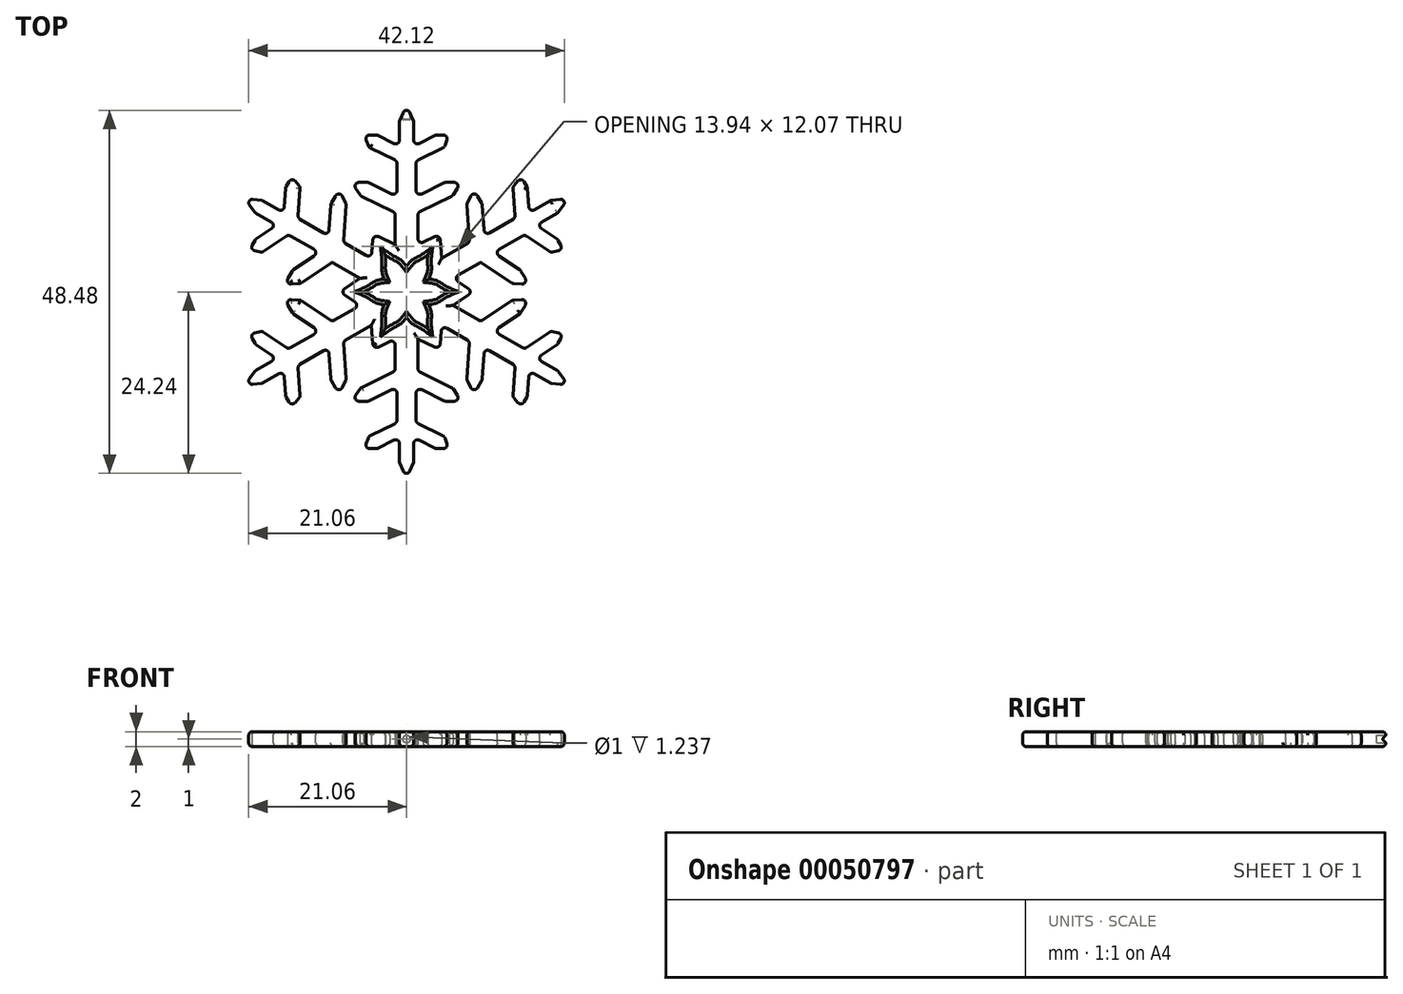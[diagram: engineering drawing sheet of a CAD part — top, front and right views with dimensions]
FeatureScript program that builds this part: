
annotation { "Feature Type Name" : "Feature", "Feature Type Description" : "" }
export const myFeature = defineFeature(function(context is Context, id is Id, definition is map)
    precondition{}
    {
        {
            var Q0;
            Q0=qCreatedBy(makeId("Top.planeOp"),FACE);
            var sketch = newSketch(context, id + "F0", { "sketchPlane" : qUnion([Q0])});
            skLineSegment(sketch, "E0", {"start": v(0, 0) * mm, "end": v(0, 29.9) * mm, "construction": true});
            skCircle(sketch, "E1", {"center": v(0, 0) * mm, "radius": 25 * mm, "construction": true});
            skLineSegment(sketch, "E2", {"start": v(0, 25) * mm, "end": v(0.95, 22.8) * mm});
            skLineSegment(sketch, "E3", {"start": v(0.95, 22.8) * mm, "end": v(0.95, 19.45) * mm});
            skLineSegment(sketch, "E4", {"start": v(0.95, 19.45) * mm, "end": v(4, 20.95) * mm});
            skLineSegment(sketch, "E5", {"start": v(4, 20.95) * mm, "end": v(5.6, 20.95) * mm});
            skLineSegment(sketch, "E6", {"start": v(5.6, 20.95) * mm, "end": v(5.04, 19.3) * mm});
            skLineSegment(sketch, "E7", {"start": v(5.04, 19.3) * mm, "end": v(1.28, 17.45) * mm});
            skLineSegment(sketch, "E8", {"start": v(1.28, 17.45) * mm, "end": v(1.28, 12.72) * mm});
            skLineSegment(sketch, "E9", {"start": v(1.28, 12.72) * mm, "end": v(5.11, 14.6) * mm});
            skLineSegment(sketch, "E10", {"start": v(5.11, 14.6) * mm, "end": v(7.32, 14.6) * mm});
            skLineSegment(sketch, "E11", {"start": v(7.32, 14.6) * mm, "end": v(6.11, 12.82) * mm});
            skLineSegment(sketch, "E12", {"start": v(6.11, 12.82) * mm, "end": v(1.52, 10.57) * mm});
            skLineSegment(sketch, "E13", {"start": v(1.52, 10.57) * mm, "end": v(1.52, 6.3) * mm});
            skLineSegment(sketch, "E14", {"start": v(1.52, 6.3) * mm, "end": v(4.43, 7.68) * mm});
            skLineSegment(sketch, "E15.MirrorCS", {"start": v(-0.95, 22.8) * mm, "end": v(-0.95, 19.45) * mm});
            skLineSegment(sketch, "E16.MirrorCS", {"start": v(-4, 20.95) * mm, "end": v(-5.6, 20.95) * mm});
            skLineSegment(sketch, "E17.MirrorCS", {"start": v(-0.95, 19.45) * mm, "end": v(-4, 20.95) * mm});
            skLineSegment(sketch, "E18.MirrorCS", {"start": v(-1.28, 12.72) * mm, "end": v(-5.11, 14.6) * mm});
            skLineSegment(sketch, "E19.MirrorCS", {"start": v(-5.11, 14.6) * mm, "end": v(-7.32, 14.6) * mm});
            skLineSegment(sketch, "E20.MirrorCS", {"start": v(-7.32, 14.6) * mm, "end": v(-6.11, 12.82) * mm});
            skLineSegment(sketch, "E21.MirrorCS", {"start": v(-1.28, 17.45) * mm, "end": v(-1.28, 12.72) * mm});
            skLineSegment(sketch, "E22.MirrorCS", {"start": v(0, 25) * mm, "end": v(-0.95, 22.8) * mm});
            skLineSegment(sketch, "E23.MirrorCS", {"start": v(-5.6, 20.95) * mm, "end": v(-5.04, 19.3) * mm});
            skLineSegment(sketch, "E24.MirrorCS", {"start": v(-5.04, 19.3) * mm, "end": v(-1.28, 17.45) * mm});
            skLineSegment(sketch, "E25.MirrorCS", {"start": v(-6.11, 12.82) * mm, "end": v(-1.52, 10.57) * mm});
            skLineSegment(sketch, "E26", {"start": v(0, 0) * mm, "end": v(0, 30.32) * mm, "construction": true});
            skLineSegment(sketch, "E27", {"start": v(0, 0) * mm, "end": v(17.52, 30.35) * mm, "construction": true});
            skLineSegment(sketch, "E28", {"start": v(0, 0) * mm, "end": v(-18.63, 32.26) * mm, "construction": true});
            skLineSegment(sketch, "E29", {"start": v(4.43, 7.68) * mm, "end": v(2.85, 4.93) * mm});
            skLineSegment(sketch, "E30.MirrorCS", {"start": v(-1.52, 10.57) * mm, "end": v(-1.52, 6.3) * mm});
            skLineSegment(sketch, "E31.MirrorCS", {"start": v(-1.52, 6.3) * mm, "end": v(-4.43, 7.68) * mm});
            skFitSpline(sketch, "E32", {"points": [v(2.85, 4.93) * mm, v(0, 2.57) * mm], "startDerivative": vector(-4.57, -3.43) * mm, "endDerivative": vector(-3.94, -5.85) * mm});
            skFitSpline(sketch, "E33.MirrorCS", {"points": [v(-2.85, 4.93) * mm, v(0, 2.57) * mm], "startDerivative": vector(4.57, -3.43) * mm, "endDerivative": vector(3.94, -5.85) * mm});
            skLineSegment(sketch, "E34.MirrorCS", {"start": v(-4.43, 7.68) * mm, "end": v(-2.85, 4.93) * mm});
            skSolve(sketch);
        }
        {
            var Q0;
            Q0=makeQuery(id+"F0.imprint","IMPRINT",FACE,{"disambiguationData":[TD([[makeQuery(id+"F0.imprint","IMPRINT",EDGE,{"derivedFrom":sQuery(id+"F0.wireOp",EDGE,"E2")}),-1.0]])]});
            extrude(context, id + "F1", {"entities" : qUnion([Q0]), "endBound" : BoundingType.SYMMETRIC, "depth" : 2 * mm});
        }
        {
            var Q0;
            Q0=qCreatedBy(makeId("Front.planeOp"),FACE);
            var sketch = newSketch(context, id + "F2", { "sketchPlane" : qUnion([Q0])});
            skLineSegment(sketch, "E35", {"start": v(0, -15.67) * mm, "end": v(0, 28.6) * mm, "construction": true});
            skSolve(sketch);
        }
        {
            var Q0;
            Q0=makeQuery(id+"F1.opExtrude","SWEPT_BODY",BODY,{"disambiguationData":[OSD([sQuery(id+"F0.wireOp",EDGE,"E2"),sQuery(id+"F0.wireOp",EDGE,"E3"),sQuery(id+"F0.wireOp",EDGE,"E4"),sQuery(id+"F0.wireOp",EDGE,"E5"),sQuery(id+"F0.wireOp",EDGE,"E6"),sQuery(id+"F0.wireOp",EDGE,"E7"),sQuery(id+"F0.wireOp",EDGE,"E8"),sQuery(id+"F0.wireOp",EDGE,"E9"),sQuery(id+"F0.wireOp",EDGE,"E10"),sQuery(id+"F0.wireOp",EDGE,"E11"),sQuery(id+"F0.wireOp",EDGE,"E12"),sQuery(id+"F0.wireOp",EDGE,"E13"),sQuery(id+"F0.wireOp",EDGE,"E14"),sQuery(id+"F0.wireOp",EDGE,"b2b48e4d-2c92-4a1f-81ad-3469f6dd68cb"),sQuery(id+"F0.wireOp",EDGE,"E15.MirrorCS"),sQuery(id+"F0.wireOp",EDGE,"E16.MirrorCS"),sQuery(id+"F0.wireOp",EDGE,"E17.MirrorCS"),sQuery(id+"F0.wireOp",EDGE,"E18.MirrorCS"),sQuery(id+"F0.wireOp",EDGE,"E19.MirrorCS"),sQuery(id+"F0.wireOp",EDGE,"E20.MirrorCS"),sQuery(id+"F0.wireOp",EDGE,"E21.MirrorCS"),sQuery(id+"F0.wireOp",EDGE,"E22.MirrorCS"),sQuery(id+"F0.wireOp",EDGE,"E23.MirrorCS"),sQuery(id+"F0.wireOp",EDGE,"E24.MirrorCS"),sQuery(id+"F0.wireOp",EDGE,"E160.MirrorCS"),sQuery(id+"F0.wireOp",EDGE,"E25.MirrorCS"),sQuery(id+"F0.wireOp",EDGE,"4b62aa35-2862-45d5-86f5-f30a92808e40"),sQuery(id+"F0.wireOp",EDGE,"c1be86ca-d8b8-4c1e-b1f3-8d63ae980cd1")])]});
            var Q1;
            Q1=sQuery(id+"F2.wireOp",EDGE,"E35");
            circularPattern(context, id + "F3", {"operationType" : NewBodyOperationType.ADD, "entities" : qUnion([Q0]), "axis" : qUnion([Q1]), "angle" : 360 * degree, "instanceCount" : round(6), "equalSpace" : true});
        }
        {
            var Q0;
            Q0=makeQuery(id+"F1.opExtrude","CAP_EDGE",EDGE,{"disambiguationData":[OSD([sQuery(id+"F0.wireOp",EDGE,"E2")])],"isStart":false});
            var Q1;
            Q1=makeQuery(id+"F1.opExtrude","CAP_EDGE",EDGE,{"disambiguationData":[OSD([sQuery(id+"F0.wireOp",EDGE,"E10")])],"isStart":false});
            var Q2;
            Q2=makeQuery(id+"F1.opExtrude","CAP_EDGE",EDGE,{"disambiguationData":[OSD([sQuery(id+"F0.wireOp",EDGE,"E17.MirrorCS")])],"isStart":false});
            var Q3;
            Q3=makeQuery(id+"F1.opExtrude","CAP_EDGE",EDGE,{"disambiguationData":[OSD([sQuery(id+"F0.wireOp",EDGE,"E18.MirrorCS")])],"isStart":true});
            var Q4;
            Q4=makeQuery(id+"F1.opExtrude","CAP_EDGE",EDGE,{"disambiguationData":[OSD([sQuery(id+"F0.wireOp",EDGE,"E3")])],"isStart":false});
            var Q5;
            Q5=makeQuery(id+"F1.opExtrude","CAP_EDGE",EDGE,{"disambiguationData":[OSD([sQuery(id+"F0.wireOp",EDGE,"E18.MirrorCS")])],"isStart":false});
            var Q6;
            Q6=makeQuery(id+"F1.opExtrude","CAP_EDGE",EDGE,{"disambiguationData":[OSD([sQuery(id+"F0.wireOp",EDGE,"E25.MirrorCS")])],"isStart":false});
            var Q7;
            Q7=makeQuery(id+"F1.opExtrude","CAP_EDGE",EDGE,{"disambiguationData":[OSD([sQuery(id+"F0.wireOp",EDGE,"E4")])],"isStart":false});
            var Q8;
            Q8=makeQuery(id+"F1.opExtrude","CAP_EDGE",EDGE,{"disambiguationData":[OSD([sQuery(id+"F0.wireOp",EDGE,"E12")])],"isStart":false});
            var Q9;
            Q9=makeQuery(id+"F1.opExtrude","CAP_EDGE",EDGE,{"disambiguationData":[OSD([sQuery(id+"F0.wireOp",EDGE,"E19.MirrorCS")])],"isStart":false});
            var Q10;
            Q10=makeQuery(id+"F1.opExtrude","CAP_EDGE",EDGE,{"disambiguationData":[OSD([sQuery(id+"F0.wireOp",EDGE,"E13")])],"isStart":false});
            var Q11;
            Q11=makeQuery(id+"F1.opExtrude","CAP_EDGE",EDGE,{"disambiguationData":[OSD([sQuery(id+"F0.wireOp",EDGE,"E21.MirrorCS")])],"isStart":false});
            var Q12;
            Q12=makeQuery(id+"F1.opExtrude","SWEPT_FACE",FACE,{"disambiguationData":[OSD([sQuery(id+"F0.wireOp",EDGE,"E21.MirrorCS")])]});
            var Q13;
            Q13=makeQuery(id+"F1.opExtrude","CAP_EDGE",EDGE,{"disambiguationData":[OSD([sQuery(id+"F0.wireOp",EDGE,"E7")])],"isStart":false});
            var Q14;
            Q14=makeQuery(id+"F1.opExtrude","CAP_EDGE",EDGE,{"disambiguationData":[OSD([sQuery(id+"F0.wireOp",EDGE,"E15.MirrorCS")])],"isStart":false});
            var Q15;
            Q15=makeQuery(id+"F1.opExtrude","CAP_EDGE",EDGE,{"disambiguationData":[OSD([sQuery(id+"F0.wireOp",EDGE,"E8")])],"isStart":false});
            var Q16;
            Q16=makeQuery(id+"F3.opPattern","COPY",EDGE,{"derivedFrom":makeQuery(id+"F1.opExtrude","CAP_EDGE",EDGE,{"disambiguationData":[OSD([sQuery(id+"F0.wireOp",EDGE,"E12")])],"isStart":false}),"instanceName":"4"});
            var Q17;
            Q17=makeQuery(id+"F3.opPattern","COPY",EDGE,{"derivedFrom":makeQuery(id+"F1.opExtrude","CAP_EDGE",EDGE,{"disambiguationData":[OSD([sQuery(id+"F0.wireOp",EDGE,"E4")])],"isStart":false}),"instanceName":"4"});
            var Q18;
            Q18=makeQuery(id+"F3.opPattern","COPY",EDGE,{"derivedFrom":makeQuery(id+"F1.opExtrude","CAP_EDGE",EDGE,{"disambiguationData":[OSD([sQuery(id+"F0.wireOp",EDGE,"E17.MirrorCS")])],"isStart":false}),"instanceName":"5"});
            var Q19;
            Q19=makeQuery(id+"F3.opPattern","COPY",EDGE,{"derivedFrom":makeQuery(id+"F1.opExtrude","CAP_EDGE",EDGE,{"disambiguationData":[OSD([sQuery(id+"F0.wireOp",EDGE,"E10")])],"isStart":false}),"instanceName":"5"});
            var Q20;
            Q20=makeQuery(id+"F3.opPattern","COPY",EDGE,{"derivedFrom":makeQuery(id+"F1.opExtrude","CAP_EDGE",EDGE,{"disambiguationData":[OSD([sQuery(id+"F0.wireOp",EDGE,"E17.MirrorCS")])],"isStart":false}),"instanceName":"1"});
            var Q21;
            Q21=makeQuery(id+"F3.opPattern","COPY",EDGE,{"derivedFrom":makeQuery(id+"F1.opExtrude","CAP_EDGE",EDGE,{"disambiguationData":[OSD([sQuery(id+"F0.wireOp",EDGE,"E2")])],"isStart":false}),"instanceName":"1"});
            var Q22;
            Q22=makeQuery(id+"F3.opPattern","COPY",EDGE,{"derivedFrom":makeQuery(id+"F1.opExtrude","CAP_EDGE",EDGE,{"disambiguationData":[OSD([sQuery(id+"F0.wireOp",EDGE,"E15.MirrorCS")])],"isStart":false}),"instanceName":"2"});
            var Q23;
            Q23=makeQuery(id+"F3.opPattern","COPY",EDGE,{"derivedFrom":makeQuery(id+"F1.opExtrude","CAP_EDGE",EDGE,{"disambiguationData":[OSD([sQuery(id+"F0.wireOp",EDGE,"E21.MirrorCS")])],"isStart":false}),"instanceName":"3"});
            var Q24;
            Q24=makeQuery(id+"F1.opExtrude","CAP_EDGE",EDGE,{"disambiguationData":[OSD([sQuery(id+"F0.wireOp",EDGE,"E24.MirrorCS")])],"isStart":false});
            var Q25;
            Q25=makeQuery(id+"F1.opExtrude","CAP_EDGE",EDGE,{"disambiguationData":[OSD([sQuery(id+"F0.wireOp",EDGE,"E9")])],"isStart":false});
            var Q26;
            Q26=makeQuery(id+"F3.opPattern","COPY",FACE,{"derivedFrom":makeQuery(id+"F1.opExtrude","SWEPT_FACE",FACE,{"disambiguationData":[OSD([sQuery(id+"F0.wireOp",EDGE,"E21.MirrorCS")])]}),"instanceName":"5"});
            var Q27;
            Q27=makeQuery(id+"F3.opPattern","COPY",EDGE,{"derivedFrom":makeQuery(id+"F1.opExtrude","CAP_EDGE",EDGE,{"disambiguationData":[OSD([sQuery(id+"F0.wireOp",EDGE,"E25.MirrorCS")])],"isStart":false}),"instanceName":"5"});
            var Q28;
            Q28=makeQuery(id+"F3.opPattern","COPY",EDGE,{"derivedFrom":makeQuery(id+"F1.opExtrude","CAP_EDGE",EDGE,{"disambiguationData":[OSD([sQuery(id+"F0.wireOp",EDGE,"E25.MirrorCS")])],"isStart":false}),"instanceName":"1"});
            var Q29;
            Q29=makeQuery(id+"F3.opPattern","COPY",EDGE,{"derivedFrom":makeQuery(id+"F1.opExtrude","CAP_EDGE",EDGE,{"disambiguationData":[OSD([sQuery(id+"F0.wireOp",EDGE,"E18.MirrorCS")])],"isStart":false}),"instanceName":"1"});
            var Q30;
            Q30=makeQuery(id+"F3.opPattern","COPY",EDGE,{"derivedFrom":makeQuery(id+"F1.opExtrude","CAP_EDGE",EDGE,{"disambiguationData":[OSD([sQuery(id+"F0.wireOp",EDGE,"E3")])],"isStart":false}),"instanceName":"1"});
            var Q31;
            Q31=makeQuery(id+"F3.opPattern","COPY",EDGE,{"derivedFrom":makeQuery(id+"F1.opExtrude","CAP_EDGE",EDGE,{"disambiguationData":[OSD([sQuery(id+"F0.wireOp",EDGE,"E9")])],"isStart":false}),"instanceName":"2"});
            var Q32;
            Q32=makeQuery(id+"F3.opPattern","COPY",EDGE,{"derivedFrom":makeQuery(id+"F1.opExtrude","CAP_EDGE",EDGE,{"disambiguationData":[OSD([sQuery(id+"F0.wireOp",EDGE,"E7")])],"isStart":false}),"instanceName":"3"});
            var Q33;
            Q33=makeQuery(id+"F3.opPattern","COPY",EDGE,{"derivedFrom":makeQuery(id+"F1.opExtrude","CAP_EDGE",EDGE,{"disambiguationData":[OSD([sQuery(id+"F0.wireOp",EDGE,"E24.MirrorCS")])],"isStart":false}),"instanceName":"2"});
            var Q34;
            Q34=makeQuery(id+"F3.opPattern","COPY",EDGE,{"derivedFrom":makeQuery(id+"F1.opExtrude","CAP_EDGE",EDGE,{"disambiguationData":[OSD([sQuery(id+"F0.wireOp",EDGE,"E20.MirrorCS")])],"isStart":false}),"instanceName":"4"});
            var Q35;
            Q35=makeQuery(id+"F3.opPattern","COPY",EDGE,{"derivedFrom":makeQuery(id+"F1.opExtrude","CAP_EDGE",EDGE,{"disambiguationData":[OSD([sQuery(id+"F0.wireOp",EDGE,"E18.MirrorCS")])],"isStart":false}),"instanceName":"5"});
            var Q36;
            Q36=makeQuery(id+"F3.opPattern","COPY",EDGE,{"derivedFrom":makeQuery(id+"F1.opExtrude","CAP_EDGE",EDGE,{"disambiguationData":[OSD([sQuery(id+"F0.wireOp",EDGE,"E13")])],"isStart":false}),"instanceName":"4"});
            var Q37;
            Q37=makeQuery(id+"F3.opPattern","COPY",EDGE,{"derivedFrom":makeQuery(id+"F1.opExtrude","CAP_EDGE",EDGE,{"disambiguationData":[OSD([sQuery(id+"F0.wireOp",EDGE,"E3")])],"isStart":false}),"instanceName":"5"});
            var Q38;
            Q38=makeQuery(id+"F3.opPattern","COPY",EDGE,{"derivedFrom":makeQuery(id+"F1.opExtrude","CAP_EDGE",EDGE,{"disambiguationData":[OSD([sQuery(id+"F0.wireOp",EDGE,"E4")])],"isStart":true}),"instanceName":"5"});
            var Q39;
            Q39=makeQuery(id+"F3.opPattern","COPY",FACE,{"derivedFrom":makeQuery(id+"F1.opExtrude","SWEPT_FACE",FACE,{"disambiguationData":[OSD([sQuery(id+"F0.wireOp",EDGE,"E21.MirrorCS")])]}),"instanceName":"4"});
            var Q40;
            Q40=makeQuery(id+"F3.opPattern","COPY",EDGE,{"derivedFrom":makeQuery(id+"F1.opExtrude","CAP_EDGE",EDGE,{"disambiguationData":[OSD([sQuery(id+"F0.wireOp",EDGE,"E2")])],"isStart":false}),"instanceName":"2"});
            var Q41;
            Q41=makeQuery(id+"F3.opPattern","COPY",EDGE,{"derivedFrom":makeQuery(id+"F1.opExtrude","CAP_EDGE",EDGE,{"disambiguationData":[OSD([sQuery(id+"F0.wireOp",EDGE,"E17.MirrorCS")])],"isStart":false}),"instanceName":"2"});
            var Q42;
            Q42=makeQuery(id+"F3.opPattern","COPY",EDGE,{"derivedFrom":makeQuery(id+"F1.opExtrude","CAP_EDGE",EDGE,{"disambiguationData":[OSD([sQuery(id+"F0.wireOp",EDGE,"E10")])],"isStart":false}),"instanceName":"2"});
            var Q43;
            Q43=makeQuery(id+"F3.opPattern","COPY",EDGE,{"derivedFrom":makeQuery(id+"F1.opExtrude","CAP_EDGE",EDGE,{"disambiguationData":[OSD([sQuery(id+"F0.wireOp",EDGE,"E8")])],"isStart":false}),"instanceName":"3"});
            var Q44;
            Q44=makeQuery(id+"F3.opPattern","COPY",EDGE,{"derivedFrom":makeQuery(id+"F1.opExtrude","CAP_EDGE",EDGE,{"disambiguationData":[OSD([sQuery(id+"F0.wireOp",EDGE,"E15.MirrorCS")])],"isStart":false}),"instanceName":"3"});
            var Q45;
            Q45=makeQuery(id+"F3.opPattern","COPY",EDGE,{"derivedFrom":makeQuery(id+"F1.opExtrude","CAP_EDGE",EDGE,{"disambiguationData":[OSD([sQuery(id+"F0.wireOp",EDGE,"E21.MirrorCS")])],"isStart":false}),"instanceName":"4"});
            var Q46;
            Q46=makeQuery(id+"F3.opPattern","COPY",EDGE,{"derivedFrom":makeQuery(id+"F1.opExtrude","CAP_EDGE",EDGE,{"disambiguationData":[OSD([sQuery(id+"F0.wireOp",EDGE,"E19.MirrorCS")])],"isStart":false}),"instanceName":"5"});
            var Q47;
            Q47=makeQuery(id+"F3.opPattern","COPY",EDGE,{"derivedFrom":makeQuery(id+"F1.opExtrude","CAP_EDGE",EDGE,{"disambiguationData":[OSD([sQuery(id+"F0.wireOp",EDGE,"E4")])],"isStart":false}),"instanceName":"5"});
            var Q48;
            Q48=makeQuery(id+"F3.opPattern","COPY",EDGE,{"derivedFrom":makeQuery(id+"F1.opExtrude","CAP_EDGE",EDGE,{"disambiguationData":[OSD([sQuery(id+"F0.wireOp",EDGE,"E12")])],"isStart":false}),"instanceName":"5"});
            var Q49;
            Q49=makeQuery(id+"F3.opPattern","COPY",EDGE,{"derivedFrom":makeQuery(id+"F1.opExtrude","CAP_EDGE",EDGE,{"disambiguationData":[OSD([sQuery(id+"F0.wireOp",EDGE,"E12")])],"isStart":false}),"instanceName":"1"});
            var Q50;
            Q50=makeQuery(id+"F3.opPattern","COPY",EDGE,{"derivedFrom":makeQuery(id+"F1.opExtrude","CAP_EDGE",EDGE,{"disambiguationData":[OSD([sQuery(id+"F0.wireOp",EDGE,"E19.MirrorCS")])],"isStart":false}),"instanceName":"1"});
            var Q51;
            Q51=makeQuery(id+"F3.opPattern","COPY",EDGE,{"derivedFrom":makeQuery(id+"F1.opExtrude","CAP_EDGE",EDGE,{"disambiguationData":[OSD([sQuery(id+"F0.wireOp",EDGE,"E4")])],"isStart":false}),"instanceName":"1"});
            var Q52;
            Q52=makeQuery(id+"F3.opPattern","COPY",EDGE,{"derivedFrom":makeQuery(id+"F1.opExtrude","CAP_EDGE",EDGE,{"disambiguationData":[OSD([sQuery(id+"F0.wireOp",EDGE,"E24.MirrorCS")])],"isStart":false}),"instanceName":"3"});
            var Q53;
            Q53=makeQuery(id+"F3.opPattern","COPY",EDGE,{"derivedFrom":makeQuery(id+"F1.opExtrude","CAP_EDGE",EDGE,{"disambiguationData":[OSD([sQuery(id+"F0.wireOp",EDGE,"E13")])],"isStart":false}),"instanceName":"5"});
            var Q54;
            Q54=makeQuery(id+"F3.opPattern","COPY",EDGE,{"derivedFrom":makeQuery(id+"F1.opExtrude","CAP_EDGE",EDGE,{"disambiguationData":[OSD([sQuery(id+"F0.wireOp",EDGE,"E7")])],"isStart":false}),"instanceName":"4"});
            var Q55;
            Q55=makeQuery(id+"F3.opPattern","COPY",FACE,{"derivedFrom":makeQuery(id+"F1.opExtrude","SWEPT_FACE",FACE,{"disambiguationData":[OSD([sQuery(id+"F0.wireOp",EDGE,"E18.MirrorCS")])]}),"instanceName":"1"});
            var Q56;
            Q56=makeQuery(id+"F3.opPattern","COPY",FACE,{"derivedFrom":makeQuery(id+"F1.opExtrude","SWEPT_FACE",FACE,{"disambiguationData":[OSD([sQuery(id+"F0.wireOp",EDGE,"E24.MirrorCS")])]}),"instanceName":"4"});
            var Q57;
            Q57=makeQuery(id+"F3.opPattern","COPY",EDGE,{"derivedFrom":makeQuery(id+"F1.opExtrude","CAP_EDGE",EDGE,{"disambiguationData":[OSD([sQuery(id+"F0.wireOp",EDGE,"E13")])],"isStart":false}),"instanceName":"1"});
            var Q58;
            Q58=makeQuery(id+"F3.opPattern","COPY",EDGE,{"derivedFrom":makeQuery(id+"F1.opExtrude","CAP_EDGE",EDGE,{"disambiguationData":[OSD([sQuery(id+"F0.wireOp",EDGE,"E18.MirrorCS")])],"isStart":false}),"instanceName":"2"});
            var Q59;
            Q59=makeQuery(id+"F3.opPattern","COPY",EDGE,{"derivedFrom":makeQuery(id+"F1.opExtrude","CAP_EDGE",EDGE,{"disambiguationData":[OSD([sQuery(id+"F0.wireOp",EDGE,"E3")])],"isStart":false}),"instanceName":"2"});
            var Q60;
            Q60=makeQuery(id+"F3.opPattern","COPY",EDGE,{"derivedFrom":makeQuery(id+"F1.opExtrude","CAP_EDGE",EDGE,{"disambiguationData":[OSD([sQuery(id+"F0.wireOp",EDGE,"E9")])],"isStart":false}),"instanceName":"3"});
            var Q61;
            Q61=makeQuery(id+"F3.opPattern","COPY",EDGE,{"derivedFrom":makeQuery(id+"F1.opExtrude","CAP_EDGE",EDGE,{"disambiguationData":[OSD([sQuery(id+"F0.wireOp",EDGE,"E25.MirrorCS")])],"isStart":false}),"instanceName":"2"});
            var Q62;
            Q62=makeQuery(id+"F3.opPattern","COPY",EDGE,{"derivedFrom":makeQuery(id+"F1.opExtrude","CAP_EDGE",EDGE,{"disambiguationData":[OSD([sQuery(id+"F0.wireOp",EDGE,"E21.MirrorCS")])],"isStart":false}),"instanceName":"5"});
            var Q63;
            Q63=makeQuery(id+"F3.opPattern","COPY",FACE,{"derivedFrom":makeQuery(id+"F1.opExtrude","SWEPT_FACE",FACE,{"disambiguationData":[OSD([sQuery(id+"F0.wireOp",EDGE,"E24.MirrorCS")])]}),"instanceName":"3"});
            var Q64;
            Q64=makeQuery(id+"F3.opPattern","COPY",EDGE,{"derivedFrom":makeQuery(id+"F1.opExtrude","CAP_EDGE",EDGE,{"disambiguationData":[OSD([sQuery(id+"F0.wireOp",EDGE,"E21.MirrorCS")])],"isStart":false}),"instanceName":"1"});
            var Q65;
            Q65=makeQuery(id+"F3.opPattern","COPY",EDGE,{"derivedFrom":makeQuery(id+"F1.opExtrude","CAP_EDGE",EDGE,{"disambiguationData":[OSD([sQuery(id+"F0.wireOp",EDGE,"E14")])],"isStart":false}),"instanceName":"1"});
            var Q66;
            Q66=makeQuery(id+"F3.opPattern","COPY",EDGE,{"derivedFrom":makeQuery(id+"F1.opExtrude","CAP_EDGE",EDGE,{"disambiguationData":[OSD([sQuery(id+"F0.wireOp",EDGE,"E19.MirrorCS")])],"isStart":false}),"instanceName":"2"});
            var Q67;
            Q67=makeQuery(id+"F3.opPattern","COPY",EDGE,{"derivedFrom":makeQuery(id+"F1.opExtrude","CAP_EDGE",EDGE,{"disambiguationData":[OSD([sQuery(id+"F0.wireOp",EDGE,"E12")])],"isStart":false}),"instanceName":"2"});
            var Q68;
            Q68=makeQuery(id+"F3.opPattern","COPY",EDGE,{"derivedFrom":makeQuery(id+"F1.opExtrude","CAP_EDGE",EDGE,{"disambiguationData":[OSD([sQuery(id+"F0.wireOp",EDGE,"E4")])],"isStart":false}),"instanceName":"2"});
            var Q69;
            Q69=makeQuery(id+"F3.opPattern","COPY",EDGE,{"derivedFrom":makeQuery(id+"F1.opExtrude","CAP_EDGE",EDGE,{"disambiguationData":[OSD([sQuery(id+"F0.wireOp",EDGE,"E2")])],"isStart":false}),"instanceName":"3"});
            var Q70;
            Q70=makeQuery(id+"F3.opPattern","COPY",EDGE,{"derivedFrom":makeQuery(id+"F1.opExtrude","CAP_EDGE",EDGE,{"disambiguationData":[OSD([sQuery(id+"F0.wireOp",EDGE,"E17.MirrorCS")])],"isStart":false}),"instanceName":"3"});
            var Q71;
            Q71=makeQuery(id+"F3.opPattern","COPY",EDGE,{"derivedFrom":makeQuery(id+"F1.opExtrude","CAP_EDGE",EDGE,{"disambiguationData":[OSD([sQuery(id+"F0.wireOp",EDGE,"E8")])],"isStart":false}),"instanceName":"4"});
            var Q72;
            Q72=makeQuery(id+"F3.opPattern","COPY",EDGE,{"derivedFrom":makeQuery(id+"F1.opExtrude","CAP_EDGE",EDGE,{"disambiguationData":[OSD([sQuery(id+"F0.wireOp",EDGE,"E7")])],"isStart":false}),"instanceName":"1"});
            var Q73;
            Q73=makeQuery(id+"F3.opPattern","COPY",FACE,{"derivedFrom":makeQuery(id+"F1.opExtrude","SWEPT_FACE",FACE,{"disambiguationData":[OSD([sQuery(id+"F0.wireOp",EDGE,"E25.MirrorCS")])]}),"instanceName":"3"});
            var Q74;
            Q74=makeQuery(id+"F3.opPattern","COPY",EDGE,{"derivedFrom":makeQuery(id+"F1.opExtrude","CAP_EDGE",EDGE,{"disambiguationData":[OSD([sQuery(id+"F0.wireOp",EDGE,"E5")])],"isStart":false}),"instanceName":"2"});
            var Q75;
            Q75=makeQuery(id+"F3.opPattern","COPY",EDGE,{"derivedFrom":makeQuery(id+"F1.opExtrude","CAP_EDGE",EDGE,{"disambiguationData":[OSD([sQuery(id+"F0.wireOp",EDGE,"E13")])],"isStart":false}),"instanceName":"2"});
            var Q76;
            Q76=makeQuery(id+"F3.opPattern","COPY",EDGE,{"derivedFrom":makeQuery(id+"F1.opExtrude","CAP_EDGE",EDGE,{"disambiguationData":[OSD([sQuery(id+"F0.wireOp",EDGE,"E18.MirrorCS")])],"isStart":false}),"instanceName":"3"});
            var Q77;
            Q77=makeQuery(id+"F3.opPattern","COPY",EDGE,{"derivedFrom":makeQuery(id+"F1.opExtrude","CAP_EDGE",EDGE,{"disambiguationData":[OSD([sQuery(id+"F0.wireOp",EDGE,"E25.MirrorCS")])],"isStart":false}),"instanceName":"3"});
            var Q78;
            Q78=makeQuery(id+"F3.opPattern","COPY",EDGE,{"derivedFrom":makeQuery(id+"F1.opExtrude","CAP_EDGE",EDGE,{"disambiguationData":[OSD([sQuery(id+"F0.wireOp",EDGE,"E3")])],"isStart":false}),"instanceName":"3"});
            var Q79;
            Q79=makeQuery(id+"F3.opPattern","COPY",EDGE,{"derivedFrom":makeQuery(id+"F1.opExtrude","CAP_EDGE",EDGE,{"disambiguationData":[OSD([sQuery(id+"F0.wireOp",EDGE,"E9")])],"isStart":false}),"instanceName":"4"});
            var Q80;
            Q80=makeQuery(id+"F3.opPattern","COPY",EDGE,{"derivedFrom":makeQuery(id+"F1.opExtrude","CAP_EDGE",EDGE,{"disambiguationData":[OSD([sQuery(id+"F0.wireOp",EDGE,"E7")])],"isStart":false}),"instanceName":"5"});
            var Q81;
            Q81=makeQuery(id+"F3.opPattern","COPY",EDGE,{"derivedFrom":makeQuery(id+"F1.opExtrude","CAP_EDGE",EDGE,{"disambiguationData":[OSD([sQuery(id+"F0.wireOp",EDGE,"E24.MirrorCS")])],"isStart":false}),"instanceName":"4"});
            var Q82;
            Q82=makeQuery(id+"F3.opPattern","COPY",EDGE,{"derivedFrom":makeQuery(id+"F1.opExtrude","SWEPT_EDGE",EDGE,{"disambiguationData":[OSD([sQuery(id+"F0.wireOp",EDGE,"E23.MirrorCS"),sQuery(id+"F0.wireOp",EDGE,"E24.MirrorCS")])]}),"instanceName":"1"});
            var Q83;
            Q83=makeQuery(id+"F3.opPattern","COPY",FACE,{"derivedFrom":makeQuery(id+"F1.opExtrude","SWEPT_FACE",FACE,{"disambiguationData":[OSD([sQuery(id+"F0.wireOp",EDGE,"E12")])]}),"instanceName":"3"});
            var Q84;
            Q84=makeQuery(id+"F3.opPattern","COPY",EDGE,{"derivedFrom":makeQuery(id+"F1.opExtrude","CAP_EDGE",EDGE,{"disambiguationData":[OSD([sQuery(id+"F0.wireOp",EDGE,"E15.MirrorCS")])],"isStart":false}),"instanceName":"1"});
            var Q85;
            Q85=makeQuery(id+"F3.opPattern","COPY",EDGE,{"derivedFrom":makeQuery(id+"F1.opExtrude","CAP_EDGE",EDGE,{"disambiguationData":[OSD([sQuery(id+"F0.wireOp",EDGE,"E8")])],"isStart":false}),"instanceName":"1"});
            var Q86;
            Q86=makeQuery(id+"F3.opPattern","COPY",EDGE,{"derivedFrom":makeQuery(id+"F1.opExtrude","CAP_EDGE",EDGE,{"disambiguationData":[OSD([sQuery(id+"F0.wireOp",EDGE,"E21.MirrorCS")])],"isStart":false}),"instanceName":"2"});
            var Q87;
            Q87=makeQuery(id+"F3.opPattern","COPY",EDGE,{"derivedFrom":makeQuery(id+"F1.opExtrude","CAP_EDGE",EDGE,{"disambiguationData":[OSD([sQuery(id+"F0.wireOp",EDGE,"E12")])],"isStart":false}),"instanceName":"3"});
            var Q88;
            Q88=makeQuery(id+"F3.opPattern","COPY",EDGE,{"derivedFrom":makeQuery(id+"F1.opExtrude","CAP_EDGE",EDGE,{"disambiguationData":[OSD([sQuery(id+"F0.wireOp",EDGE,"E17.MirrorCS")])],"isStart":false}),"instanceName":"4"});
            var Q89;
            Q89=makeQuery(id+"F3.opPattern","COPY",EDGE,{"derivedFrom":makeQuery(id+"F1.opExtrude","CAP_EDGE",EDGE,{"disambiguationData":[OSD([sQuery(id+"F0.wireOp",EDGE,"E4")])],"isStart":false}),"instanceName":"3"});
            var Q90;
            Q90=makeQuery(id+"F3.opPattern","COPY",EDGE,{"derivedFrom":makeQuery(id+"F1.opExtrude","CAP_EDGE",EDGE,{"disambiguationData":[OSD([sQuery(id+"F0.wireOp",EDGE,"E2")])],"isStart":false}),"instanceName":"4"});
            var Q91;
            Q91=makeQuery(id+"F3.opPattern","COPY",EDGE,{"derivedFrom":makeQuery(id+"F1.opExtrude","CAP_EDGE",EDGE,{"disambiguationData":[OSD([sQuery(id+"F0.wireOp",EDGE,"E10")])],"isStart":false}),"instanceName":"4"});
            var Q92;
            Q92=makeQuery(id+"F3.opPattern","COPY",FACE,{"derivedFrom":makeQuery(id+"F1.opExtrude","SWEPT_FACE",FACE,{"disambiguationData":[OSD([sQuery(id+"F0.wireOp",EDGE,"E13")])]}),"instanceName":"3"});
            var Q93;
            Q93=makeQuery(id+"F3.opPattern","COPY",EDGE,{"derivedFrom":makeQuery(id+"F1.opExtrude","CAP_EDGE",EDGE,{"disambiguationData":[OSD([sQuery(id+"F0.wireOp",EDGE,"E160.MirrorCS")])],"isStart":false}),"instanceName":"4"});
            var Q94;
            Q94=makeQuery(id+"F3.opPattern","COPY",FACE,{"derivedFrom":makeQuery(id+"F1.opExtrude","SWEPT_FACE",FACE,{"disambiguationData":[OSD([sQuery(id+"F0.wireOp",EDGE,"E12")])]}),"instanceName":"2"});
            var Q95;
            Q95=makeQuery(id+"F3.opPattern","COPY",FACE,{"derivedFrom":makeQuery(id+"F1.opExtrude","SWEPT_FACE",FACE,{"disambiguationData":[OSD([sQuery(id+"F0.wireOp",EDGE,"E15.MirrorCS")])]}),"instanceName":"4"});
            var Q96;
            Q96=makeQuery(id+"F3.opPattern","COPY",EDGE,{"derivedFrom":makeQuery(id+"F1.opExtrude","CAP_EDGE",EDGE,{"disambiguationData":[OSD([sQuery(id+"F0.wireOp",EDGE,"E7")])],"isStart":false}),"instanceName":"2"});
            var Q97;
            Q97=makeQuery(id+"F3.opPattern","COPY",EDGE,{"derivedFrom":makeQuery(id+"F1.opExtrude","CAP_EDGE",EDGE,{"disambiguationData":[OSD([sQuery(id+"F0.wireOp",EDGE,"E9")])],"isStart":false}),"instanceName":"1"});
            var Q98;
            Q98=makeQuery(id+"F3.opPattern","COPY",EDGE,{"derivedFrom":makeQuery(id+"F1.opExtrude","CAP_EDGE",EDGE,{"disambiguationData":[OSD([sQuery(id+"F0.wireOp",EDGE,"E24.MirrorCS")])],"isStart":false}),"instanceName":"1"});
            var Q99;
            Q99=makeQuery(id+"F3.opPattern","COPY",EDGE,{"derivedFrom":makeQuery(id+"F1.opExtrude","CAP_EDGE",EDGE,{"disambiguationData":[OSD([sQuery(id+"F0.wireOp",EDGE,"E18.MirrorCS")])],"isStart":false}),"instanceName":"4"});
            var Q100;
            Q100=makeQuery(id+"F3.opPattern","COPY",EDGE,{"derivedFrom":makeQuery(id+"F1.opExtrude","CAP_EDGE",EDGE,{"disambiguationData":[OSD([sQuery(id+"F0.wireOp",EDGE,"E3")])],"isStart":false}),"instanceName":"4"});
            var Q101;
            Q101=makeQuery(id+"F3.opPattern","COPY",EDGE,{"derivedFrom":makeQuery(id+"F1.opExtrude","CAP_EDGE",EDGE,{"disambiguationData":[OSD([sQuery(id+"F0.wireOp",EDGE,"E24.MirrorCS")])],"isStart":false}),"instanceName":"5"});
            var Q102;
            Q102=makeQuery(id+"F3.opPattern","COPY",EDGE,{"derivedFrom":makeQuery(id+"F1.opExtrude","CAP_EDGE",EDGE,{"disambiguationData":[OSD([sQuery(id+"F0.wireOp",EDGE,"E9")])],"isStart":false}),"instanceName":"5"});
            var Q103;
            Q103=makeQuery(id+"F3.opPattern","COPY",EDGE,{"derivedFrom":makeQuery(id+"F1.opExtrude","CAP_EDGE",EDGE,{"disambiguationData":[OSD([sQuery(id+"F0.wireOp",EDGE,"E25.MirrorCS")])],"isStart":false}),"instanceName":"4"});
            var Q104;
            Q104=makeQuery(id+"F3.opPattern","COPY",FACE,{"derivedFrom":makeQuery(id+"F1.opExtrude","SWEPT_FACE",FACE,{"disambiguationData":[OSD([sQuery(id+"F0.wireOp",EDGE,"E13")])]}),"instanceName":"2"});
            var Q105;
            Q105=makeQuery(id+"F3.opPattern","COPY",EDGE,{"derivedFrom":makeQuery(id+"F1.opExtrude","CAP_EDGE",EDGE,{"disambiguationData":[OSD([sQuery(id+"F0.wireOp",EDGE,"E12")])],"isStart":true}),"instanceName":"4"});
            var Q106;
            Q106=makeQuery(id+"F3.opPattern","COPY",EDGE,{"derivedFrom":makeQuery(id+"F1.opExtrude","CAP_EDGE",EDGE,{"disambiguationData":[OSD([sQuery(id+"F0.wireOp",EDGE,"E160.MirrorCS")])],"isStart":false}),"instanceName":"5"});
            var Q107;
            Q107=makeQuery(id+"F1.opExtrude","SWEPT_FACE",FACE,{"disambiguationData":[OSD([sQuery(id+"F0.wireOp",EDGE,"E4")])]});
            var Q108;
            Q108=makeQuery(id+"F3.opPattern","COPY",EDGE,{"derivedFrom":makeQuery(id+"F1.opExtrude","CAP_EDGE",EDGE,{"disambiguationData":[OSD([sQuery(id+"F0.wireOp",EDGE,"E160.MirrorCS")])],"isStart":false}),"instanceName":"3"});
            var Q109;
            {var subQ0=makeQuery(id+"F1.opExtrude","CAP_FACE",FACE,{"disambiguationData":[OSD([sQuery(id+"F0.wireOp",EDGE,"E2"),sQuery(id+"F0.wireOp",EDGE,"E3"),sQuery(id+"F0.wireOp",EDGE,"E4"),sQuery(id+"F0.wireOp",EDGE,"E5"),sQuery(id+"F0.wireOp",EDGE,"E6"),sQuery(id+"F0.wireOp",EDGE,"E7"),sQuery(id+"F0.wireOp",EDGE,"E8"),sQuery(id+"F0.wireOp",EDGE,"E9"),sQuery(id+"F0.wireOp",EDGE,"E10"),sQuery(id+"F0.wireOp",EDGE,"E11"),sQuery(id+"F0.wireOp",EDGE,"E12"),sQuery(id+"F0.wireOp",EDGE,"E13"),sQuery(id+"F0.wireOp",EDGE,"E14"),sQuery(id+"F0.wireOp",EDGE,"b2b48e4d-2c92-4a1f-81ad-3469f6dd68cb"),sQuery(id+"F0.wireOp",EDGE,"E15.MirrorCS"),sQuery(id+"F0.wireOp",EDGE,"E16.MirrorCS"),sQuery(id+"F0.wireOp",EDGE,"E17.MirrorCS"),sQuery(id+"F0.wireOp",EDGE,"E18.MirrorCS"),sQuery(id+"F0.wireOp",EDGE,"E19.MirrorCS"),sQuery(id+"F0.wireOp",EDGE,"E20.MirrorCS"),sQuery(id+"F0.wireOp",EDGE,"E21.MirrorCS"),sQuery(id+"F0.wireOp",EDGE,"E22.MirrorCS"),sQuery(id+"F0.wireOp",EDGE,"E23.MirrorCS"),sQuery(id+"F0.wireOp",EDGE,"E24.MirrorCS"),sQuery(id+"F0.wireOp",EDGE,"E160.MirrorCS"),sQuery(id+"F0.wireOp",EDGE,"E25.MirrorCS"),sQuery(id+"F0.wireOp",EDGE,"4b62aa35-2862-45d5-86f5-f30a92808e40"),sQuery(id+"F0.wireOp",EDGE,"c1be86ca-d8b8-4c1e-b1f3-8d63ae980cd1")])],"isStart":true});Q109=makeQuery(id+"F3.boolean.opBoolean","MERGE",FACE,{"derivedFrom":[subQ0,makeQuery(id+"F3.opPattern","COPY",FACE,{"derivedFrom":subQ0,"instanceName":"1"}),makeQuery(id+"F3.opPattern","COPY",FACE,{"derivedFrom":subQ0,"instanceName":"2"}),makeQuery(id+"F3.opPattern","COPY",FACE,{"derivedFrom":subQ0,"instanceName":"3"}),makeQuery(id+"F3.opPattern","COPY",FACE,{"derivedFrom":subQ0,"instanceName":"4"}),makeQuery(id+"F3.opPattern","COPY",FACE,{"derivedFrom":subQ0,"instanceName":"5"})]});}
            var Q110;
            {var subQ0=makeQuery(id+"F1.opExtrude","CAP_FACE",FACE,{"disambiguationData":[OSD([sQuery(id+"F0.wireOp",EDGE,"E2"),sQuery(id+"F0.wireOp",EDGE,"E3"),sQuery(id+"F0.wireOp",EDGE,"E4"),sQuery(id+"F0.wireOp",EDGE,"E5"),sQuery(id+"F0.wireOp",EDGE,"E6"),sQuery(id+"F0.wireOp",EDGE,"E7"),sQuery(id+"F0.wireOp",EDGE,"E8"),sQuery(id+"F0.wireOp",EDGE,"E9"),sQuery(id+"F0.wireOp",EDGE,"E10"),sQuery(id+"F0.wireOp",EDGE,"E11"),sQuery(id+"F0.wireOp",EDGE,"E12"),sQuery(id+"F0.wireOp",EDGE,"E13"),sQuery(id+"F0.wireOp",EDGE,"E14"),sQuery(id+"F0.wireOp",EDGE,"b2b48e4d-2c92-4a1f-81ad-3469f6dd68cb"),sQuery(id+"F0.wireOp",EDGE,"E15.MirrorCS"),sQuery(id+"F0.wireOp",EDGE,"E16.MirrorCS"),sQuery(id+"F0.wireOp",EDGE,"E17.MirrorCS"),sQuery(id+"F0.wireOp",EDGE,"E18.MirrorCS"),sQuery(id+"F0.wireOp",EDGE,"E19.MirrorCS"),sQuery(id+"F0.wireOp",EDGE,"E20.MirrorCS"),sQuery(id+"F0.wireOp",EDGE,"E21.MirrorCS"),sQuery(id+"F0.wireOp",EDGE,"E22.MirrorCS"),sQuery(id+"F0.wireOp",EDGE,"E23.MirrorCS"),sQuery(id+"F0.wireOp",EDGE,"E24.MirrorCS"),sQuery(id+"F0.wireOp",EDGE,"E160.MirrorCS"),sQuery(id+"F0.wireOp",EDGE,"E25.MirrorCS"),sQuery(id+"F0.wireOp",EDGE,"4b62aa35-2862-45d5-86f5-f30a92808e40"),sQuery(id+"F0.wireOp",EDGE,"c1be86ca-d8b8-4c1e-b1f3-8d63ae980cd1")])],"isStart":false});Q110=makeQuery(id+"F3.boolean.opBoolean","MERGE",FACE,{"derivedFrom":[subQ0,makeQuery(id+"F3.opPattern","COPY",FACE,{"derivedFrom":subQ0,"instanceName":"1"}),makeQuery(id+"F3.opPattern","COPY",FACE,{"derivedFrom":subQ0,"instanceName":"2"}),makeQuery(id+"F3.opPattern","COPY",FACE,{"derivedFrom":subQ0,"instanceName":"3"}),makeQuery(id+"F3.opPattern","COPY",FACE,{"derivedFrom":subQ0,"instanceName":"4"}),makeQuery(id+"F3.opPattern","COPY",FACE,{"derivedFrom":subQ0,"instanceName":"5"})]});}
            var Q111;
            Q111=makeQuery(id+"F3.opPattern","COPY",FACE,{"derivedFrom":makeQuery(id+"F1.opExtrude","SWEPT_FACE",FACE,{"disambiguationData":[OSD([sQuery(id+"F0.wireOp",EDGE,"E8")])]}),"instanceName":"1"});
            var Q112;
            Q112=makeQuery(id+"F1.opExtrude","CAP_EDGE",EDGE,{"disambiguationData":[OSD([sQuery(id+"F0.wireOp",EDGE,"E160.MirrorCS")])],"isStart":false});
            var Q113;
            Q113=makeQuery(id+"F3.opPattern","COPY",EDGE,{"derivedFrom":makeQuery(id+"F1.opExtrude","CAP_EDGE",EDGE,{"disambiguationData":[OSD([sQuery(id+"F0.wireOp",EDGE,"E160.MirrorCS")])],"isStart":false}),"instanceName":"1"});
            var Q114;
            Q114=makeQuery(id+"F3.opPattern","COPY",FACE,{"derivedFrom":makeQuery(id+"F1.opExtrude","SWEPT_FACE",FACE,{"disambiguationData":[OSD([sQuery(id+"F0.wireOp",EDGE,"E160.MirrorCS")])]}),"instanceName":"3"});
            var Q115;
            Q115=makeQuery(id+"F3.opPattern","COPY",EDGE,{"derivedFrom":makeQuery(id+"F1.opExtrude","CAP_EDGE",EDGE,{"disambiguationData":[OSD([sQuery(id+"F0.wireOp",EDGE,"E160.MirrorCS")])],"isStart":false}),"instanceName":"2"});
            var Q116;
            Q116=makeQuery(id+"F1.opExtrude","CAP_EDGE",EDGE,{"disambiguationData":[OSD([sQuery(id+"F0.wireOp",EDGE,"E25.MirrorCS")])],"isStart":true});
            var Q117;
            Q117=makeQuery(id+"F1.opExtrude","CAP_EDGE",EDGE,{"disambiguationData":[OSD([sQuery(id+"F0.wireOp",EDGE,"E11")])],"isStart":false});
            var Q118;
            Q118=makeQuery(id+"F1.opExtrude","SWEPT_FACE",FACE,{"disambiguationData":[OSD([sQuery(id+"F0.wireOp",EDGE,"E15.MirrorCS")])]});
            var Q119;
            Q119=makeQuery(id+"F1.opExtrude","CAP_EDGE",EDGE,{"disambiguationData":[OSD([sQuery(id+"F0.wireOp",EDGE,"E4")])],"isStart":true});
            var Q120;
            Q120=makeQuery(id+"F1.opExtrude","SWEPT_FACE",FACE,{"disambiguationData":[OSD([sQuery(id+"F0.wireOp",EDGE,"E17.MirrorCS")])]});
            var Q121;
            Q121=makeQuery(id+"F1.opExtrude","SWEPT_FACE",FACE,{"disambiguationData":[OSD([sQuery(id+"F0.wireOp",EDGE,"E18.MirrorCS")])]});
            var Q122;
            Q122=makeQuery(id+"F1.opExtrude","CAP_EDGE",EDGE,{"disambiguationData":[OSD([sQuery(id+"F0.wireOp",EDGE,"E5")])],"isStart":false});
            var Q123;
            Q123=makeQuery(id+"F1.opExtrude","CAP_EDGE",EDGE,{"disambiguationData":[OSD([sQuery(id+"F0.wireOp",EDGE,"E20.MirrorCS")])],"isStart":false});
            var Q124;
            Q124=makeQuery(id+"F1.opExtrude","SWEPT_FACE",FACE,{"disambiguationData":[OSD([sQuery(id+"F0.wireOp",EDGE,"E19.MirrorCS")])]});
            var Q125;
            Q125=makeQuery(id+"F1.opExtrude","CAP_EDGE",EDGE,{"disambiguationData":[OSD([sQuery(id+"F0.wireOp",EDGE,"E21.MirrorCS")])],"isStart":true});
            var Q126;
            Q126=makeQuery(id+"F1.opExtrude","SWEPT_FACE",FACE,{"disambiguationData":[OSD([sQuery(id+"F0.wireOp",EDGE,"E20.MirrorCS")])]});
            var Q127;
            Q127=makeQuery(id+"F1.opExtrude","CAP_EDGE",EDGE,{"disambiguationData":[OSD([sQuery(id+"F0.wireOp",EDGE,"E6")])],"isStart":false});
            var Q128;
            Q128=makeQuery(id+"F1.opExtrude","CAP_EDGE",EDGE,{"disambiguationData":[OSD([sQuery(id+"F0.wireOp",EDGE,"E14")])],"isStart":false});
            var Q129;
            Q129=makeQuery(id+"F1.opExtrude","CAP_EDGE",EDGE,{"disambiguationData":[OSD([sQuery(id+"F0.wireOp",EDGE,"E22.MirrorCS")])],"isStart":false});
            var Q130;
            Q130=makeQuery(id+"F1.opExtrude","SWEPT_FACE",FACE,{"disambiguationData":[OSD([sQuery(id+"F0.wireOp",EDGE,"E22.MirrorCS")])]});
            var Q131;
            Q131=makeQuery(id+"F1.opExtrude","CAP_EDGE",EDGE,{"disambiguationData":[OSD([sQuery(id+"F0.wireOp",EDGE,"E15.MirrorCS")])],"isStart":true});
            var Q132;
            Q132=makeQuery(id+"F3.opPattern","COPY",FACE,{"derivedFrom":makeQuery(id+"F1.opExtrude","SWEPT_FACE",FACE,{"disambiguationData":[OSD([sQuery(id+"F0.wireOp",EDGE,"E20.MirrorCS")])]}),"instanceName":"4"});
            var Q133;
            Q133=makeQuery(id+"F3.opPattern","COPY",FACE,{"derivedFrom":makeQuery(id+"F1.opExtrude","SWEPT_FACE",FACE,{"disambiguationData":[OSD([sQuery(id+"F0.wireOp",EDGE,"E18.MirrorCS")])]}),"instanceName":"3"});
            var Q134;
            Q134=makeQuery(id+"F3.opPattern","COPY",FACE,{"derivedFrom":makeQuery(id+"F1.opExtrude","SWEPT_FACE",FACE,{"disambiguationData":[OSD([sQuery(id+"F0.wireOp",EDGE,"E22.MirrorCS")])]}),"instanceName":"5"});
            var Q135;
            Q135=makeQuery(id+"F3.opPattern","COPY",FACE,{"derivedFrom":makeQuery(id+"F1.opExtrude","SWEPT_FACE",FACE,{"disambiguationData":[OSD([sQuery(id+"F0.wireOp",EDGE,"E3")])]}),"instanceName":"3"});
            var Q136;
            Q136=makeQuery(id+"F3.opPattern","COPY",FACE,{"derivedFrom":makeQuery(id+"F1.opExtrude","SWEPT_FACE",FACE,{"disambiguationData":[OSD([sQuery(id+"F0.wireOp",EDGE,"E7")])]}),"instanceName":"5"});
            var Q137;
            Q137=makeQuery(id+"F1.opExtrude","CAP_EDGE",EDGE,{"disambiguationData":[OSD([sQuery(id+"F0.wireOp",EDGE,"E23.MirrorCS")])],"isStart":false});
            var Q138;
            Q138=makeQuery(id+"F1.opExtrude","SWEPT_FACE",FACE,{"disambiguationData":[OSD([sQuery(id+"F0.wireOp",EDGE,"E24.MirrorCS")])]});
            var Q139;
            Q139=makeQuery(id+"F3.opPattern","COPY",EDGE,{"derivedFrom":makeQuery(id+"F1.opExtrude","CAP_EDGE",EDGE,{"disambiguationData":[OSD([sQuery(id+"F0.wireOp",EDGE,"E19.MirrorCS")])],"isStart":false}),"instanceName":"4"});
            var Q140;
            Q140=makeQuery(id+"F3.opPattern","COPY",EDGE,{"derivedFrom":makeQuery(id+"F1.opExtrude","CAP_EDGE",EDGE,{"disambiguationData":[OSD([sQuery(id+"F0.wireOp",EDGE,"E2")])],"isStart":false}),"instanceName":"5"});
            var Q141;
            Q141=makeQuery(id+"F3.opPattern","COPY",FACE,{"derivedFrom":makeQuery(id+"F1.opExtrude","SWEPT_FACE",FACE,{"disambiguationData":[OSD([sQuery(id+"F0.wireOp",EDGE,"E3")])]}),"instanceName":"4"});
            var Q142;
            Q142=makeQuery(id+"F3.opPattern","COPY",FACE,{"derivedFrom":makeQuery(id+"F1.opExtrude","SWEPT_FACE",FACE,{"disambiguationData":[OSD([sQuery(id+"F0.wireOp",EDGE,"E20.MirrorCS")])]}),"instanceName":"5"});
            var Q143;
            Q143=makeQuery(id+"F3.opPattern","COPY",FACE,{"derivedFrom":makeQuery(id+"F1.opExtrude","SWEPT_FACE",FACE,{"disambiguationData":[OSD([sQuery(id+"F0.wireOp",EDGE,"E18.MirrorCS")])]}),"instanceName":"4"});
            var Q144;
            Q144=makeQuery(id+"F3.opPattern","COPY",EDGE,{"derivedFrom":makeQuery(id+"F1.opExtrude","CAP_EDGE",EDGE,{"disambiguationData":[OSD([sQuery(id+"F0.wireOp",EDGE,"E10")])],"isStart":false}),"instanceName":"1"});
            var Q145;
            Q145=makeQuery(id+"F3.opPattern","COPY",EDGE,{"derivedFrom":makeQuery(id+"F1.opExtrude","CAP_EDGE",EDGE,{"disambiguationData":[OSD([sQuery(id+"F0.wireOp",EDGE,"E8")])],"isStart":false}),"instanceName":"2"});
            var Q146;
            Q146=makeQuery(id+"F3.opPattern","COPY",EDGE,{"derivedFrom":makeQuery(id+"F1.opExtrude","CAP_EDGE",EDGE,{"disambiguationData":[OSD([sQuery(id+"F0.wireOp",EDGE,"E6")])],"isStart":false}),"instanceName":"3"});
            var Q147;
            Q147=makeQuery(id+"F3.opPattern","COPY",EDGE,{"derivedFrom":makeQuery(id+"F1.opExtrude","CAP_EDGE",EDGE,{"disambiguationData":[OSD([sQuery(id+"F0.wireOp",EDGE,"E23.MirrorCS")])],"isStart":false}),"instanceName":"2"});
            var Q148;
            Q148=makeQuery(id+"F3.opPattern","COPY",EDGE,{"derivedFrom":makeQuery(id+"F1.opExtrude","CAP_EDGE",EDGE,{"disambiguationData":[OSD([sQuery(id+"F0.wireOp",EDGE,"E14")])],"isStart":false}),"instanceName":"3"});
            var Q149;
            Q149=makeQuery(id+"F3.opPattern","COPY",FACE,{"derivedFrom":makeQuery(id+"F1.opExtrude","SWEPT_FACE",FACE,{"disambiguationData":[OSD([sQuery(id+"F0.wireOp",EDGE,"E2")])]}),"instanceName":"2"});
            var Q150;
            Q150=makeQuery(id+"F3.opPattern","COPY",FACE,{"derivedFrom":makeQuery(id+"F1.opExtrude","SWEPT_FACE",FACE,{"disambiguationData":[OSD([sQuery(id+"F0.wireOp",EDGE,"E4")])]}),"instanceName":"4"});
            var Q151;
            Q151=makeQuery(id+"F3.opPattern","COPY",FACE,{"derivedFrom":makeQuery(id+"F1.opExtrude","SWEPT_FACE",FACE,{"disambiguationData":[OSD([sQuery(id+"F0.wireOp",EDGE,"E17.MirrorCS")])]}),"instanceName":"3"});
            var Q152;
            Q152=makeQuery(id+"F3.opPattern","COPY",FACE,{"derivedFrom":makeQuery(id+"F1.opExtrude","SWEPT_FACE",FACE,{"disambiguationData":[OSD([sQuery(id+"F0.wireOp",EDGE,"E15.MirrorCS")])]}),"instanceName":"2"});
            var Q153;
            Q153=makeQuery(id+"F1.opExtrude","CAP_EDGE",EDGE,{"disambiguationData":[OSD([sQuery(id+"F0.wireOp",EDGE,"E16.MirrorCS")])],"isStart":false});
            var Q154;
            Q154=makeQuery(id+"F3.opPattern","COPY",EDGE,{"derivedFrom":makeQuery(id+"F1.opExtrude","CAP_EDGE",EDGE,{"disambiguationData":[OSD([sQuery(id+"F0.wireOp",EDGE,"E18.MirrorCS")])],"isStart":true}),"instanceName":"1"});
            var Q155;
            Q155=makeQuery(id+"F3.opPattern","COPY",FACE,{"derivedFrom":makeQuery(id+"F1.opExtrude","SWEPT_FACE",FACE,{"disambiguationData":[OSD([sQuery(id+"F0.wireOp",EDGE,"E19.MirrorCS")])]}),"instanceName":"4"});
            var Q156;
            Q156=makeQuery(id+"F3.opPattern","COPY",EDGE,{"derivedFrom":makeQuery(id+"F1.opExtrude","CAP_EDGE",EDGE,{"disambiguationData":[OSD([sQuery(id+"F0.wireOp",EDGE,"E20.MirrorCS")])],"isStart":true}),"instanceName":"4"});
            var Q157;
            Q157=makeQuery(id+"F1.opExtrude","SWEPT_FACE",FACE,{"disambiguationData":[OSD([sQuery(id+"F0.wireOp",EDGE,"E25.MirrorCS")])]});
            var Q158;
            Q158=makeQuery(id+"F3.opPattern","COPY",EDGE,{"derivedFrom":makeQuery(id+"F1.opExtrude","CAP_EDGE",EDGE,{"disambiguationData":[OSD([sQuery(id+"F0.wireOp",EDGE,"E11")])],"isStart":false}),"instanceName":"1"});
            var Q159;
            Q159=makeQuery(id+"F3.opPattern","COPY",EDGE,{"derivedFrom":makeQuery(id+"F1.opExtrude","CAP_EDGE",EDGE,{"disambiguationData":[OSD([sQuery(id+"F0.wireOp",EDGE,"E16.MirrorCS")])],"isStart":false}),"instanceName":"2"});
            var Q160;
            Q160=makeQuery(id+"F3.opPattern","COPY",EDGE,{"derivedFrom":makeQuery(id+"F1.opExtrude","CAP_EDGE",EDGE,{"disambiguationData":[OSD([sQuery(id+"F0.wireOp",EDGE,"E5")])],"isStart":false}),"instanceName":"4"});
            var Q161;
            Q161=makeQuery(id+"F3.opPattern","COPY",EDGE,{"derivedFrom":makeQuery(id+"F1.opExtrude","CAP_EDGE",EDGE,{"disambiguationData":[OSD([sQuery(id+"F0.wireOp",EDGE,"E22.MirrorCS")])],"isStart":false}),"instanceName":"3"});
            var Q162;
            Q162=makeQuery(id+"F3.opPattern","COPY",EDGE,{"derivedFrom":makeQuery(id+"F1.opExtrude","CAP_EDGE",EDGE,{"disambiguationData":[OSD([sQuery(id+"F0.wireOp",EDGE,"E11")])],"isStart":false}),"instanceName":"5"});
            var Q163;
            Q163=makeQuery(id+"F3.opPattern","COPY",EDGE,{"derivedFrom":makeQuery(id+"F1.opExtrude","CAP_EDGE",EDGE,{"disambiguationData":[OSD([sQuery(id+"F0.wireOp",EDGE,"E4")])],"isStart":true}),"instanceName":"1"});
            var Q164;
            Q164=makeQuery(id+"F3.opPattern","COPY",EDGE,{"derivedFrom":makeQuery(id+"F1.opExtrude","CAP_EDGE",EDGE,{"disambiguationData":[OSD([sQuery(id+"F0.wireOp",EDGE,"E8")])],"isStart":true}),"instanceName":"3"});
            var Q165;
            Q165=makeQuery(id+"F3.opPattern","COPY",EDGE,{"derivedFrom":makeQuery(id+"F1.opExtrude","CAP_EDGE",EDGE,{"disambiguationData":[OSD([sQuery(id+"F0.wireOp",EDGE,"E21.MirrorCS")])],"isStart":true}),"instanceName":"4"});
            var Q166;
            Q166=makeQuery(id+"F3.opPattern","COPY",FACE,{"derivedFrom":makeQuery(id+"F1.opExtrude","SWEPT_FACE",FACE,{"disambiguationData":[OSD([sQuery(id+"F0.wireOp",EDGE,"E15.MirrorCS")])]}),"instanceName":"1"});
            var Q167;
            Q167=makeQuery(id+"F3.opPattern","COPY",FACE,{"derivedFrom":makeQuery(id+"F1.opExtrude","SWEPT_FACE",FACE,{"disambiguationData":[OSD([sQuery(id+"F0.wireOp",EDGE,"E6")])]}),"instanceName":"4"});
            var Q168;
            Q168=makeQuery(id+"F3.opPattern","COPY",FACE,{"derivedFrom":makeQuery(id+"F1.opExtrude","SWEPT_FACE",FACE,{"disambiguationData":[OSD([sQuery(id+"F0.wireOp",EDGE,"E4")])]}),"instanceName":"3"});
            var Q169;
            Q169=makeQuery(id+"F3.opPattern","COPY",FACE,{"derivedFrom":makeQuery(id+"F1.opExtrude","SWEPT_FACE",FACE,{"disambiguationData":[OSD([sQuery(id+"F0.wireOp",EDGE,"E8")])]}),"instanceName":"5"});
            var Q170;
            Q170=makeQuery(id+"F3.opPattern","COPY",FACE,{"derivedFrom":makeQuery(id+"F1.opExtrude","SWEPT_FACE",FACE,{"disambiguationData":[OSD([sQuery(id+"F0.wireOp",EDGE,"E17.MirrorCS")])]}),"instanceName":"2"});
            var Q171;
            Q171=makeQuery(id+"F3.opPattern","COPY",FACE,{"derivedFrom":makeQuery(id+"F1.opExtrude","SWEPT_FACE",FACE,{"disambiguationData":[OSD([sQuery(id+"F0.wireOp",EDGE,"E23.MirrorCS")])]}),"instanceName":"5"});
            var Q172;
            Q172=makeQuery(id+"F3.opPattern","COPY",EDGE,{"derivedFrom":makeQuery(id+"F1.opExtrude","SWEPT_EDGE",EDGE,{"disambiguationData":[OSD([sQuery(id+"F0.wireOp",EDGE,"E19.MirrorCS"),sQuery(id+"F0.wireOp",EDGE,"E20.MirrorCS")])]}),"instanceName":"4"});
            var Q173;
            Q173=makeQuery(id+"F3.opPattern","COPY",EDGE,{"derivedFrom":makeQuery(id+"F1.opExtrude","SWEPT_EDGE",EDGE,{"disambiguationData":[OSD([sQuery(id+"F0.wireOp",EDGE,"E10"),sQuery(id+"F0.wireOp",EDGE,"E11")])]}),"instanceName":"3"});
            var Q174;
            Q174=makeQuery(id+"F3.opPattern","COPY",EDGE,{"derivedFrom":makeQuery(id+"F1.opExtrude","CAP_EDGE",EDGE,{"disambiguationData":[OSD([sQuery(id+"F0.wireOp",EDGE,"E23.MirrorCS")])],"isStart":false}),"instanceName":"3"});
            var Q175;
            Q175=makeQuery(id+"F3.opPattern","COPY",EDGE,{"derivedFrom":makeQuery(id+"F1.opExtrude","CAP_EDGE",EDGE,{"disambiguationData":[OSD([sQuery(id+"F0.wireOp",EDGE,"E14")])],"isStart":false}),"instanceName":"4"});
            var Q176;
            Q176=makeQuery(id+"F3.opPattern","COPY",EDGE,{"derivedFrom":makeQuery(id+"F1.opExtrude","CAP_EDGE",EDGE,{"disambiguationData":[OSD([sQuery(id+"F0.wireOp",EDGE,"E6")])],"isStart":false}),"instanceName":"4"});
            var Q177;
            Q177=makeQuery(id+"F3.opPattern","COPY",FACE,{"derivedFrom":makeQuery(id+"F1.opExtrude","SWEPT_FACE",FACE,{"disambiguationData":[OSD([sQuery(id+"F0.wireOp",EDGE,"E3")])]}),"instanceName":"2"});
            var Q178;
            Q178=makeQuery(id+"F3.opPattern","COPY",FACE,{"derivedFrom":makeQuery(id+"F1.opExtrude","SWEPT_FACE",FACE,{"disambiguationData":[OSD([sQuery(id+"F0.wireOp",EDGE,"E16.MirrorCS")])]}),"instanceName":"1"});
            var Q179;
            Q179=makeQuery(id+"F3.opPattern","COPY",FACE,{"derivedFrom":makeQuery(id+"F1.opExtrude","SWEPT_FACE",FACE,{"disambiguationData":[OSD([sQuery(id+"F0.wireOp",EDGE,"E7")])]}),"instanceName":"4"});
            var Q180;
            Q180=makeQuery(id+"F3.opPattern","COPY",FACE,{"derivedFrom":makeQuery(id+"F1.opExtrude","SWEPT_FACE",FACE,{"disambiguationData":[OSD([sQuery(id+"F0.wireOp",EDGE,"E5")])]}),"instanceName":"3"});
            var Q181;
            Q181=makeQuery(id+"F3.opPattern","COPY",FACE,{"derivedFrom":makeQuery(id+"F1.opExtrude","SWEPT_FACE",FACE,{"disambiguationData":[OSD([sQuery(id+"F0.wireOp",EDGE,"E18.MirrorCS")])]}),"instanceName":"2"});
            var Q182;
            Q182=makeQuery(id+"F3.opPattern","COPY",FACE,{"derivedFrom":makeQuery(id+"F1.opExtrude","SWEPT_FACE",FACE,{"disambiguationData":[OSD([sQuery(id+"F0.wireOp",EDGE,"E24.MirrorCS")])]}),"instanceName":"5"});
            var Q183;
            Q183=makeQuery(id+"F3.opPattern","COPY",FACE,{"derivedFrom":makeQuery(id+"F1.opExtrude","SWEPT_FACE",FACE,{"disambiguationData":[OSD([sQuery(id+"F0.wireOp",EDGE,"E9")])]}),"instanceName":"5"});
            var Q184;
            Q184=makeQuery(id+"F3.opPattern","COPY",EDGE,{"derivedFrom":makeQuery(id+"F1.opExtrude","CAP_EDGE",EDGE,{"disambiguationData":[OSD([sQuery(id+"F0.wireOp",EDGE,"E24.MirrorCS")])],"isStart":true}),"instanceName":"3"});
            var Q185;
            Q185=makeQuery(id+"F3.opPattern","COPY",FACE,{"derivedFrom":makeQuery(id+"F1.opExtrude","SWEPT_FACE",FACE,{"disambiguationData":[OSD([sQuery(id+"F0.wireOp",EDGE,"E4")])]}),"instanceName":"2"});
            var Q186;
            Q186=makeQuery(id+"F3.opPattern","COPY",FACE,{"derivedFrom":makeQuery(id+"F1.opExtrude","SWEPT_FACE",FACE,{"disambiguationData":[OSD([sQuery(id+"F0.wireOp",EDGE,"E17.MirrorCS")])]}),"instanceName":"1"});
            var Q187;
            Q187=makeQuery(id+"F3.opPattern","COPY",FACE,{"derivedFrom":makeQuery(id+"F1.opExtrude","SWEPT_FACE",FACE,{"disambiguationData":[OSD([sQuery(id+"F0.wireOp",EDGE,"E21.MirrorCS")])]}),"instanceName":"3"});
            var Q188;
            Q188=makeQuery(id+"F3.opPattern","COPY",FACE,{"derivedFrom":makeQuery(id+"F1.opExtrude","SWEPT_FACE",FACE,{"disambiguationData":[OSD([sQuery(id+"F0.wireOp",EDGE,"E8")])]}),"instanceName":"4"});
            var Q189;
            Q189=makeQuery(id+"F3.opPattern","COPY",FACE,{"derivedFrom":makeQuery(id+"F1.opExtrude","SWEPT_FACE",FACE,{"disambiguationData":[OSD([sQuery(id+"F0.wireOp",EDGE,"E19.MirrorCS")])]}),"instanceName":"2"});
            var Q190;
            Q190=makeQuery(id+"F3.opPattern","COPY",FACE,{"derivedFrom":makeQuery(id+"F1.opExtrude","SWEPT_FACE",FACE,{"disambiguationData":[OSD([sQuery(id+"F0.wireOp",EDGE,"E10")])]}),"instanceName":"5"});
            var Q191;
            Q191=makeQuery(id+"F3.opPattern","COPY",FACE,{"derivedFrom":makeQuery(id+"F1.opExtrude","SWEPT_FACE",FACE,{"disambiguationData":[OSD([sQuery(id+"F0.wireOp",EDGE,"E23.MirrorCS")])]}),"instanceName":"4"});
            var Q192;
            Q192=makeQuery(id+"F3.opPattern","COPY",EDGE,{"derivedFrom":makeQuery(id+"F1.opExtrude","CAP_EDGE",EDGE,{"disambiguationData":[OSD([sQuery(id+"F0.wireOp",EDGE,"E5")])],"isStart":true}),"instanceName":"1"});
            var Q193;
            Q193=makeQuery(id+"F3.opPattern","COPY",EDGE,{"derivedFrom":makeQuery(id+"F1.opExtrude","CAP_EDGE",EDGE,{"disambiguationData":[OSD([sQuery(id+"F0.wireOp",EDGE,"E16.MirrorCS")])],"isStart":false}),"instanceName":"3"});
            var Q194;
            Q194=makeQuery(id+"F3.opPattern","COPY",EDGE,{"derivedFrom":makeQuery(id+"F1.opExtrude","CAP_EDGE",EDGE,{"disambiguationData":[OSD([sQuery(id+"F0.wireOp",EDGE,"E22.MirrorCS")])],"isStart":false}),"instanceName":"4"});
            var Q195;
            Q195=makeQuery(id+"F3.opPattern","COPY",EDGE,{"derivedFrom":makeQuery(id+"F1.opExtrude","CAP_EDGE",EDGE,{"disambiguationData":[OSD([sQuery(id+"F0.wireOp",EDGE,"E20.MirrorCS")])],"isStart":false}),"instanceName":"5"});
            var Q196;
            Q196=makeQuery(id+"F3.opPattern","COPY",EDGE,{"derivedFrom":makeQuery(id+"F1.opExtrude","CAP_EDGE",EDGE,{"disambiguationData":[OSD([sQuery(id+"F0.wireOp",EDGE,"E5")])],"isStart":false}),"instanceName":"5"});
            var Q197;
            Q197=makeQuery(id+"F3.opPattern","COPY",FACE,{"derivedFrom":makeQuery(id+"F1.opExtrude","SWEPT_FACE",FACE,{"disambiguationData":[OSD([sQuery(id+"F0.wireOp",EDGE,"E5")])]}),"instanceName":"2"});
            var Q198;
            Q198=makeQuery(id+"F3.opPattern","COPY",FACE,{"derivedFrom":makeQuery(id+"F1.opExtrude","SWEPT_FACE",FACE,{"disambiguationData":[OSD([sQuery(id+"F0.wireOp",EDGE,"E9")])]}),"instanceName":"4"});
            var Q199;
            Q199=makeQuery(id+"F3.opPattern","COPY",FACE,{"derivedFrom":makeQuery(id+"F1.opExtrude","SWEPT_FACE",FACE,{"disambiguationData":[OSD([sQuery(id+"F0.wireOp",EDGE,"E7")])]}),"instanceName":"3"});
            var Q200;
            Q200=makeQuery(id+"F3.opPattern","COPY",FACE,{"derivedFrom":makeQuery(id+"F1.opExtrude","SWEPT_FACE",FACE,{"disambiguationData":[OSD([sQuery(id+"F0.wireOp",EDGE,"E20.MirrorCS")])]}),"instanceName":"2"});
            var Q201;
            Q201=makeQuery(id+"F3.opPattern","COPY",FACE,{"derivedFrom":makeQuery(id+"F1.opExtrude","SWEPT_FACE",FACE,{"disambiguationData":[OSD([sQuery(id+"F0.wireOp",EDGE,"E25.MirrorCS")])]}),"instanceName":"5"});
            var Q202;
            Q202=makeQuery(id+"F3.opPattern","COPY",EDGE,{"derivedFrom":makeQuery(id+"F1.opExtrude","CAP_EDGE",EDGE,{"disambiguationData":[OSD([sQuery(id+"F0.wireOp",EDGE,"E20.MirrorCS")])],"isStart":false}),"instanceName":"1"});
            var Q203;
            Q203=makeQuery(id+"F3.opPattern","COPY",EDGE,{"derivedFrom":makeQuery(id+"F1.opExtrude","CAP_EDGE",EDGE,{"disambiguationData":[OSD([sQuery(id+"F0.wireOp",EDGE,"E5")])],"isStart":false}),"instanceName":"1"});
            var Q204;
            Q204=makeQuery(id+"F3.opPattern","COPY",EDGE,{"derivedFrom":makeQuery(id+"F1.opExtrude","CAP_EDGE",EDGE,{"disambiguationData":[OSD([sQuery(id+"F0.wireOp",EDGE,"E11")])],"isStart":false}),"instanceName":"2"});
            var Q205;
            Q205=makeQuery(id+"F3.opPattern","COPY",EDGE,{"derivedFrom":makeQuery(id+"F1.opExtrude","CAP_EDGE",EDGE,{"disambiguationData":[OSD([sQuery(id+"F0.wireOp",EDGE,"E8")])],"isStart":true}),"instanceName":"4"});
            var Q206;
            Q206=makeQuery(id+"F3.opPattern","COPY",EDGE,{"derivedFrom":makeQuery(id+"F1.opExtrude","CAP_EDGE",EDGE,{"disambiguationData":[OSD([sQuery(id+"F0.wireOp",EDGE,"E15.MirrorCS")])],"isStart":true}),"instanceName":"4"});
            var Q207;
            Q207=makeQuery(id+"F3.opPattern","COPY",EDGE,{"derivedFrom":makeQuery(id+"F1.opExtrude","CAP_EDGE",EDGE,{"disambiguationData":[OSD([sQuery(id+"F0.wireOp",EDGE,"E21.MirrorCS")])],"isStart":true}),"instanceName":"5"});
            var Q208;
            Q208=makeQuery(id+"F3.opPattern","COPY",FACE,{"derivedFrom":makeQuery(id+"F1.opExtrude","SWEPT_FACE",FACE,{"disambiguationData":[OSD([sQuery(id+"F0.wireOp",EDGE,"E6")])]}),"instanceName":"2"});
            var Q209;
            Q209=makeQuery(id+"F3.opPattern","COPY",FACE,{"derivedFrom":makeQuery(id+"F1.opExtrude","SWEPT_FACE",FACE,{"disambiguationData":[OSD([sQuery(id+"F0.wireOp",EDGE,"E19.MirrorCS")])]}),"instanceName":"1"});
            var Q210;
            Q210=makeQuery(id+"F3.opPattern","COPY",FACE,{"derivedFrom":makeQuery(id+"F1.opExtrude","SWEPT_FACE",FACE,{"disambiguationData":[OSD([sQuery(id+"F0.wireOp",EDGE,"E10")])]}),"instanceName":"4"});
            var Q211;
            Q211=makeQuery(id+"F3.opPattern","COPY",FACE,{"derivedFrom":makeQuery(id+"F1.opExtrude","SWEPT_FACE",FACE,{"disambiguationData":[OSD([sQuery(id+"F0.wireOp",EDGE,"E21.MirrorCS")])]}),"instanceName":"2"});
            var Q212;
            Q212=makeQuery(id+"F3.opPattern","COPY",FACE,{"derivedFrom":makeQuery(id+"F1.opExtrude","SWEPT_FACE",FACE,{"disambiguationData":[OSD([sQuery(id+"F0.wireOp",EDGE,"E8")])]}),"instanceName":"3"});
            var Q213;
            Q213=makeQuery(id+"F3.opPattern","COPY",FACE,{"derivedFrom":makeQuery(id+"F1.opExtrude","SWEPT_FACE",FACE,{"disambiguationData":[OSD([sQuery(id+"F0.wireOp",EDGE,"E12")])]}),"instanceName":"5"});
            var Q214;
            Q214=makeQuery(id+"F3.opPattern","COPY",EDGE,{"derivedFrom":makeQuery(id+"F1.opExtrude","CAP_EDGE",EDGE,{"disambiguationData":[OSD([sQuery(id+"F0.wireOp",EDGE,"E12")])],"isStart":true}),"instanceName":"2"});
            var Q215;
            Q215=makeQuery(id+"F3.opPattern","COPY",EDGE,{"derivedFrom":makeQuery(id+"F1.opExtrude","CAP_EDGE",EDGE,{"disambiguationData":[OSD([sQuery(id+"F0.wireOp",EDGE,"E10")])],"isStart":true}),"instanceName":"3"});
            var Q216;
            Q216=makeQuery(id+"F3.opPattern","COPY",EDGE,{"derivedFrom":makeQuery(id+"F1.opExtrude","CAP_EDGE",EDGE,{"disambiguationData":[OSD([sQuery(id+"F0.wireOp",EDGE,"E17.MirrorCS")])],"isStart":true}),"instanceName":"3"});
            var Q217;
            Q217=makeQuery(id+"F3.opPattern","COPY",EDGE,{"derivedFrom":makeQuery(id+"F1.opExtrude","CAP_EDGE",EDGE,{"disambiguationData":[OSD([sQuery(id+"F0.wireOp",EDGE,"E14")])],"isStart":false}),"instanceName":"5"});
            var Q218;
            Q218=makeQuery(id+"F3.opPattern","COPY",EDGE,{"derivedFrom":makeQuery(id+"F1.opExtrude","CAP_EDGE",EDGE,{"disambiguationData":[OSD([sQuery(id+"F0.wireOp",EDGE,"E6")])],"isStart":false}),"instanceName":"5"});
            var Q219;
            Q219=makeQuery(id+"F3.opPattern","COPY",FACE,{"derivedFrom":makeQuery(id+"F1.opExtrude","SWEPT_FACE",FACE,{"disambiguationData":[OSD([sQuery(id+"F0.wireOp",EDGE,"E7")])]}),"instanceName":"2"});
            var Q220;
            Q220=makeQuery(id+"F3.opPattern","COPY",FACE,{"derivedFrom":makeQuery(id+"F1.opExtrude","SWEPT_FACE",FACE,{"disambiguationData":[OSD([sQuery(id+"F0.wireOp",EDGE,"E20.MirrorCS")])]}),"instanceName":"1"});
            var Q221;
            Q221=makeQuery(id+"F3.opPattern","COPY",FACE,{"derivedFrom":makeQuery(id+"F1.opExtrude","SWEPT_FACE",FACE,{"disambiguationData":[OSD([sQuery(id+"F0.wireOp",EDGE,"E9")])]}),"instanceName":"3"});
            var Q222;
            Q222=makeQuery(id+"F3.opPattern","COPY",FACE,{"derivedFrom":makeQuery(id+"F1.opExtrude","SWEPT_FACE",FACE,{"disambiguationData":[OSD([sQuery(id+"F0.wireOp",EDGE,"E13")])]}),"instanceName":"5"});
            var Q223;
            Q223=makeQuery(id+"F3.opPattern","COPY",FACE,{"derivedFrom":makeQuery(id+"F1.opExtrude","SWEPT_FACE",FACE,{"disambiguationData":[OSD([sQuery(id+"F0.wireOp",EDGE,"E22.MirrorCS")])]}),"instanceName":"2"});
            var Q224;
            Q224=makeQuery(id+"F3.opPattern","COPY",FACE,{"derivedFrom":makeQuery(id+"F1.opExtrude","SWEPT_FACE",FACE,{"disambiguationData":[OSD([sQuery(id+"F0.wireOp",EDGE,"E25.MirrorCS")])]}),"instanceName":"4"});
            var Q225;
            Q225=makeQuery(id+"F3.opPattern","COPY",EDGE,{"derivedFrom":makeQuery(id+"F1.opExtrude","SWEPT_EDGE",EDGE,{"disambiguationData":[OSD([sQuery(id+"F0.wireOp",EDGE,"E2"),sQuery(id+"F0.wireOp",EDGE,"E3")])]}),"instanceName":"2"});
            var Q226;
            Q226=makeQuery(id+"F3.opPattern","COPY",EDGE,{"derivedFrom":makeQuery(id+"F1.opExtrude","CAP_EDGE",EDGE,{"disambiguationData":[OSD([sQuery(id+"F0.wireOp",EDGE,"E6")])],"isStart":false}),"instanceName":"1"});
            var Q227;
            Q227=makeQuery(id+"F3.opPattern","COPY",EDGE,{"derivedFrom":makeQuery(id+"F1.opExtrude","CAP_EDGE",EDGE,{"disambiguationData":[OSD([sQuery(id+"F0.wireOp",EDGE,"E10")])],"isStart":false}),"instanceName":"3"});
            var Q228;
            Q228=makeQuery(id+"F3.opPattern","COPY",EDGE,{"derivedFrom":makeQuery(id+"F1.opExtrude","CAP_EDGE",EDGE,{"disambiguationData":[OSD([sQuery(id+"F0.wireOp",EDGE,"E15.MirrorCS")])],"isStart":false}),"instanceName":"4"});
            var Q229;
            Q229=makeQuery(id+"F3.opPattern","COPY",EDGE,{"derivedFrom":makeQuery(id+"F1.opExtrude","CAP_EDGE",EDGE,{"disambiguationData":[OSD([sQuery(id+"F0.wireOp",EDGE,"E23.MirrorCS")])],"isStart":false}),"instanceName":"4"});
            var Q230;
            Q230=makeQuery(id+"F3.opPattern","COPY",EDGE,{"derivedFrom":makeQuery(id+"F1.opExtrude","CAP_EDGE",EDGE,{"disambiguationData":[OSD([sQuery(id+"F0.wireOp",EDGE,"E13")])],"isStart":true}),"instanceName":"2"});
            var Q231;
            Q231=makeQuery(id+"F3.opPattern","COPY",EDGE,{"derivedFrom":makeQuery(id+"F1.opExtrude","CAP_EDGE",EDGE,{"disambiguationData":[OSD([sQuery(id+"F0.wireOp",EDGE,"E18.MirrorCS")])],"isStart":true}),"instanceName":"3"});
            var Q232;
            Q232=makeQuery(id+"F3.opPattern","COPY",EDGE,{"derivedFrom":makeQuery(id+"F1.opExtrude","CAP_EDGE",EDGE,{"disambiguationData":[OSD([sQuery(id+"F0.wireOp",EDGE,"E25.MirrorCS")])],"isStart":true}),"instanceName":"3"});
            var Q233;
            Q233=makeQuery(id+"F3.opPattern","COPY",EDGE,{"derivedFrom":makeQuery(id+"F1.opExtrude","CAP_EDGE",EDGE,{"disambiguationData":[OSD([sQuery(id+"F0.wireOp",EDGE,"E24.MirrorCS")])],"isStart":true}),"instanceName":"4"});
            var Q234;
            Q234=makeQuery(id+"F3.opPattern","COPY",EDGE,{"derivedFrom":makeQuery(id+"F1.opExtrude","CAP_EDGE",EDGE,{"disambiguationData":[OSD([sQuery(id+"F0.wireOp",EDGE,"E9")])],"isStart":true}),"instanceName":"4"});
            var Q235;
            Q235=makeQuery(id+"F3.opPattern","COPY",EDGE,{"derivedFrom":makeQuery(id+"F1.opExtrude","CAP_EDGE",EDGE,{"disambiguationData":[OSD([sQuery(id+"F0.wireOp",EDGE,"E22.MirrorCS")])],"isStart":true}),"instanceName":"5"});
            var Q236;
            Q236=makeQuery(id+"F3.opPattern","COPY",FACE,{"derivedFrom":makeQuery(id+"F1.opExtrude","SWEPT_FACE",FACE,{"disambiguationData":[OSD([sQuery(id+"F0.wireOp",EDGE,"E10")])]}),"instanceName":"3"});
            var Q237;
            Q237=makeQuery(id+"F3.opPattern","COPY",FACE,{"derivedFrom":makeQuery(id+"F1.opExtrude","SWEPT_FACE",FACE,{"disambiguationData":[OSD([sQuery(id+"F0.wireOp",EDGE,"E23.MirrorCS")])]}),"instanceName":"2"});
            var Q238;
            Q238=makeQuery(id+"F3.opPattern","COPY",FACE,{"derivedFrom":makeQuery(id+"F1.opExtrude","SWEPT_FACE",FACE,{"disambiguationData":[OSD([sQuery(id+"F0.wireOp",EDGE,"E21.MirrorCS")])]}),"instanceName":"1"});
            var Q239;
            Q239=makeQuery(id+"F3.opPattern","COPY",FACE,{"derivedFrom":makeQuery(id+"F1.opExtrude","SWEPT_FACE",FACE,{"disambiguationData":[OSD([sQuery(id+"F0.wireOp",EDGE,"E12")])]}),"instanceName":"4"});
            var Q240;
            Q240=makeQuery(id+"F3.opPattern","COPY",FACE,{"derivedFrom":makeQuery(id+"F1.opExtrude","SWEPT_FACE",FACE,{"disambiguationData":[OSD([sQuery(id+"F0.wireOp",EDGE,"E13")])]}),"instanceName":"4"});
            var Q241;
            Q241=makeQuery(id+"F3.opPattern","COPY",EDGE,{"derivedFrom":makeQuery(id+"F1.opExtrude","CAP_EDGE",EDGE,{"disambiguationData":[OSD([sQuery(id+"F0.wireOp",EDGE,"E22.MirrorCS")])],"isStart":false}),"instanceName":"1"});
            var Q242;
            Q242=makeQuery(id+"F3.opPattern","COPY",EDGE,{"derivedFrom":makeQuery(id+"F1.opExtrude","CAP_EDGE",EDGE,{"disambiguationData":[OSD([sQuery(id+"F0.wireOp",EDGE,"E20.MirrorCS")])],"isStart":false}),"instanceName":"2"});
            var Q243;
            Q243=makeQuery(id+"F3.opPattern","COPY",EDGE,{"derivedFrom":makeQuery(id+"F1.opExtrude","CAP_EDGE",EDGE,{"disambiguationData":[OSD([sQuery(id+"F0.wireOp",EDGE,"E11")])],"isStart":false}),"instanceName":"3"});
            var Q244;
            Q244=makeQuery(id+"F3.opPattern","COPY",EDGE,{"derivedFrom":makeQuery(id+"F1.opExtrude","CAP_EDGE",EDGE,{"disambiguationData":[OSD([sQuery(id+"F0.wireOp",EDGE,"E16.MirrorCS")])],"isStart":false}),"instanceName":"4"});
            var Q245;
            Q245=makeQuery(id+"F3.opPattern","COPY",EDGE,{"derivedFrom":makeQuery(id+"F1.opExtrude","CAP_EDGE",EDGE,{"disambiguationData":[OSD([sQuery(id+"F0.wireOp",EDGE,"E22.MirrorCS")])],"isStart":false}),"instanceName":"5"});
            var Q246;
            Q246=makeQuery(id+"F3.opPattern","COPY",FACE,{"derivedFrom":makeQuery(id+"F1.opExtrude","SWEPT_FACE",FACE,{"disambiguationData":[OSD([sQuery(id+"F0.wireOp",EDGE,"E11")])]}),"instanceName":"3"});
            var Q247;
            Q247=makeQuery(id+"F3.opPattern","COPY",FACE,{"derivedFrom":makeQuery(id+"F1.opExtrude","SWEPT_FACE",FACE,{"disambiguationData":[OSD([sQuery(id+"F0.wireOp",EDGE,"E24.MirrorCS")])]}),"instanceName":"2"});
            var Q248;
            Q248=makeQuery(id+"F3.opPattern","COPY",FACE,{"derivedFrom":makeQuery(id+"F1.opExtrude","SWEPT_FACE",FACE,{"disambiguationData":[OSD([sQuery(id+"F0.wireOp",EDGE,"E9")])]}),"instanceName":"2"});
            var Q249;
            Q249=makeQuery(id+"F3.opPattern","COPY",EDGE,{"derivedFrom":makeQuery(id+"F1.opExtrude","CAP_EDGE",EDGE,{"disambiguationData":[OSD([sQuery(id+"F0.wireOp",EDGE,"b2b48e4d-2c92-4a1f-81ad-3469f6dd68cb")])],"isStart":false}),"instanceName":"4"});
            var Q250;
            Q250=makeQuery(id+"F3.opPattern","COPY",EDGE,{"derivedFrom":makeQuery(id+"F1.opExtrude","CAP_EDGE",EDGE,{"disambiguationData":[OSD([sQuery(id+"F0.wireOp",EDGE,"E15.MirrorCS")])],"isStart":true}),"instanceName":"1"});
            var Q251;
            Q251=makeQuery(id+"F3.opPattern","COPY",EDGE,{"derivedFrom":makeQuery(id+"F1.opExtrude","CAP_EDGE",EDGE,{"disambiguationData":[OSD([sQuery(id+"F0.wireOp",EDGE,"E8")])],"isStart":true}),"instanceName":"1"});
            var Q252;
            Q252=makeQuery(id+"F3.opPattern","COPY",EDGE,{"derivedFrom":makeQuery(id+"F1.opExtrude","CAP_EDGE",EDGE,{"disambiguationData":[OSD([sQuery(id+"F0.wireOp",EDGE,"E12")])],"isStart":true}),"instanceName":"3"});
            var Q253;
            Q253=makeQuery(id+"F3.opPattern","COPY",FACE,{"derivedFrom":makeQuery(id+"F1.opExtrude","SWEPT_FACE",FACE,{"disambiguationData":[OSD([sQuery(id+"F0.wireOp",EDGE,"E10")])]}),"instanceName":"2"});
            var Q254;
            Q254=makeQuery(id+"F3.opPattern","COPY",FACE,{"derivedFrom":makeQuery(id+"F1.opExtrude","SWEPT_FACE",FACE,{"disambiguationData":[OSD([sQuery(id+"F0.wireOp",EDGE,"E23.MirrorCS")])]}),"instanceName":"1"});
            var Q255;
            Q255=makeQuery(id+"F3.opPattern","COPY",FACE,{"derivedFrom":makeQuery(id+"F1.opExtrude","SWEPT_FACE",FACE,{"disambiguationData":[OSD([sQuery(id+"F0.wireOp",EDGE,"E2")])]}),"instanceName":"5"});
            var Q256;
            Q256=makeQuery(id+"F3.opPattern","COPY",FACE,{"derivedFrom":makeQuery(id+"F1.opExtrude","SWEPT_FACE",FACE,{"disambiguationData":[OSD([sQuery(id+"F0.wireOp",EDGE,"E14")])]}),"instanceName":"4"});
            var Q257;
            Q257=makeQuery(id+"F3.opPattern","COPY",EDGE,{"derivedFrom":makeQuery(id+"F1.opExtrude","SWEPT_EDGE",EDGE,{"disambiguationData":[OSD([sQuery(id+"F0.wireOp",EDGE,"E160.MirrorCS"),sQuery(id+"F0.wireOp",EDGE,"E25.MirrorCS")])]}),"instanceName":"1"});
            var Q258;
            Q258=makeQuery(id+"F3.opPattern","COPY",EDGE,{"derivedFrom":makeQuery(id+"F1.opExtrude","CAP_EDGE",EDGE,{"disambiguationData":[OSD([sQuery(id+"F0.wireOp",EDGE,"E6")])],"isStart":false}),"instanceName":"2"});
            var Q259;
            Q259=makeQuery(id+"F3.opPattern","COPY",EDGE,{"derivedFrom":makeQuery(id+"F1.opExtrude","CAP_EDGE",EDGE,{"disambiguationData":[OSD([sQuery(id+"F0.wireOp",EDGE,"E23.MirrorCS")])],"isStart":false}),"instanceName":"1"});
            var Q260;
            Q260=makeQuery(id+"F3.opPattern","COPY",EDGE,{"derivedFrom":makeQuery(id+"F1.opExtrude","CAP_EDGE",EDGE,{"disambiguationData":[OSD([sQuery(id+"F0.wireOp",EDGE,"E14")])],"isStart":false}),"instanceName":"2"});
            var Q261;
            Q261=makeQuery(id+"F3.opPattern","COPY",EDGE,{"derivedFrom":makeQuery(id+"F1.opExtrude","CAP_EDGE",EDGE,{"disambiguationData":[OSD([sQuery(id+"F0.wireOp",EDGE,"E19.MirrorCS")])],"isStart":false}),"instanceName":"3"});
            var Q262;
            Q262=makeQuery(id+"F3.opPattern","COPY",EDGE,{"derivedFrom":makeQuery(id+"F1.opExtrude","CAP_EDGE",EDGE,{"disambiguationData":[OSD([sQuery(id+"F0.wireOp",EDGE,"E8")])],"isStart":false}),"instanceName":"5"});
            var Q263;
            Q263=makeQuery(id+"F3.opPattern","COPY",EDGE,{"derivedFrom":makeQuery(id+"F1.opExtrude","CAP_EDGE",EDGE,{"disambiguationData":[OSD([sQuery(id+"F0.wireOp",EDGE,"E23.MirrorCS")])],"isStart":false}),"instanceName":"5"});
            var Q264;
            Q264=makeQuery(id+"F3.opPattern","COPY",FACE,{"derivedFrom":makeQuery(id+"F1.opExtrude","SWEPT_FACE",FACE,{"disambiguationData":[OSD([sQuery(id+"F0.wireOp",EDGE,"E25.MirrorCS")])]}),"instanceName":"2"});
            var Q265;
            Q265=makeQuery(id+"F3.opPattern","COPY",EDGE,{"derivedFrom":makeQuery(id+"F1.opExtrude","CAP_EDGE",EDGE,{"disambiguationData":[OSD([sQuery(id+"F0.wireOp",EDGE,"E15.MirrorCS")])],"isStart":false}),"instanceName":"5"});
            var Q266;
            Q266=makeQuery(id+"F3.opPattern","COPY",FACE,{"derivedFrom":makeQuery(id+"F1.opExtrude","SWEPT_FACE",FACE,{"disambiguationData":[OSD([sQuery(id+"F0.wireOp",EDGE,"E24.MirrorCS")])]}),"instanceName":"1"});
            var Q267;
            Q267=makeQuery(id+"F3.opPattern","COPY",FACE,{"derivedFrom":makeQuery(id+"F1.opExtrude","SWEPT_FACE",FACE,{"disambiguationData":[OSD([sQuery(id+"F0.wireOp",EDGE,"E11")])]}),"instanceName":"2"});
            var Q268;
            Q268=makeQuery(id+"F3.opPattern","COPY",EDGE,{"derivedFrom":makeQuery(id+"F1.opExtrude","CAP_EDGE",EDGE,{"disambiguationData":[OSD([sQuery(id+"F0.wireOp",EDGE,"E9")])],"isStart":true}),"instanceName":"1"});
            var Q269;
            Q269=makeQuery(id+"F3.opPattern","COPY",EDGE,{"derivedFrom":makeQuery(id+"F1.opExtrude","CAP_EDGE",EDGE,{"disambiguationData":[OSD([sQuery(id+"F0.wireOp",EDGE,"E3")])],"isStart":true}),"instanceName":"4"});
            var Q270;
            Q270=makeQuery(id+"F3.opPattern","COPY",FACE,{"derivedFrom":makeQuery(id+"F1.opExtrude","SWEPT_FACE",FACE,{"disambiguationData":[OSD([sQuery(id+"F0.wireOp",EDGE,"E14")])]}),"instanceName":"3"});
            var Q271;
            Q271=makeQuery(id+"F3.opPattern","COPY",FACE,{"derivedFrom":makeQuery(id+"F1.opExtrude","SWEPT_FACE",FACE,{"disambiguationData":[OSD([sQuery(id+"F0.wireOp",EDGE,"E17.MirrorCS")])]}),"instanceName":"5"});
            var Q272;
            Q272=makeQuery(id+"F3.opPattern","COPY",FACE,{"derivedFrom":makeQuery(id+"F1.opExtrude","SWEPT_FACE",FACE,{"disambiguationData":[OSD([sQuery(id+"F0.wireOp",EDGE,"E2")])]}),"instanceName":"4"});
            var Q273;
            Q273=makeQuery(id+"F3.opPattern","COPY",EDGE,{"derivedFrom":makeQuery(id+"F1.opExtrude","CAP_EDGE",EDGE,{"disambiguationData":[OSD([sQuery(id+"F0.wireOp",EDGE,"E16.MirrorCS")])],"isStart":false}),"instanceName":"1"});
            var Q274;
            Q274=makeQuery(id+"F3.opPattern","COPY",EDGE,{"derivedFrom":makeQuery(id+"F1.opExtrude","CAP_EDGE",EDGE,{"disambiguationData":[OSD([sQuery(id+"F0.wireOp",EDGE,"E22.MirrorCS")])],"isStart":false}),"instanceName":"2"});
            var Q275;
            Q275=makeQuery(id+"F3.opPattern","COPY",EDGE,{"derivedFrom":makeQuery(id+"F1.opExtrude","CAP_EDGE",EDGE,{"disambiguationData":[OSD([sQuery(id+"F0.wireOp",EDGE,"E20.MirrorCS")])],"isStart":false}),"instanceName":"3"});
            var Q276;
            Q276=makeQuery(id+"F3.opPattern","COPY",EDGE,{"derivedFrom":makeQuery(id+"F1.opExtrude","CAP_EDGE",EDGE,{"disambiguationData":[OSD([sQuery(id+"F0.wireOp",EDGE,"E13")])],"isStart":false}),"instanceName":"3"});
            var Q277;
            Q277=makeQuery(id+"F3.opPattern","COPY",EDGE,{"derivedFrom":makeQuery(id+"F1.opExtrude","CAP_EDGE",EDGE,{"disambiguationData":[OSD([sQuery(id+"F0.wireOp",EDGE,"E5")])],"isStart":false}),"instanceName":"3"});
            var Q278;
            Q278=makeQuery(id+"F3.opPattern","COPY",EDGE,{"derivedFrom":makeQuery(id+"F1.opExtrude","CAP_EDGE",EDGE,{"disambiguationData":[OSD([sQuery(id+"F0.wireOp",EDGE,"E11")])],"isStart":false}),"instanceName":"4"});
            var Q279;
            Q279=makeQuery(id+"F3.opPattern","COPY",EDGE,{"derivedFrom":makeQuery(id+"F1.opExtrude","CAP_EDGE",EDGE,{"disambiguationData":[OSD([sQuery(id+"F0.wireOp",EDGE,"E16.MirrorCS")])],"isStart":false}),"instanceName":"5"});
            var Q280;
            Q280=makeQuery(id+"F3.opPattern","COPY",FACE,{"derivedFrom":makeQuery(id+"F1.opExtrude","SWEPT_FACE",FACE,{"disambiguationData":[OSD([sQuery(id+"F0.wireOp",EDGE,"E18.MirrorCS")])]}),"instanceName":"5"});
            var Q281;
            Q281=makeQuery(id+"F3.opPattern","COPY",FACE,{"derivedFrom":makeQuery(id+"F1.opExtrude","SWEPT_FACE",FACE,{"disambiguationData":[OSD([sQuery(id+"F0.wireOp",EDGE,"E25.MirrorCS")])]}),"instanceName":"1"});
            var Q282;
            Q282=makeQuery(id+"F3.opPattern","COPY",EDGE,{"derivedFrom":makeQuery(id+"F1.opExtrude","CAP_EDGE",EDGE,{"disambiguationData":[OSD([sQuery(id+"F0.wireOp",EDGE,"b2b48e4d-2c92-4a1f-81ad-3469f6dd68cb")])],"isStart":false}),"instanceName":"5"});
            var Q283;
            Q283=makeQuery(id+"F3.opPattern","COPY",FACE,{"derivedFrom":makeQuery(id+"F1.opExtrude","SWEPT_FACE",FACE,{"disambiguationData":[OSD([sQuery(id+"F0.wireOp",EDGE,"E3")])]}),"instanceName":"5"});
            var Q284;
            Q284=makeQuery(id+"F3.opPattern","COPY",FACE,{"derivedFrom":makeQuery(id+"F1.opExtrude","SWEPT_FACE",FACE,{"disambiguationData":[OSD([sQuery(id+"F0.wireOp",EDGE,"E16.MirrorCS")])]}),"instanceName":"4"});
            var Q285;
            Q285=makeQuery(id+"F3.opPattern","COPY",EDGE,{"derivedFrom":makeQuery(id+"F1.opExtrude","CAP_EDGE",EDGE,{"disambiguationData":[OSD([sQuery(id+"F0.wireOp",EDGE,"E2")])],"isStart":true}),"instanceName":"1"});
            var Q286;
            Q286=makeQuery(id+"F3.opPattern","COPY",EDGE,{"derivedFrom":makeQuery(id+"F1.opExtrude","SWEPT_EDGE",EDGE,{"disambiguationData":[OSD([sQuery(id+"F0.wireOp",EDGE,"E5"),sQuery(id+"F0.wireOp",EDGE,"E6")])]}),"instanceName":"3"});
            var Q287;
            Q287=makeQuery(id+"F3.opPattern","COPY",EDGE,{"derivedFrom":makeQuery(id+"F1.opExtrude","CAP_EDGE",EDGE,{"disambiguationData":[OSD([sQuery(id+"F0.wireOp",EDGE,"E21.MirrorCS")])],"isStart":true}),"instanceName":"3"});
            var Q288;
            Q288=makeQuery(id+"F3.opPattern","COPY",EDGE,{"derivedFrom":makeQuery(id+"F1.opExtrude","CAP_EDGE",EDGE,{"disambiguationData":[OSD([sQuery(id+"F0.wireOp",EDGE,"E4")])],"isStart":true}),"instanceName":"4"});
            var Q289;
            Q289=makeQuery(id+"F3.opPattern","COPY",FACE,{"derivedFrom":makeQuery(id+"F1.opExtrude","SWEPT_FACE",FACE,{"disambiguationData":[OSD([sQuery(id+"F0.wireOp",EDGE,"E15.MirrorCS")])]}),"instanceName":"3"});
            var Q290;
            Q290=makeQuery(id+"F3.opPattern","COPY",FACE,{"derivedFrom":makeQuery(id+"F1.opExtrude","SWEPT_FACE",FACE,{"disambiguationData":[OSD([sQuery(id+"F0.wireOp",EDGE,"E19.MirrorCS")])]}),"instanceName":"5"});
            var Q291;
            Q291=makeQuery(id+"F3.opPattern","COPY",FACE,{"derivedFrom":makeQuery(id+"F1.opExtrude","SWEPT_FACE",FACE,{"disambiguationData":[OSD([sQuery(id+"F0.wireOp",EDGE,"E2")])]}),"instanceName":"3"});
            var Q292;
            Q292=makeQuery(id+"F3.opPattern","COPY",FACE,{"derivedFrom":makeQuery(id+"F1.opExtrude","SWEPT_FACE",FACE,{"disambiguationData":[OSD([sQuery(id+"F0.wireOp",EDGE,"E17.MirrorCS")])]}),"instanceName":"4"});
            var Q293;
            Q293=makeQuery(id+"F3.opPattern","COPY",FACE,{"derivedFrom":makeQuery(id+"F1.opExtrude","SWEPT_FACE",FACE,{"disambiguationData":[OSD([sQuery(id+"F0.wireOp",EDGE,"E4")])]}),"instanceName":"5"});
            var Q294;
            Q294=makeQuery(id+"F1.opExtrude","SWEPT_FACE",FACE,{"disambiguationData":[OSD([sQuery(id+"F0.wireOp",EDGE,"E13")])]});
            var Q295;
            Q295=makeQuery(id+"F1.opExtrude","SWEPT_FACE",FACE,{"disambiguationData":[OSD([sQuery(id+"F0.wireOp",EDGE,"E14")])]});
            var Q296;
            Q296=makeQuery(id+"F1.opExtrude","SWEPT_FACE",FACE,{"disambiguationData":[OSD([sQuery(id+"F0.wireOp",EDGE,"E2")])]});
            var Q297;
            Q297=makeQuery(id+"F1.opExtrude","SWEPT_FACE",FACE,{"disambiguationData":[OSD([sQuery(id+"F0.wireOp",EDGE,"E3")])]});
            var Q298;
            Q298=makeQuery(id+"F1.opExtrude","SWEPT_FACE",FACE,{"disambiguationData":[OSD([sQuery(id+"F0.wireOp",EDGE,"E5")])]});
            var Q299;
            Q299=makeQuery(id+"F1.opExtrude","SWEPT_FACE",FACE,{"disambiguationData":[OSD([sQuery(id+"F0.wireOp",EDGE,"E7")])]});
            var Q300;
            Q300=makeQuery(id+"F1.opExtrude","SWEPT_FACE",FACE,{"disambiguationData":[OSD([sQuery(id+"F0.wireOp",EDGE,"E8")])]});
            var Q301;
            Q301=makeQuery(id+"F1.opExtrude","SWEPT_FACE",FACE,{"disambiguationData":[OSD([sQuery(id+"F0.wireOp",EDGE,"E9")])]});
            var Q302;
            Q302=makeQuery(id+"F1.opExtrude","SWEPT_EDGE",EDGE,{"disambiguationData":[OSD([sQuery(id+"F0.wireOp",EDGE,"E10"),sQuery(id+"F0.wireOp",EDGE,"E11")])]});
            var Q303;
            Q303=makeQuery(id+"F3.opPattern","COPY",FACE,{"derivedFrom":makeQuery(id+"F1.opExtrude","SWEPT_FACE",FACE,{"disambiguationData":[OSD([sQuery(id+"F0.wireOp",EDGE,"E13")])]}),"instanceName":"1"});
            var Q304;
            Q304=makeQuery(id+"F1.opExtrude","SWEPT_FACE",FACE,{"disambiguationData":[OSD([sQuery(id+"F0.wireOp",EDGE,"E10")])]});
            var Q305;
            Q305=makeQuery(id+"F1.opExtrude","SWEPT_FACE",FACE,{"disambiguationData":[OSD([sQuery(id+"F0.wireOp",EDGE,"E11")])]});
            var Q306;
            Q306=makeQuery(id+"F3.opPattern","COPY",FACE,{"derivedFrom":makeQuery(id+"F1.opExtrude","SWEPT_FACE",FACE,{"disambiguationData":[OSD([sQuery(id+"F0.wireOp",EDGE,"E14")])]}),"instanceName":"1"});
            var Q307;
            Q307=makeQuery(id+"F1.opExtrude","SWEPT_FACE",FACE,{"disambiguationData":[OSD([sQuery(id+"F0.wireOp",EDGE,"E12")])]});
            var Q308;
            Q308=makeQuery(id+"F3.opPattern","COPY",FACE,{"derivedFrom":makeQuery(id+"F1.opExtrude","SWEPT_FACE",FACE,{"disambiguationData":[OSD([sQuery(id+"F0.wireOp",EDGE,"E2")])]}),"instanceName":"1"});
            var Q309;
            Q309=makeQuery(id+"F3.opPattern","COPY",FACE,{"derivedFrom":makeQuery(id+"F1.opExtrude","SWEPT_FACE",FACE,{"disambiguationData":[OSD([sQuery(id+"F0.wireOp",EDGE,"E3")])]}),"instanceName":"1"});
            var Q310;
            Q310=makeQuery(id+"F3.opPattern","COPY",FACE,{"derivedFrom":makeQuery(id+"F1.opExtrude","SWEPT_FACE",FACE,{"disambiguationData":[OSD([sQuery(id+"F0.wireOp",EDGE,"E160.MirrorCS")])]}),"instanceName":"5"});
            var Q311;
            Q311=makeQuery(id+"F3.opPattern","COPY",EDGE,{"derivedFrom":makeQuery(id+"F1.opExtrude","CAP_EDGE",EDGE,{"disambiguationData":[OSD([sQuery(id+"F0.wireOp",EDGE,"b2b48e4d-2c92-4a1f-81ad-3469f6dd68cb")])],"isStart":false}),"instanceName":"3"});
            var Q312;
            Q312=makeQuery(id+"F3.opPattern","COPY",FACE,{"derivedFrom":makeQuery(id+"F1.opExtrude","SWEPT_FACE",FACE,{"disambiguationData":[OSD([sQuery(id+"F0.wireOp",EDGE,"E4")])]}),"instanceName":"1"});
            var Q313;
            Q313=makeQuery(id+"F3.opPattern","COPY",EDGE,{"derivedFrom":makeQuery(id+"F1.opExtrude","CAP_EDGE",EDGE,{"disambiguationData":[OSD([sQuery(id+"F0.wireOp",EDGE,"E160.MirrorCS")])],"isStart":true}),"instanceName":"3"});
            var Q314;
            Q314=makeQuery(id+"F3.opPattern","COPY",FACE,{"derivedFrom":makeQuery(id+"F1.opExtrude","SWEPT_FACE",FACE,{"disambiguationData":[OSD([sQuery(id+"F0.wireOp",EDGE,"E6")])]}),"instanceName":"1"});
            var Q315;
            Q315=makeQuery(id+"F3.opPattern","COPY",FACE,{"derivedFrom":makeQuery(id+"F1.opExtrude","SWEPT_FACE",FACE,{"disambiguationData":[OSD([sQuery(id+"F0.wireOp",EDGE,"E7")])]}),"instanceName":"1"});
            var Q316;
            Q316=makeQuery(id+"F3.opPattern","COPY",EDGE,{"derivedFrom":makeQuery(id+"F1.opExtrude","SWEPT_EDGE",EDGE,{"disambiguationData":[OSD([sQuery(id+"F0.wireOp",EDGE,"E8"),sQuery(id+"F0.wireOp",EDGE,"E9")])]}),"instanceName":"1"});
            var Q317;
            Q317=makeQuery(id+"F1.opExtrude","SWEPT_FACE",FACE,{"disambiguationData":[OSD([sQuery(id+"F0.wireOp",EDGE,"b2b48e4d-2c92-4a1f-81ad-3469f6dd68cb")])]});
            var Q318;
            Q318=makeQuery(id+"F3.opPattern","COPY",FACE,{"derivedFrom":makeQuery(id+"F1.opExtrude","SWEPT_FACE",FACE,{"disambiguationData":[OSD([sQuery(id+"F0.wireOp",EDGE,"E9")])]}),"instanceName":"1"});
            var Q319;
            Q319=makeQuery(id+"F1.opExtrude","SWEPT_FACE",FACE,{"disambiguationData":[OSD([sQuery(id+"F0.wireOp",EDGE,"E160.MirrorCS")])]});
            var Q320;
            Q320=makeQuery(id+"F3.opPattern","COPY",FACE,{"derivedFrom":makeQuery(id+"F1.opExtrude","SWEPT_FACE",FACE,{"disambiguationData":[OSD([sQuery(id+"F0.wireOp",EDGE,"E10")])]}),"instanceName":"1"});
            var Q321;
            Q321=makeQuery(id+"F3.opPattern","COPY",FACE,{"derivedFrom":makeQuery(id+"F1.opExtrude","SWEPT_FACE",FACE,{"disambiguationData":[OSD([sQuery(id+"F0.wireOp",EDGE,"E11")])]}),"instanceName":"1"});
            var Q322;
            Q322=makeQuery(id+"F3.opPattern","COPY",FACE,{"derivedFrom":makeQuery(id+"F1.opExtrude","SWEPT_FACE",FACE,{"disambiguationData":[OSD([sQuery(id+"F0.wireOp",EDGE,"b2b48e4d-2c92-4a1f-81ad-3469f6dd68cb")])]}),"instanceName":"1"});
            var Q323;
            Q323=makeQuery(id+"F3.opPattern","COPY",EDGE,{"derivedFrom":makeQuery(id+"F1.opExtrude","CAP_EDGE",EDGE,{"disambiguationData":[OSD([sQuery(id+"F0.wireOp",EDGE,"b2b48e4d-2c92-4a1f-81ad-3469f6dd68cb")])],"isStart":false}),"instanceName":"1"});
            var Q324;
            Q324=makeQuery(id+"F3.opPattern","COPY",FACE,{"derivedFrom":makeQuery(id+"F1.opExtrude","SWEPT_FACE",FACE,{"disambiguationData":[OSD([sQuery(id+"F0.wireOp",EDGE,"E160.MirrorCS")])]}),"instanceName":"1"});
            var Q325;
            Q325=makeQuery(id+"F3.opPattern","COPY",EDGE,{"derivedFrom":makeQuery(id+"F1.opExtrude","CAP_EDGE",EDGE,{"disambiguationData":[OSD([sQuery(id+"F0.wireOp",EDGE,"E160.MirrorCS")])],"isStart":true}),"instanceName":"1"});
            var Q326;
            Q326=makeQuery(id+"F3.opPattern","COPY",FACE,{"derivedFrom":makeQuery(id+"F1.opExtrude","SWEPT_FACE",FACE,{"disambiguationData":[OSD([sQuery(id+"F0.wireOp",EDGE,"E12")])]}),"instanceName":"1"});
            var Q327;
            Q327=makeQuery(id+"F3.opPattern","COPY",FACE,{"derivedFrom":makeQuery(id+"F1.opExtrude","SWEPT_FACE",FACE,{"disambiguationData":[OSD([sQuery(id+"F0.wireOp",EDGE,"b2b48e4d-2c92-4a1f-81ad-3469f6dd68cb")])]}),"instanceName":"2"});
            var Q328;
            Q328=makeQuery(id+"F3.opPattern","COPY",FACE,{"derivedFrom":makeQuery(id+"F1.opExtrude","SWEPT_FACE",FACE,{"disambiguationData":[OSD([sQuery(id+"F0.wireOp",EDGE,"E160.MirrorCS")])]}),"instanceName":"2"});
            var Q329;
            Q329=makeQuery(id+"F3.opPattern","COPY",FACE,{"derivedFrom":makeQuery(id+"F1.opExtrude","SWEPT_FACE",FACE,{"disambiguationData":[OSD([sQuery(id+"F0.wireOp",EDGE,"b2b48e4d-2c92-4a1f-81ad-3469f6dd68cb")])]}),"instanceName":"3"});
            var Q330;
            Q330=makeQuery(id+"F3.opPattern","COPY",EDGE,{"derivedFrom":makeQuery(id+"F1.opExtrude","CAP_EDGE",EDGE,{"disambiguationData":[OSD([sQuery(id+"F0.wireOp",EDGE,"b2b48e4d-2c92-4a1f-81ad-3469f6dd68cb")])],"isStart":false}),"instanceName":"2"});
            var Q331;
            Q331=makeQuery(id+"F3.opPattern","COPY",FACE,{"derivedFrom":makeQuery(id+"F1.opExtrude","SWEPT_FACE",FACE,{"disambiguationData":[OSD([sQuery(id+"F0.wireOp",EDGE,"b2b48e4d-2c92-4a1f-81ad-3469f6dd68cb")])]}),"instanceName":"4"});
            var Q332;
            Q332=makeQuery(id+"F3.opPattern","COPY",FACE,{"derivedFrom":makeQuery(id+"F1.opExtrude","SWEPT_FACE",FACE,{"disambiguationData":[OSD([sQuery(id+"F0.wireOp",EDGE,"E160.MirrorCS")])]}),"instanceName":"4"});
            var Q333;
            Q333=makeQuery(id+"F3.boolean.opBoolean","INTERSECT",EDGE,{"derivedFrom":[makeQuery(id+"F3.opPattern","COPY",FACE,{"derivedFrom":makeQuery(id+"F1.opExtrude","SWEPT_FACE",FACE,{"disambiguationData":[OSD([sQuery(id+"F0.wireOp",EDGE,"E160.MirrorCS")])]}),"instanceName":"3"}),makeQuery(id+"F3.opPattern","COPY",FACE,{"derivedFrom":makeQuery(id+"F1.opExtrude","SWEPT_FACE",FACE,{"disambiguationData":[OSD([sQuery(id+"F0.wireOp",EDGE,"b2b48e4d-2c92-4a1f-81ad-3469f6dd68cb")])]}),"instanceName":"4"})]});
            var Q334;
            Q334=makeQuery(id+"F1.opExtrude","CAP_EDGE",EDGE,{"disambiguationData":[OSD([sQuery(id+"F0.wireOp",EDGE,"E3")])],"isStart":true});
            var Q335;
            Q335=makeQuery(id+"F1.opExtrude","CAP_EDGE",EDGE,{"disambiguationData":[OSD([sQuery(id+"F0.wireOp",EDGE,"E11")])],"isStart":true});
            var Q336;
            Q336=makeQuery(id+"F1.opExtrude","CAP_EDGE",EDGE,{"disambiguationData":[OSD([sQuery(id+"F0.wireOp",EDGE,"E19.MirrorCS")])],"isStart":true});
            var Q337;
            Q337=makeQuery(id+"F1.opExtrude","CAP_EDGE",EDGE,{"disambiguationData":[OSD([sQuery(id+"F0.wireOp",EDGE,"E12")])],"isStart":true});
            var Q338;
            Q338=makeQuery(id+"F1.opExtrude","SWEPT_EDGE",EDGE,{"disambiguationData":[OSD([sQuery(id+"F0.wireOp",EDGE,"E15.MirrorCS"),sQuery(id+"F0.wireOp",EDGE,"E17.MirrorCS")])]});
            var Q339;
            Q339=makeQuery(id+"F1.opExtrude","SWEPT_FACE",FACE,{"disambiguationData":[OSD([sQuery(id+"F0.wireOp",EDGE,"E16.MirrorCS")])]});
            var Q340;
            Q340=makeQuery(id+"F1.opExtrude","CAP_EDGE",EDGE,{"disambiguationData":[OSD([sQuery(id+"F0.wireOp",EDGE,"E13")])],"isStart":true});
            var Q341;
            Q341=makeQuery(id+"F1.opExtrude","CAP_EDGE",EDGE,{"disambiguationData":[OSD([sQuery(id+"F0.wireOp",EDGE,"E5")])],"isStart":true});
            var Q342;
            Q342=makeQuery(id+"F1.opExtrude","CAP_EDGE",EDGE,{"disambiguationData":[OSD([sQuery(id+"F0.wireOp",EDGE,"E20.MirrorCS")])],"isStart":true});
            var Q343;
            Q343=makeQuery(id+"F1.opExtrude","SWEPT_EDGE",EDGE,{"disambiguationData":[OSD([sQuery(id+"F0.wireOp",EDGE,"E18.MirrorCS"),sQuery(id+"F0.wireOp",EDGE,"E21.MirrorCS")])]});
            var Q344;
            Q344=makeQuery(id+"F1.opExtrude","CAP_EDGE",EDGE,{"disambiguationData":[OSD([sQuery(id+"F0.wireOp",EDGE,"E14")])],"isStart":true});
            var Q345;
            Q345=makeQuery(id+"F1.opExtrude","CAP_EDGE",EDGE,{"disambiguationData":[OSD([sQuery(id+"F0.wireOp",EDGE,"E7")])],"isStart":true});
            var Q346;
            Q346=makeQuery(id+"F1.opExtrude","CAP_EDGE",EDGE,{"disambiguationData":[OSD([sQuery(id+"F0.wireOp",EDGE,"E22.MirrorCS")])],"isStart":true});
            var Q347;
            Q347=makeQuery(id+"F1.opExtrude","CAP_EDGE",EDGE,{"disambiguationData":[OSD([sQuery(id+"F0.wireOp",EDGE,"E8")])],"isStart":true});
            var Q348;
            Q348=makeQuery(id+"F3.opPattern","COPY",FACE,{"derivedFrom":makeQuery(id+"F1.opExtrude","SWEPT_FACE",FACE,{"disambiguationData":[OSD([sQuery(id+"F0.wireOp",EDGE,"E16.MirrorCS")])]}),"instanceName":"2"});
            var Q349;
            Q349=makeQuery(id+"F1.opExtrude","SWEPT_FACE",FACE,{"disambiguationData":[OSD([sQuery(id+"F0.wireOp",EDGE,"E23.MirrorCS")])]});
            var Q350;
            Q350=makeQuery(id+"F3.opPattern","COPY",FACE,{"derivedFrom":makeQuery(id+"F1.opExtrude","SWEPT_FACE",FACE,{"disambiguationData":[OSD([sQuery(id+"F0.wireOp",EDGE,"E5")])]}),"instanceName":"4"});
            var Q351;
            Q351=makeQuery(id+"F3.opPattern","COPY",FACE,{"derivedFrom":makeQuery(id+"F1.opExtrude","SWEPT_FACE",FACE,{"disambiguationData":[OSD([sQuery(id+"F0.wireOp",EDGE,"E16.MirrorCS")])]}),"instanceName":"3"});
            var Q352;
            Q352=makeQuery(id+"F1.opExtrude","CAP_EDGE",EDGE,{"disambiguationData":[OSD([sQuery(id+"F0.wireOp",EDGE,"E24.MirrorCS")])],"isStart":true});
            var Q353;
            Q353=makeQuery(id+"F1.opExtrude","CAP_EDGE",EDGE,{"disambiguationData":[OSD([sQuery(id+"F0.wireOp",EDGE,"E9")])],"isStart":true});
            var Q354;
            Q354=makeQuery(id+"F3.opPattern","COPY",FACE,{"derivedFrom":makeQuery(id+"F1.opExtrude","SWEPT_FACE",FACE,{"disambiguationData":[OSD([sQuery(id+"F0.wireOp",EDGE,"E5")])]}),"instanceName":"5"});
            var Q355;
            Q355=makeQuery(id+"F3.opPattern","COPY",EDGE,{"derivedFrom":makeQuery(id+"F1.opExtrude","SWEPT_EDGE",EDGE,{"disambiguationData":[OSD([sQuery(id+"F0.wireOp",EDGE,"E19.MirrorCS"),sQuery(id+"F0.wireOp",EDGE,"E20.MirrorCS")])]}),"instanceName":"3"});
            var Q356;
            Q356=makeQuery(id+"F3.opPattern","COPY",EDGE,{"derivedFrom":makeQuery(id+"F1.opExtrude","CAP_EDGE",EDGE,{"disambiguationData":[OSD([sQuery(id+"F0.wireOp",EDGE,"E18.MirrorCS")])],"isStart":true}),"instanceName":"5"});
            var Q357;
            Q357=makeQuery(id+"F3.opPattern","COPY",EDGE,{"derivedFrom":makeQuery(id+"F1.opExtrude","CAP_EDGE",EDGE,{"disambiguationData":[OSD([sQuery(id+"F0.wireOp",EDGE,"E25.MirrorCS")])],"isStart":true}),"instanceName":"5"});
            var Q358;
            Q358=makeQuery(id+"F3.opPattern","COPY",EDGE,{"derivedFrom":makeQuery(id+"F1.opExtrude","CAP_EDGE",EDGE,{"disambiguationData":[OSD([sQuery(id+"F0.wireOp",EDGE,"E3")])],"isStart":true}),"instanceName":"5"});
            var Q359;
            Q359=makeQuery(id+"F3.opPattern","COPY",FACE,{"derivedFrom":makeQuery(id+"F1.opExtrude","SWEPT_FACE",FACE,{"disambiguationData":[OSD([sQuery(id+"F0.wireOp",EDGE,"E6")])]}),"instanceName":"5"});
            var Q360;
            Q360=makeQuery(id+"F3.opPattern","COPY",EDGE,{"derivedFrom":makeQuery(id+"F1.opExtrude","CAP_EDGE",EDGE,{"disambiguationData":[OSD([sQuery(id+"F0.wireOp",EDGE,"E25.MirrorCS")])],"isStart":true}),"instanceName":"1"});
            var Q361;
            Q361=makeQuery(id+"F3.opPattern","COPY",EDGE,{"derivedFrom":makeQuery(id+"F1.opExtrude","CAP_EDGE",EDGE,{"disambiguationData":[OSD([sQuery(id+"F0.wireOp",EDGE,"E11")])],"isStart":true}),"instanceName":"1"});
            var Q362;
            Q362=makeQuery(id+"F3.opPattern","COPY",EDGE,{"derivedFrom":makeQuery(id+"F1.opExtrude","CAP_EDGE",EDGE,{"disambiguationData":[OSD([sQuery(id+"F0.wireOp",EDGE,"E3")])],"isStart":true}),"instanceName":"1"});
            var Q363;
            Q363=makeQuery(id+"F3.opPattern","COPY",EDGE,{"derivedFrom":makeQuery(id+"F1.opExtrude","CAP_EDGE",EDGE,{"disambiguationData":[OSD([sQuery(id+"F0.wireOp",EDGE,"E9")])],"isStart":true}),"instanceName":"2"});
            var Q364;
            Q364=makeQuery(id+"F3.opPattern","COPY",EDGE,{"derivedFrom":makeQuery(id+"F1.opExtrude","CAP_EDGE",EDGE,{"disambiguationData":[OSD([sQuery(id+"F0.wireOp",EDGE,"E7")])],"isStart":true}),"instanceName":"3"});
            var Q365;
            Q365=makeQuery(id+"F3.opPattern","COPY",EDGE,{"derivedFrom":makeQuery(id+"F1.opExtrude","CAP_EDGE",EDGE,{"disambiguationData":[OSD([sQuery(id+"F0.wireOp",EDGE,"E24.MirrorCS")])],"isStart":true}),"instanceName":"2"});
            var Q366;
            Q366=makeQuery(id+"F3.opPattern","COPY",EDGE,{"derivedFrom":makeQuery(id+"F1.opExtrude","SWEPT_EDGE",EDGE,{"disambiguationData":[OSD([sQuery(id+"F0.wireOp",EDGE,"E16.MirrorCS"),sQuery(id+"F0.wireOp",EDGE,"E23.MirrorCS")])]}),"instanceName":"4"});
            var Q367;
            Q367=makeQuery(id+"F3.opPattern","COPY",EDGE,{"derivedFrom":makeQuery(id+"F1.opExtrude","CAP_EDGE",EDGE,{"disambiguationData":[OSD([sQuery(id+"F0.wireOp",EDGE,"E22.MirrorCS")])],"isStart":true}),"instanceName":"3"});
            var Q368;
            Q368=makeQuery(id+"F3.opPattern","COPY",EDGE,{"derivedFrom":makeQuery(id+"F1.opExtrude","CAP_EDGE",EDGE,{"disambiguationData":[OSD([sQuery(id+"F0.wireOp",EDGE,"E13")])],"isStart":true}),"instanceName":"4"});
            var Q369;
            Q369=makeQuery(id+"F1.opExtrude","CAP_EDGE",EDGE,{"disambiguationData":[OSD([sQuery(id+"F0.wireOp",EDGE,"E2")])],"isStart":true});
            var Q370;
            Q370=makeQuery(id+"F1.opExtrude","CAP_EDGE",EDGE,{"disambiguationData":[OSD([sQuery(id+"F0.wireOp",EDGE,"E10")])],"isStart":true});
            var Q371;
            Q371=makeQuery(id+"F1.opExtrude","CAP_EDGE",EDGE,{"disambiguationData":[OSD([sQuery(id+"F0.wireOp",EDGE,"E17.MirrorCS")])],"isStart":true});
            var Q372;
            Q372=makeQuery(id+"F3.opPattern","COPY",EDGE,{"derivedFrom":makeQuery(id+"F1.opExtrude","SWEPT_EDGE",EDGE,{"disambiguationData":[OSD([sQuery(id+"F0.wireOp",EDGE,"E21.MirrorCS"),sQuery(id+"F0.wireOp",EDGE,"E24.MirrorCS")])]}),"instanceName":"3"});
            var Q373;
            Q373=makeQuery(id+"F3.opPattern","COPY",EDGE,{"derivedFrom":makeQuery(id+"F1.opExtrude","SWEPT_EDGE",EDGE,{"disambiguationData":[OSD([sQuery(id+"F0.wireOp",EDGE,"E15.MirrorCS"),sQuery(id+"F0.wireOp",EDGE,"E22.MirrorCS")])]}),"instanceName":"5"});
            var Q374;
            Q374=makeQuery(id+"F3.opPattern","COPY",EDGE,{"derivedFrom":makeQuery(id+"F1.opExtrude","CAP_EDGE",EDGE,{"disambiguationData":[OSD([sQuery(id+"F0.wireOp",EDGE,"E19.MirrorCS")])],"isStart":true}),"instanceName":"1"});
            var Q375;
            Q375=makeQuery(id+"F3.opPattern","COPY",EDGE,{"derivedFrom":makeQuery(id+"F1.opExtrude","CAP_EDGE",EDGE,{"disambiguationData":[OSD([sQuery(id+"F0.wireOp",EDGE,"E12")])],"isStart":true}),"instanceName":"1"});
            var Q376;
            Q376=makeQuery(id+"F3.opPattern","COPY",EDGE,{"derivedFrom":makeQuery(id+"F1.opExtrude","CAP_EDGE",EDGE,{"disambiguationData":[OSD([sQuery(id+"F0.wireOp",EDGE,"E17.MirrorCS")])],"isStart":true}),"instanceName":"2"});
            var Q377;
            Q377=makeQuery(id+"F3.opPattern","COPY",EDGE,{"derivedFrom":makeQuery(id+"F1.opExtrude","CAP_EDGE",EDGE,{"disambiguationData":[OSD([sQuery(id+"F0.wireOp",EDGE,"E10")])],"isStart":true}),"instanceName":"2"});
            var Q378;
            Q378=makeQuery(id+"F3.opPattern","COPY",EDGE,{"derivedFrom":makeQuery(id+"F1.opExtrude","CAP_EDGE",EDGE,{"disambiguationData":[OSD([sQuery(id+"F0.wireOp",EDGE,"E2")])],"isStart":true}),"instanceName":"2"});
            var Q379;
            Q379=makeQuery(id+"F3.opPattern","COPY",EDGE,{"derivedFrom":makeQuery(id+"F1.opExtrude","SWEPT_EDGE",EDGE,{"disambiguationData":[OSD([sQuery(id+"F0.wireOp",EDGE,"E5"),sQuery(id+"F0.wireOp",EDGE,"E6")])]}),"instanceName":"4"});
            var Q380;
            Q380=makeQuery(id+"F3.opPattern","COPY",EDGE,{"derivedFrom":makeQuery(id+"F1.opExtrude","CAP_EDGE",EDGE,{"disambiguationData":[OSD([sQuery(id+"F0.wireOp",EDGE,"E15.MirrorCS")])],"isStart":true}),"instanceName":"3"});
            var Q381;
            Q381=makeQuery(id+"F3.opPattern","COPY",EDGE,{"derivedFrom":makeQuery(id+"F1.opExtrude","CAP_EDGE",EDGE,{"disambiguationData":[OSD([sQuery(id+"F0.wireOp",EDGE,"E14")])],"isStart":true}),"instanceName":"4"});
            var Q382;
            Q382=makeQuery(id+"F3.opPattern","COPY",EDGE,{"derivedFrom":makeQuery(id+"F1.opExtrude","CAP_EDGE",EDGE,{"disambiguationData":[OSD([sQuery(id+"F0.wireOp",EDGE,"E19.MirrorCS")])],"isStart":true}),"instanceName":"5"});
            var Q383;
            Q383=makeQuery(id+"F3.opPattern","COPY",EDGE,{"derivedFrom":makeQuery(id+"F1.opExtrude","CAP_EDGE",EDGE,{"disambiguationData":[OSD([sQuery(id+"F0.wireOp",EDGE,"E6")])],"isStart":true}),"instanceName":"4"});
            var Q384;
            Q384=makeQuery(id+"F3.opPattern","COPY",EDGE,{"derivedFrom":makeQuery(id+"F1.opExtrude","CAP_EDGE",EDGE,{"disambiguationData":[OSD([sQuery(id+"F0.wireOp",EDGE,"E12")])],"isStart":true}),"instanceName":"5"});
            var Q385;
            Q385=makeQuery(id+"F3.opPattern","COPY",FACE,{"derivedFrom":makeQuery(id+"F1.opExtrude","SWEPT_FACE",FACE,{"disambiguationData":[OSD([sQuery(id+"F0.wireOp",EDGE,"E19.MirrorCS")])]}),"instanceName":"3"});
            var Q386;
            Q386=makeQuery(id+"F3.opPattern","COPY",EDGE,{"derivedFrom":makeQuery(id+"F1.opExtrude","SWEPT_EDGE",EDGE,{"disambiguationData":[OSD([sQuery(id+"F0.wireOp",EDGE,"E160.MirrorCS"),sQuery(id+"F0.wireOp",EDGE,"E25.MirrorCS")])]}),"instanceName":"3"});
            var Q387;
            Q387=makeQuery(id+"F3.opPattern","COPY",FACE,{"derivedFrom":makeQuery(id+"F1.opExtrude","SWEPT_FACE",FACE,{"disambiguationData":[OSD([sQuery(id+"F0.wireOp",EDGE,"E20.MirrorCS")])]}),"instanceName":"3"});
            var Q388;
            Q388=makeQuery(id+"F3.opPattern","COPY",FACE,{"derivedFrom":makeQuery(id+"F1.opExtrude","SWEPT_FACE",FACE,{"disambiguationData":[OSD([sQuery(id+"F0.wireOp",EDGE,"E22.MirrorCS")])]}),"instanceName":"4"});
            var Q389;
            Q389=makeQuery(id+"F3.opPattern","COPY",EDGE,{"derivedFrom":makeQuery(id+"F1.opExtrude","SWEPT_EDGE",EDGE,{"disambiguationData":[OSD([sQuery(id+"F0.wireOp",EDGE,"E11"),sQuery(id+"F0.wireOp",EDGE,"E12")])]}),"instanceName":"3"});
            var Q390;
            Q390=makeQuery(id+"F3.opPattern","COPY",EDGE,{"derivedFrom":makeQuery(id+"F1.opExtrude","CAP_EDGE",EDGE,{"disambiguationData":[OSD([sQuery(id+"F0.wireOp",EDGE,"E9")])],"isStart":true}),"instanceName":"3"});
            var Q391;
            Q391=makeQuery(id+"F3.opPattern","COPY",EDGE,{"derivedFrom":makeQuery(id+"F1.opExtrude","CAP_EDGE",EDGE,{"disambiguationData":[OSD([sQuery(id+"F0.wireOp",EDGE,"E25.MirrorCS")])],"isStart":true}),"instanceName":"2"});
            var Q392;
            Q392=makeQuery(id+"F3.opPattern","COPY",EDGE,{"derivedFrom":makeQuery(id+"F1.opExtrude","CAP_EDGE",EDGE,{"disambiguationData":[OSD([sQuery(id+"F0.wireOp",EDGE,"E16.MirrorCS")])],"isStart":true}),"instanceName":"3"});
            var Q393;
            Q393=makeQuery(id+"F3.opPattern","COPY",EDGE,{"derivedFrom":makeQuery(id+"F1.opExtrude","CAP_EDGE",EDGE,{"disambiguationData":[OSD([sQuery(id+"F0.wireOp",EDGE,"E20.MirrorCS")])],"isStart":true}),"instanceName":"5"});
            var Q394;
            Q394=makeQuery(id+"F3.opPattern","COPY",EDGE,{"derivedFrom":makeQuery(id+"F1.opExtrude","CAP_EDGE",EDGE,{"disambiguationData":[OSD([sQuery(id+"F0.wireOp",EDGE,"E7")])],"isStart":true}),"instanceName":"4"});
            var Q395;
            Q395=makeQuery(id+"F3.opPattern","COPY",EDGE,{"derivedFrom":makeQuery(id+"F1.opExtrude","CAP_EDGE",EDGE,{"disambiguationData":[OSD([sQuery(id+"F0.wireOp",EDGE,"E13")])],"isStart":true}),"instanceName":"5"});
            var Q396;
            Q396=makeQuery(id+"F3.opPattern","COPY",FACE,{"derivedFrom":makeQuery(id+"F1.opExtrude","SWEPT_FACE",FACE,{"disambiguationData":[OSD([sQuery(id+"F0.wireOp",EDGE,"E6")])]}),"instanceName":"3"});
            var Q397;
            Q397=makeQuery(id+"F3.opPattern","COPY",EDGE,{"derivedFrom":makeQuery(id+"F1.opExtrude","CAP_EDGE",EDGE,{"disambiguationData":[OSD([sQuery(id+"F0.wireOp",EDGE,"E13")])],"isStart":true}),"instanceName":"1"});
            var Q398;
            Q398=makeQuery(id+"F3.opPattern","COPY",EDGE,{"derivedFrom":makeQuery(id+"F1.opExtrude","CAP_EDGE",EDGE,{"disambiguationData":[OSD([sQuery(id+"F0.wireOp",EDGE,"E20.MirrorCS")])],"isStart":true}),"instanceName":"1"});
            var Q399;
            Q399=makeQuery(id+"F3.opPattern","COPY",EDGE,{"derivedFrom":makeQuery(id+"F1.opExtrude","CAP_EDGE",EDGE,{"disambiguationData":[OSD([sQuery(id+"F0.wireOp",EDGE,"E18.MirrorCS")])],"isStart":true}),"instanceName":"2"});
            var Q400;
            Q400=makeQuery(id+"F3.opPattern","COPY",EDGE,{"derivedFrom":makeQuery(id+"F1.opExtrude","CAP_EDGE",EDGE,{"disambiguationData":[OSD([sQuery(id+"F0.wireOp",EDGE,"E11")])],"isStart":true}),"instanceName":"2"});
            var Q401;
            Q401=makeQuery(id+"F3.opPattern","COPY",EDGE,{"derivedFrom":makeQuery(id+"F1.opExtrude","CAP_EDGE",EDGE,{"disambiguationData":[OSD([sQuery(id+"F0.wireOp",EDGE,"E3")])],"isStart":true}),"instanceName":"2"});
            var Q402;
            Q402=makeQuery(id+"F3.opPattern","COPY",EDGE,{"derivedFrom":makeQuery(id+"F1.opExtrude","SWEPT_EDGE",EDGE,{"disambiguationData":[OSD([sQuery(id+"F0.wireOp",EDGE,"E8"),sQuery(id+"F0.wireOp",EDGE,"E9")])]}),"instanceName":"4"});
            var Q403;
            Q403=makeQuery(id+"F3.opPattern","COPY",FACE,{"derivedFrom":makeQuery(id+"F1.opExtrude","SWEPT_FACE",FACE,{"disambiguationData":[OSD([sQuery(id+"F0.wireOp",EDGE,"E22.MirrorCS")])]}),"instanceName":"3"});
            var Q404;
            Q404=makeQuery(id+"F3.opPattern","COPY",FACE,{"derivedFrom":makeQuery(id+"F1.opExtrude","SWEPT_FACE",FACE,{"disambiguationData":[OSD([sQuery(id+"F0.wireOp",EDGE,"E11")])]}),"instanceName":"5"});
            var Q405;
            Q405=makeQuery(id+"F3.opPattern","COPY",EDGE,{"derivedFrom":makeQuery(id+"F1.opExtrude","SWEPT_EDGE",EDGE,{"disambiguationData":[OSD([sQuery(id+"F0.wireOp",EDGE,"E15.MirrorCS"),sQuery(id+"F0.wireOp",EDGE,"E22.MirrorCS")])]}),"instanceName":"2"});
            var Q406;
            Q406=makeQuery(id+"F3.opPattern","COPY",EDGE,{"derivedFrom":makeQuery(id+"F1.opExtrude","CAP_EDGE",EDGE,{"disambiguationData":[OSD([sQuery(id+"F0.wireOp",EDGE,"E23.MirrorCS")])],"isStart":true}),"instanceName":"4"});
            var Q407;
            Q407=makeQuery(id+"F3.opPattern","COPY",FACE,{"derivedFrom":makeQuery(id+"F1.opExtrude","SWEPT_FACE",FACE,{"disambiguationData":[OSD([sQuery(id+"F0.wireOp",EDGE,"E23.MirrorCS")])]}),"instanceName":"3"});
            var Q408;
            Q408=makeQuery(id+"F3.opPattern","COPY",EDGE,{"derivedFrom":makeQuery(id+"F1.opExtrude","CAP_EDGE",EDGE,{"disambiguationData":[OSD([sQuery(id+"F0.wireOp",EDGE,"E21.MirrorCS")])],"isStart":true}),"instanceName":"1"});
            var Q409;
            Q409=makeQuery(id+"F3.opPattern","COPY",EDGE,{"derivedFrom":makeQuery(id+"F1.opExtrude","CAP_EDGE",EDGE,{"disambiguationData":[OSD([sQuery(id+"F0.wireOp",EDGE,"E14")])],"isStart":true}),"instanceName":"1"});
            var Q410;
            Q410=makeQuery(id+"F3.opPattern","COPY",EDGE,{"derivedFrom":makeQuery(id+"F1.opExtrude","CAP_EDGE",EDGE,{"disambiguationData":[OSD([sQuery(id+"F0.wireOp",EDGE,"E6")])],"isStart":true}),"instanceName":"1"});
            var Q411;
            Q411=makeQuery(id+"F3.opPattern","COPY",EDGE,{"derivedFrom":makeQuery(id+"F1.opExtrude","CAP_EDGE",EDGE,{"disambiguationData":[OSD([sQuery(id+"F0.wireOp",EDGE,"E19.MirrorCS")])],"isStart":true}),"instanceName":"2"});
            var Q412;
            Q412=makeQuery(id+"F3.opPattern","COPY",EDGE,{"derivedFrom":makeQuery(id+"F1.opExtrude","CAP_EDGE",EDGE,{"disambiguationData":[OSD([sQuery(id+"F0.wireOp",EDGE,"E4")])],"isStart":true}),"instanceName":"2"});
            var Q413;
            Q413=makeQuery(id+"F3.opPattern","COPY",EDGE,{"derivedFrom":makeQuery(id+"F1.opExtrude","CAP_EDGE",EDGE,{"disambiguationData":[OSD([sQuery(id+"F0.wireOp",EDGE,"E2")])],"isStart":true}),"instanceName":"3"});
            var Q414;
            Q414=makeQuery(id+"F3.opPattern","COPY",FACE,{"derivedFrom":makeQuery(id+"F1.opExtrude","SWEPT_FACE",FACE,{"disambiguationData":[OSD([sQuery(id+"F0.wireOp",EDGE,"E11")])]}),"instanceName":"4"});
            var Q415;
            Q415=makeQuery(id+"F3.opPattern","COPY",EDGE,{"derivedFrom":makeQuery(id+"F1.opExtrude","CAP_EDGE",EDGE,{"disambiguationData":[OSD([sQuery(id+"F0.wireOp",EDGE,"E7")])],"isStart":true}),"instanceName":"1"});
            var Q416;
            Q416=makeQuery(id+"F3.opPattern","COPY",EDGE,{"derivedFrom":makeQuery(id+"F1.opExtrude","CAP_EDGE",EDGE,{"disambiguationData":[OSD([sQuery(id+"F0.wireOp",EDGE,"E20.MirrorCS")])],"isStart":true}),"instanceName":"2"});
            var Q417;
            Q417=makeQuery(id+"F3.opPattern","COPY",EDGE,{"derivedFrom":makeQuery(id+"F1.opExtrude","CAP_EDGE",EDGE,{"disambiguationData":[OSD([sQuery(id+"F0.wireOp",EDGE,"E5")])],"isStart":true}),"instanceName":"2"});
            var Q418;
            Q418=makeQuery(id+"F3.opPattern","COPY",EDGE,{"derivedFrom":makeQuery(id+"F1.opExtrude","SWEPT_EDGE",EDGE,{"disambiguationData":[OSD([sQuery(id+"F0.wireOp",EDGE,"E16.MirrorCS"),sQuery(id+"F0.wireOp",EDGE,"E23.MirrorCS")])]}),"instanceName":"2"});
            var Q419;
            Q419=makeQuery(id+"F3.opPattern","COPY",EDGE,{"derivedFrom":makeQuery(id+"F1.opExtrude","CAP_EDGE",EDGE,{"disambiguationData":[OSD([sQuery(id+"F0.wireOp",EDGE,"E11")])],"isStart":true}),"instanceName":"3"});
            var Q420;
            Q420=makeQuery(id+"F3.opPattern","COPY",EDGE,{"derivedFrom":makeQuery(id+"F1.opExtrude","CAP_EDGE",EDGE,{"disambiguationData":[OSD([sQuery(id+"F0.wireOp",EDGE,"E3")])],"isStart":true}),"instanceName":"3"});
            var Q421;
            Q421=makeQuery(id+"F3.opPattern","COPY",EDGE,{"derivedFrom":makeQuery(id+"F1.opExtrude","CAP_EDGE",EDGE,{"disambiguationData":[OSD([sQuery(id+"F0.wireOp",EDGE,"E16.MirrorCS")])],"isStart":true}),"instanceName":"4"});
            var Q422;
            Q422=makeQuery(id+"F3.opPattern","COPY",EDGE,{"derivedFrom":makeQuery(id+"F1.opExtrude","CAP_EDGE",EDGE,{"disambiguationData":[OSD([sQuery(id+"F0.wireOp",EDGE,"E7")])],"isStart":true}),"instanceName":"5"});
            var Q423;
            Q423=makeQuery(id+"F3.opPattern","COPY",FACE,{"derivedFrom":makeQuery(id+"F1.opExtrude","SWEPT_FACE",FACE,{"disambiguationData":[OSD([sQuery(id+"F0.wireOp",EDGE,"E8")])]}),"instanceName":"2"});
            var Q424;
            Q424=makeQuery(id+"F3.opPattern","COPY",EDGE,{"derivedFrom":makeQuery(id+"F1.opExtrude","CAP_EDGE",EDGE,{"disambiguationData":[OSD([sQuery(id+"F0.wireOp",EDGE,"b2b48e4d-2c92-4a1f-81ad-3469f6dd68cb")])],"isStart":true}),"instanceName":"4"});
            var Q425;
            Q425=makeQuery(id+"F3.opPattern","COPY",FACE,{"derivedFrom":makeQuery(id+"F1.opExtrude","SWEPT_FACE",FACE,{"disambiguationData":[OSD([sQuery(id+"F0.wireOp",EDGE,"E14")])]}),"instanceName":"5"});
            var Q426;
            Q426=makeQuery(id+"F3.opPattern","COPY",EDGE,{"derivedFrom":makeQuery(id+"F1.opExtrude","SWEPT_EDGE",EDGE,{"disambiguationData":[OSD([sQuery(id+"F0.wireOp",EDGE,"E15.MirrorCS"),sQuery(id+"F0.wireOp",EDGE,"E22.MirrorCS")])]}),"instanceName":"3"});
            var Q427;
            Q427=makeQuery(id+"F3.opPattern","COPY",EDGE,{"derivedFrom":makeQuery(id+"F1.opExtrude","SWEPT_EDGE",EDGE,{"disambiguationData":[OSD([sQuery(id+"F0.wireOp",EDGE,"E12"),sQuery(id+"F0.wireOp",EDGE,"E13")])]}),"instanceName":"4"});
            var Q428;
            Q428=makeQuery(id+"F3.opPattern","COPY",FACE,{"derivedFrom":makeQuery(id+"F1.opExtrude","SWEPT_FACE",FACE,{"disambiguationData":[OSD([sQuery(id+"F0.wireOp",EDGE,"E22.MirrorCS")])]}),"instanceName":"1"});
            var Q429;
            Q429=makeQuery(id+"F3.opPattern","COPY",EDGE,{"derivedFrom":makeQuery(id+"F1.opExtrude","CAP_EDGE",EDGE,{"disambiguationData":[OSD([sQuery(id+"F0.wireOp",EDGE,"E6")])],"isStart":true}),"instanceName":"2"});
            var Q430;
            Q430=makeQuery(id+"F3.opPattern","COPY",EDGE,{"derivedFrom":makeQuery(id+"F1.opExtrude","CAP_EDGE",EDGE,{"disambiguationData":[OSD([sQuery(id+"F0.wireOp",EDGE,"E23.MirrorCS")])],"isStart":true}),"instanceName":"1"});
            var Q431;
            Q431=makeQuery(id+"F3.opPattern","COPY",EDGE,{"derivedFrom":makeQuery(id+"F1.opExtrude","SWEPT_EDGE",EDGE,{"disambiguationData":[OSD([sQuery(id+"F0.wireOp",EDGE,"E15.MirrorCS"),sQuery(id+"F0.wireOp",EDGE,"E17.MirrorCS")])]}),"instanceName":"3"});
            var Q432;
            Q432=makeQuery(id+"F3.opPattern","COPY",EDGE,{"derivedFrom":makeQuery(id+"F1.opExtrude","CAP_EDGE",EDGE,{"disambiguationData":[OSD([sQuery(id+"F0.wireOp",EDGE,"E21.MirrorCS")])],"isStart":true}),"instanceName":"2"});
            var Q433;
            Q433=makeQuery(id+"F3.opPattern","COPY",EDGE,{"derivedFrom":makeQuery(id+"F1.opExtrude","CAP_EDGE",EDGE,{"disambiguationData":[OSD([sQuery(id+"F0.wireOp",EDGE,"E19.MirrorCS")])],"isStart":true}),"instanceName":"3"});
            var Q434;
            Q434=makeQuery(id+"F3.opPattern","COPY",EDGE,{"derivedFrom":makeQuery(id+"F1.opExtrude","CAP_EDGE",EDGE,{"disambiguationData":[OSD([sQuery(id+"F0.wireOp",EDGE,"E4")])],"isStart":true}),"instanceName":"3"});
            var Q435;
            Q435=makeQuery(id+"F3.opPattern","COPY",EDGE,{"derivedFrom":makeQuery(id+"F1.opExtrude","CAP_EDGE",EDGE,{"disambiguationData":[OSD([sQuery(id+"F0.wireOp",EDGE,"E2")])],"isStart":true}),"instanceName":"4"});
            var Q436;
            Q436=makeQuery(id+"F3.opPattern","COPY",EDGE,{"derivedFrom":makeQuery(id+"F1.opExtrude","CAP_EDGE",EDGE,{"disambiguationData":[OSD([sQuery(id+"F0.wireOp",EDGE,"E10")])],"isStart":true}),"instanceName":"4"});
            var Q437;
            Q437=makeQuery(id+"F3.opPattern","COPY",EDGE,{"derivedFrom":makeQuery(id+"F1.opExtrude","CAP_EDGE",EDGE,{"disambiguationData":[OSD([sQuery(id+"F0.wireOp",EDGE,"E17.MirrorCS")])],"isStart":true}),"instanceName":"4"});
            var Q438;
            Q438=makeQuery(id+"F3.opPattern","COPY",EDGE,{"derivedFrom":makeQuery(id+"F1.opExtrude","SWEPT_EDGE",EDGE,{"disambiguationData":[OSD([sQuery(id+"F0.wireOp",EDGE,"E23.MirrorCS"),sQuery(id+"F0.wireOp",EDGE,"E24.MirrorCS")])]}),"instanceName":"5"});
            var Q439;
            Q439=makeQuery(id+"F3.opPattern","COPY",EDGE,{"derivedFrom":makeQuery(id+"F1.opExtrude","CAP_EDGE",EDGE,{"disambiguationData":[OSD([sQuery(id+"F0.wireOp",EDGE,"E8")])],"isStart":true}),"instanceName":"5"});
            var Q440;
            Q440=makeQuery(id+"F3.opPattern","COPY",EDGE,{"derivedFrom":makeQuery(id+"F1.opExtrude","CAP_EDGE",EDGE,{"disambiguationData":[OSD([sQuery(id+"F0.wireOp",EDGE,"E23.MirrorCS")])],"isStart":true}),"instanceName":"5"});
            var Q441;
            Q441=makeQuery(id+"F3.opPattern","COPY",EDGE,{"derivedFrom":makeQuery(id+"F1.opExtrude","CAP_EDGE",EDGE,{"disambiguationData":[OSD([sQuery(id+"F0.wireOp",EDGE,"E160.MirrorCS")])],"isStart":true}),"instanceName":"4"});
            var Q442;
            Q442=makeQuery(id+"F3.opPattern","COPY",FACE,{"derivedFrom":makeQuery(id+"F1.opExtrude","SWEPT_FACE",FACE,{"disambiguationData":[OSD([sQuery(id+"F0.wireOp",EDGE,"E15.MirrorCS")])]}),"instanceName":"5"});
            var Q443;
            Q443=makeQuery(id+"F3.opPattern","COPY",EDGE,{"derivedFrom":makeQuery(id+"F1.opExtrude","SWEPT_EDGE",EDGE,{"disambiguationData":[OSD([sQuery(id+"F0.wireOp",EDGE,"E19.MirrorCS"),sQuery(id+"F0.wireOp",EDGE,"E20.MirrorCS")])]}),"instanceName":"2"});
            var Q444;
            Q444=makeQuery(id+"F3.opPattern","COPY",FACE,{"derivedFrom":makeQuery(id+"F1.opExtrude","SWEPT_FACE",FACE,{"disambiguationData":[OSD([sQuery(id+"F0.wireOp",EDGE,"E16.MirrorCS")])]}),"instanceName":"5"});
            var Q445;
            Q445=makeQuery(id+"F3.opPattern","COPY",EDGE,{"derivedFrom":makeQuery(id+"F1.opExtrude","CAP_EDGE",EDGE,{"disambiguationData":[OSD([sQuery(id+"F0.wireOp",EDGE,"E16.MirrorCS")])],"isStart":true}),"instanceName":"1"});
            var Q446;
            Q446=makeQuery(id+"F3.opPattern","COPY",EDGE,{"derivedFrom":makeQuery(id+"F1.opExtrude","CAP_EDGE",EDGE,{"disambiguationData":[OSD([sQuery(id+"F0.wireOp",EDGE,"E7")])],"isStart":true}),"instanceName":"2"});
            var Q447;
            Q447=makeQuery(id+"F3.opPattern","COPY",EDGE,{"derivedFrom":makeQuery(id+"F1.opExtrude","SWEPT_EDGE",EDGE,{"disambiguationData":[OSD([sQuery(id+"F0.wireOp",EDGE,"E20.MirrorCS"),sQuery(id+"F0.wireOp",EDGE,"E25.MirrorCS")])]}),"instanceName":"2"});
            var Q448;
            Q448=makeQuery(id+"F3.opPattern","COPY",EDGE,{"derivedFrom":makeQuery(id+"F1.opExtrude","CAP_EDGE",EDGE,{"disambiguationData":[OSD([sQuery(id+"F0.wireOp",EDGE,"E24.MirrorCS")])],"isStart":true}),"instanceName":"1"});
            var Q449;
            Q449=makeQuery(id+"F3.opPattern","COPY",EDGE,{"derivedFrom":makeQuery(id+"F1.opExtrude","CAP_EDGE",EDGE,{"disambiguationData":[OSD([sQuery(id+"F0.wireOp",EDGE,"E22.MirrorCS")])],"isStart":true}),"instanceName":"2"});
            var Q450;
            Q450=makeQuery(id+"F3.opPattern","COPY",EDGE,{"derivedFrom":makeQuery(id+"F1.opExtrude","CAP_EDGE",EDGE,{"disambiguationData":[OSD([sQuery(id+"F0.wireOp",EDGE,"E13")])],"isStart":true}),"instanceName":"3"});
            var Q451;
            Q451=makeQuery(id+"F3.opPattern","COPY",EDGE,{"derivedFrom":makeQuery(id+"F1.opExtrude","CAP_EDGE",EDGE,{"disambiguationData":[OSD([sQuery(id+"F0.wireOp",EDGE,"E5")])],"isStart":true}),"instanceName":"3"});
            var Q452;
            Q452=makeQuery(id+"F3.opPattern","COPY",EDGE,{"derivedFrom":makeQuery(id+"F1.opExtrude","CAP_EDGE",EDGE,{"disambiguationData":[OSD([sQuery(id+"F0.wireOp",EDGE,"E18.MirrorCS")])],"isStart":true}),"instanceName":"4"});
            var Q453;
            Q453=makeQuery(id+"F3.opPattern","COPY",EDGE,{"derivedFrom":makeQuery(id+"F1.opExtrude","CAP_EDGE",EDGE,{"disambiguationData":[OSD([sQuery(id+"F0.wireOp",EDGE,"E24.MirrorCS")])],"isStart":true}),"instanceName":"5"});
            var Q454;
            Q454=makeQuery(id+"F3.opPattern","COPY",EDGE,{"derivedFrom":makeQuery(id+"F1.opExtrude","CAP_EDGE",EDGE,{"disambiguationData":[OSD([sQuery(id+"F0.wireOp",EDGE,"E9")])],"isStart":true}),"instanceName":"5"});
            var Q455;
            Q455=makeQuery(id+"F3.opPattern","COPY",EDGE,{"derivedFrom":makeQuery(id+"F1.opExtrude","CAP_EDGE",EDGE,{"disambiguationData":[OSD([sQuery(id+"F0.wireOp",EDGE,"E25.MirrorCS")])],"isStart":true}),"instanceName":"4"});
            var Q456;
            Q456=makeQuery(id+"F3.opPattern","COPY",EDGE,{"derivedFrom":makeQuery(id+"F1.opExtrude","SWEPT_EDGE",EDGE,{"disambiguationData":[OSD([sQuery(id+"F0.wireOp",EDGE,"E18.MirrorCS"),sQuery(id+"F0.wireOp",EDGE,"E21.MirrorCS")])]}),"instanceName":"3"});
            var Q457;
            Q457=makeQuery(id+"F3.opPattern","COPY",EDGE,{"derivedFrom":makeQuery(id+"F1.opExtrude","CAP_EDGE",EDGE,{"disambiguationData":[OSD([sQuery(id+"F0.wireOp",EDGE,"E17.MirrorCS")])],"isStart":true}),"instanceName":"1"});
            var Q458;
            Q458=makeQuery(id+"F3.opPattern","COPY",EDGE,{"derivedFrom":makeQuery(id+"F1.opExtrude","CAP_EDGE",EDGE,{"disambiguationData":[OSD([sQuery(id+"F0.wireOp",EDGE,"E10")])],"isStart":true}),"instanceName":"1"});
            var Q459;
            Q459=makeQuery(id+"F3.opPattern","COPY",EDGE,{"derivedFrom":makeQuery(id+"F1.opExtrude","CAP_EDGE",EDGE,{"disambiguationData":[OSD([sQuery(id+"F0.wireOp",EDGE,"E23.MirrorCS")])],"isStart":true}),"instanceName":"2"});
            var Q460;
            Q460=makeQuery(id+"F3.opPattern","COPY",EDGE,{"derivedFrom":makeQuery(id+"F1.opExtrude","CAP_EDGE",EDGE,{"disambiguationData":[OSD([sQuery(id+"F0.wireOp",EDGE,"E15.MirrorCS")])],"isStart":true}),"instanceName":"2"});
            var Q461;
            Q461=makeQuery(id+"F3.opPattern","COPY",EDGE,{"derivedFrom":makeQuery(id+"F1.opExtrude","CAP_EDGE",EDGE,{"disambiguationData":[OSD([sQuery(id+"F0.wireOp",EDGE,"E14")])],"isStart":true}),"instanceName":"3"});
            var Q462;
            Q462=makeQuery(id+"F3.opPattern","COPY",EDGE,{"derivedFrom":makeQuery(id+"F1.opExtrude","CAP_EDGE",EDGE,{"disambiguationData":[OSD([sQuery(id+"F0.wireOp",EDGE,"E19.MirrorCS")])],"isStart":true}),"instanceName":"4"});
            var Q463;
            Q463=makeQuery(id+"F3.opPattern","COPY",EDGE,{"derivedFrom":makeQuery(id+"F1.opExtrude","CAP_EDGE",EDGE,{"disambiguationData":[OSD([sQuery(id+"F0.wireOp",EDGE,"E2")])],"isStart":true}),"instanceName":"5"});
            var Q464;
            Q464=makeQuery(id+"F3.opPattern","COPY",EDGE,{"derivedFrom":makeQuery(id+"F1.opExtrude","CAP_EDGE",EDGE,{"disambiguationData":[OSD([sQuery(id+"F0.wireOp",EDGE,"E10")])],"isStart":true}),"instanceName":"5"});
            var Q465;
            Q465=makeQuery(id+"F3.opPattern","COPY",EDGE,{"derivedFrom":makeQuery(id+"F1.opExtrude","CAP_EDGE",EDGE,{"disambiguationData":[OSD([sQuery(id+"F0.wireOp",EDGE,"E17.MirrorCS")])],"isStart":true}),"instanceName":"5"});
            var Q466;
            Q466=makeQuery(id+"F3.opPattern","COPY",FACE,{"derivedFrom":makeQuery(id+"F1.opExtrude","SWEPT_FACE",FACE,{"disambiguationData":[OSD([sQuery(id+"F0.wireOp",EDGE,"E14")])]}),"instanceName":"2"});
            var Q467;
            Q467=makeQuery(id+"F3.opPattern","COPY",EDGE,{"derivedFrom":makeQuery(id+"F1.opExtrude","CAP_EDGE",EDGE,{"disambiguationData":[OSD([sQuery(id+"F0.wireOp",EDGE,"E160.MirrorCS")])],"isStart":true}),"instanceName":"5"});
            var Q468;
            Q468=makeQuery(id+"F1.opExtrude","SWEPT_EDGE",EDGE,{"disambiguationData":[OSD([sQuery(id+"F0.wireOp",EDGE,"E15.MirrorCS"),sQuery(id+"F0.wireOp",EDGE,"E22.MirrorCS")])]});
            var Q469;
            Q469=makeQuery(id+"F1.opExtrude","SWEPT_FACE",FACE,{"disambiguationData":[OSD([sQuery(id+"F0.wireOp",EDGE,"E6")])]});
            var Q470;
            Q470=makeQuery(id+"F3.opPattern","COPY",EDGE,{"derivedFrom":makeQuery(id+"F1.opExtrude","SWEPT_EDGE",EDGE,{"disambiguationData":[OSD([sQuery(id+"F0.wireOp",EDGE,"E15.MirrorCS"),sQuery(id+"F0.wireOp",EDGE,"E22.MirrorCS")])]}),"instanceName":"1"});
            var Q471;
            Q471=makeQuery(id+"F1.opExtrude","SWEPT_EDGE",EDGE,{"disambiguationData":[OSD([sQuery(id+"F0.wireOp",EDGE,"E13"),sQuery(id+"F0.wireOp",EDGE,"E14")])]});
            var Q472;
            Q472=makeQuery(id+"F3.opPattern","COPY",EDGE,{"derivedFrom":makeQuery(id+"F1.opExtrude","SWEPT_EDGE",EDGE,{"disambiguationData":[OSD([sQuery(id+"F0.wireOp",EDGE,"E3"),sQuery(id+"F0.wireOp",EDGE,"E4")])]}),"instanceName":"1"});
            var Q473;
            Q473=makeQuery(id+"F3.opPattern","COPY",FACE,{"derivedFrom":makeQuery(id+"F1.opExtrude","SWEPT_FACE",FACE,{"disambiguationData":[OSD([sQuery(id+"F0.wireOp",EDGE,"E5")])]}),"instanceName":"1"});
            var Q474;
            Q474=makeQuery(id+"F1.opExtrude","CAP_EDGE",EDGE,{"disambiguationData":[OSD([sQuery(id+"F0.wireOp",EDGE,"b2b48e4d-2c92-4a1f-81ad-3469f6dd68cb")])],"isStart":false});
            var Q475;
            Q475=makeQuery(id+"F1.opExtrude","CAP_EDGE",EDGE,{"disambiguationData":[OSD([sQuery(id+"F0.wireOp",EDGE,"E160.MirrorCS")])],"isStart":true});
            var Q476;
            Q476=makeQuery(id+"F3.opPattern","COPY",EDGE,{"derivedFrom":makeQuery(id+"F1.opExtrude","CAP_EDGE",EDGE,{"disambiguationData":[OSD([sQuery(id+"F0.wireOp",EDGE,"b2b48e4d-2c92-4a1f-81ad-3469f6dd68cb")])],"isStart":true}),"instanceName":"1"});
            var Q477;
            Q477=makeQuery(id+"F3.opPattern","COPY",EDGE,{"derivedFrom":makeQuery(id+"F1.opExtrude","SWEPT_EDGE",EDGE,{"disambiguationData":[OSD([sQuery(id+"F0.wireOp",EDGE,"E13"),sQuery(id+"F0.wireOp",EDGE,"E14")])]}),"instanceName":"1"});
            var Q478;
            Q478=makeQuery(id+"F3.opPattern","COPY",EDGE,{"derivedFrom":makeQuery(id+"F1.opExtrude","CAP_EDGE",EDGE,{"disambiguationData":[OSD([sQuery(id+"F0.wireOp",EDGE,"b2b48e4d-2c92-4a1f-81ad-3469f6dd68cb")])],"isStart":true}),"instanceName":"2"});
            var Q479;
            Q479=makeQuery(id+"F3.opPattern","COPY",EDGE,{"derivedFrom":makeQuery(id+"F1.opExtrude","CAP_EDGE",EDGE,{"disambiguationData":[OSD([sQuery(id+"F0.wireOp",EDGE,"E160.MirrorCS")])],"isStart":true}),"instanceName":"2"});
            var Q480;
            Q480=makeQuery(id+"F3.opPattern","COPY",EDGE,{"derivedFrom":makeQuery(id+"F1.opExtrude","CAP_EDGE",EDGE,{"disambiguationData":[OSD([sQuery(id+"F0.wireOp",EDGE,"b2b48e4d-2c92-4a1f-81ad-3469f6dd68cb")])],"isStart":true}),"instanceName":"3"});
            var Q481;
            Q481=makeQuery(id+"F3.opPattern","COPY",FACE,{"derivedFrom":makeQuery(id+"F1.opExtrude","SWEPT_FACE",FACE,{"disambiguationData":[OSD([sQuery(id+"F0.wireOp",EDGE,"b2b48e4d-2c92-4a1f-81ad-3469f6dd68cb")])]}),"instanceName":"5"});
            var Q482;
            Q482=makeQuery(id+"F1.opExtrude","SWEPT_EDGE",EDGE,{"disambiguationData":[OSD([sQuery(id+"F0.wireOp",EDGE,"E16.MirrorCS"),sQuery(id+"F0.wireOp",EDGE,"E17.MirrorCS")])]});
            var Q483;
            Q483=makeQuery(id+"F1.opExtrude","CAP_EDGE",EDGE,{"disambiguationData":[OSD([sQuery(id+"F0.wireOp",EDGE,"E6")])],"isStart":true});
            var Q484;
            Q484=makeQuery(id+"F1.opExtrude","CAP_EDGE",EDGE,{"disambiguationData":[OSD([sQuery(id+"F0.wireOp",EDGE,"E23.MirrorCS")])],"isStart":true});
            var Q485;
            Q485=makeQuery(id+"F1.opExtrude","SWEPT_EDGE",EDGE,{"disambiguationData":[OSD([sQuery(id+"F0.wireOp",EDGE,"E160.MirrorCS"),sQuery(id+"F0.wireOp",EDGE,"E25.MirrorCS")])]});
            var Q486;
            Q486=makeQuery(id+"F1.opExtrude","CAP_EDGE",EDGE,{"disambiguationData":[OSD([sQuery(id+"F0.wireOp",EDGE,"E16.MirrorCS")])],"isStart":true});
            var Q487;
            Q487=makeQuery(id+"F3.opPattern","COPY",EDGE,{"derivedFrom":makeQuery(id+"F1.opExtrude","SWEPT_EDGE",EDGE,{"disambiguationData":[OSD([sQuery(id+"F0.wireOp",EDGE,"E6"),sQuery(id+"F0.wireOp",EDGE,"E7")])]}),"instanceName":"3"});
            var Q488;
            Q488=makeQuery(id+"F3.opPattern","COPY",EDGE,{"derivedFrom":makeQuery(id+"F1.opExtrude","CAP_EDGE",EDGE,{"disambiguationData":[OSD([sQuery(id+"F0.wireOp",EDGE,"E11")])],"isStart":true}),"instanceName":"5"});
            var Q489;
            Q489=makeQuery(id+"F3.opPattern","COPY",EDGE,{"derivedFrom":makeQuery(id+"F1.opExtrude","CAP_EDGE",EDGE,{"disambiguationData":[OSD([sQuery(id+"F0.wireOp",EDGE,"E16.MirrorCS")])],"isStart":true}),"instanceName":"2"});
            var Q490;
            Q490=makeQuery(id+"F3.opPattern","COPY",EDGE,{"derivedFrom":makeQuery(id+"F1.opExtrude","SWEPT_EDGE",EDGE,{"disambiguationData":[OSD([sQuery(id+"F0.wireOp",EDGE,"E7"),sQuery(id+"F0.wireOp",EDGE,"E8")])]}),"instanceName":"3"});
            var Q491;
            Q491=makeQuery(id+"F3.opPattern","COPY",EDGE,{"derivedFrom":makeQuery(id+"F1.opExtrude","CAP_EDGE",EDGE,{"disambiguationData":[OSD([sQuery(id+"F0.wireOp",EDGE,"E5")])],"isStart":true}),"instanceName":"4"});
            var Q492;
            Q492=makeQuery(id+"F3.opPattern","COPY",EDGE,{"derivedFrom":makeQuery(id+"F1.opExtrude","SWEPT_EDGE",EDGE,{"disambiguationData":[OSD([sQuery(id+"F0.wireOp",EDGE,"E8"),sQuery(id+"F0.wireOp",EDGE,"E9")])]}),"instanceName":"3"});
            var Q493;
            Q493=makeQuery(id+"F3.opPattern","COPY",EDGE,{"derivedFrom":makeQuery(id+"F1.opExtrude","SWEPT_EDGE",EDGE,{"disambiguationData":[OSD([sQuery(id+"F0.wireOp",EDGE,"E18.MirrorCS"),sQuery(id+"F0.wireOp",EDGE,"E19.MirrorCS")])]}),"instanceName":"4"});
            var Q494;
            Q494=makeQuery(id+"F3.opPattern","COPY",EDGE,{"derivedFrom":makeQuery(id+"F1.opExtrude","CAP_EDGE",EDGE,{"disambiguationData":[OSD([sQuery(id+"F0.wireOp",EDGE,"E23.MirrorCS")])],"isStart":true}),"instanceName":"3"});
            var Q495;
            Q495=makeQuery(id+"F3.opPattern","COPY",EDGE,{"derivedFrom":makeQuery(id+"F1.opExtrude","SWEPT_EDGE",EDGE,{"disambiguationData":[OSD([sQuery(id+"F0.wireOp",EDGE,"E15.MirrorCS"),sQuery(id+"F0.wireOp",EDGE,"E17.MirrorCS")])]}),"instanceName":"1"});
            var Q496;
            Q496=makeQuery(id+"F3.opPattern","COPY",EDGE,{"derivedFrom":makeQuery(id+"F1.opExtrude","SWEPT_EDGE",EDGE,{"disambiguationData":[OSD([sQuery(id+"F0.wireOp",EDGE,"E6"),sQuery(id+"F0.wireOp",EDGE,"E7")])]}),"instanceName":"4"});
            var Q497;
            Q497=makeQuery(id+"F3.opPattern","COPY",EDGE,{"derivedFrom":makeQuery(id+"F1.opExtrude","SWEPT_EDGE",EDGE,{"disambiguationData":[OSD([sQuery(id+"F0.wireOp",EDGE,"E2"),sQuery(id+"F0.wireOp",EDGE,"E3")])]}),"instanceName":"5"});
            var Q498;
            Q498=makeQuery(id+"F3.opPattern","COPY",EDGE,{"derivedFrom":makeQuery(id+"F1.opExtrude","SWEPT_EDGE",EDGE,{"disambiguationData":[OSD([sQuery(id+"F0.wireOp",EDGE,"E7"),sQuery(id+"F0.wireOp",EDGE,"E8")])]}),"instanceName":"4"});
            var Q499;
            Q499=makeQuery(id+"F3.opPattern","COPY",EDGE,{"derivedFrom":makeQuery(id+"F1.opExtrude","SWEPT_EDGE",EDGE,{"disambiguationData":[OSD([sQuery(id+"F0.wireOp",EDGE,"E3"),sQuery(id+"F0.wireOp",EDGE,"E4")])]}),"instanceName":"5"});
            var Q500;
            Q500=makeQuery(id+"F3.opPattern","COPY",EDGE,{"derivedFrom":makeQuery(id+"F1.opExtrude","CAP_EDGE",EDGE,{"disambiguationData":[OSD([sQuery(id+"F0.wireOp",EDGE,"E22.MirrorCS")])],"isStart":true}),"instanceName":"4"});
            var Q501;
            Q501=makeQuery(id+"F3.opPattern","COPY",EDGE,{"derivedFrom":makeQuery(id+"F1.opExtrude","CAP_EDGE",EDGE,{"disambiguationData":[OSD([sQuery(id+"F0.wireOp",EDGE,"E5")])],"isStart":true}),"instanceName":"5"});
            var Q502;
            Q502=makeQuery(id+"F3.opPattern","COPY",EDGE,{"derivedFrom":makeQuery(id+"F1.opExtrude","SWEPT_EDGE",EDGE,{"disambiguationData":[OSD([sQuery(id+"F0.wireOp",EDGE,"E5"),sQuery(id+"F0.wireOp",EDGE,"E6")])]}),"instanceName":"5"});
            var Q503;
            Q503=makeQuery(id+"F3.opPattern","COPY",EDGE,{"derivedFrom":makeQuery(id+"F1.opExtrude","CAP_EDGE",EDGE,{"disambiguationData":[OSD([sQuery(id+"F0.wireOp",EDGE,"E14")])],"isStart":true}),"instanceName":"5"});
            var Q504;
            Q504=makeQuery(id+"F3.opPattern","COPY",EDGE,{"derivedFrom":makeQuery(id+"F1.opExtrude","SWEPT_EDGE",EDGE,{"disambiguationData":[OSD([sQuery(id+"F0.wireOp",EDGE,"E18.MirrorCS"),sQuery(id+"F0.wireOp",EDGE,"E19.MirrorCS")])]}),"instanceName":"5"});
            var Q505;
            Q505=makeQuery(id+"F3.opPattern","COPY",EDGE,{"derivedFrom":makeQuery(id+"F1.opExtrude","CAP_EDGE",EDGE,{"disambiguationData":[OSD([sQuery(id+"F0.wireOp",EDGE,"E6")])],"isStart":true}),"instanceName":"5"});
            var Q506;
            Q506=makeQuery(id+"F3.opPattern","COPY",EDGE,{"derivedFrom":makeQuery(id+"F1.opExtrude","SWEPT_EDGE",EDGE,{"disambiguationData":[OSD([sQuery(id+"F0.wireOp",EDGE,"E15.MirrorCS"),sQuery(id+"F0.wireOp",EDGE,"E17.MirrorCS")])]}),"instanceName":"2"});
            var Q507;
            Q507=makeQuery(id+"F3.opPattern","COPY",EDGE,{"derivedFrom":makeQuery(id+"F1.opExtrude","SWEPT_EDGE",EDGE,{"disambiguationData":[OSD([sQuery(id+"F0.wireOp",EDGE,"E9"),sQuery(id+"F0.wireOp",EDGE,"E10")])]}),"instanceName":"4"});
            var Q508;
            Q508=makeQuery(id+"F3.opPattern","COPY",EDGE,{"derivedFrom":makeQuery(id+"F1.opExtrude","SWEPT_EDGE",EDGE,{"disambiguationData":[OSD([sQuery(id+"F0.wireOp",EDGE,"E23.MirrorCS"),sQuery(id+"F0.wireOp",EDGE,"E24.MirrorCS")])]}),"instanceName":"4"});
            var Q509;
            Q509=makeQuery(id+"F3.opPattern","COPY",EDGE,{"derivedFrom":makeQuery(id+"F1.opExtrude","SWEPT_EDGE",EDGE,{"disambiguationData":[OSD([sQuery(id+"F0.wireOp",EDGE,"E19.MirrorCS"),sQuery(id+"F0.wireOp",EDGE,"E20.MirrorCS")])]}),"instanceName":"5"});
            var Q510;
            Q510=makeQuery(id+"F3.opPattern","COPY",EDGE,{"derivedFrom":makeQuery(id+"F1.opExtrude","SWEPT_EDGE",EDGE,{"disambiguationData":[OSD([sQuery(id+"F0.wireOp",EDGE,"E160.MirrorCS"),sQuery(id+"F0.wireOp",EDGE,"E25.MirrorCS")])]}),"instanceName":"4"});
            var Q511;
            Q511=makeQuery(id+"F3.opPattern","COPY",EDGE,{"derivedFrom":makeQuery(id+"F1.opExtrude","SWEPT_EDGE",EDGE,{"disambiguationData":[OSD([sQuery(id+"F0.wireOp",EDGE,"E14"),sQuery(id+"F0.wireOp",EDGE,"b2b48e4d-2c92-4a1f-81ad-3469f6dd68cb")])]}),"instanceName":"3"});
            var Q512;
            Q512=makeQuery(id+"F3.opPattern","COPY",EDGE,{"derivedFrom":makeQuery(id+"F1.opExtrude","SWEPT_EDGE",EDGE,{"disambiguationData":[OSD([sQuery(id+"F0.wireOp",EDGE,"E10"),sQuery(id+"F0.wireOp",EDGE,"E11")])]}),"instanceName":"4"});
            var Q513;
            Q513=makeQuery(id+"F3.opPattern","COPY",EDGE,{"derivedFrom":makeQuery(id+"F1.opExtrude","CAP_EDGE",EDGE,{"disambiguationData":[OSD([sQuery(id+"F0.wireOp",EDGE,"E22.MirrorCS")])],"isStart":true}),"instanceName":"1"});
            var Q514;
            Q514=makeQuery(id+"F3.opPattern","COPY",EDGE,{"derivedFrom":makeQuery(id+"F1.opExtrude","SWEPT_EDGE",EDGE,{"disambiguationData":[OSD([sQuery(id+"F0.wireOp",EDGE,"E20.MirrorCS"),sQuery(id+"F0.wireOp",EDGE,"E25.MirrorCS")])]}),"instanceName":"5"});
            var Q515;
            Q515=makeQuery(id+"F3.opPattern","COPY",EDGE,{"derivedFrom":makeQuery(id+"F1.opExtrude","SWEPT_EDGE",EDGE,{"disambiguationData":[OSD([sQuery(id+"F0.wireOp",EDGE,"E21.MirrorCS"),sQuery(id+"F0.wireOp",EDGE,"E24.MirrorCS")])]}),"instanceName":"1"});
            var Q516;
            Q516=makeQuery(id+"F3.opPattern","COPY",EDGE,{"derivedFrom":makeQuery(id+"F1.opExtrude","SWEPT_EDGE",EDGE,{"disambiguationData":[OSD([sQuery(id+"F0.wireOp",EDGE,"E8"),sQuery(id+"F0.wireOp",EDGE,"E9")])]}),"instanceName":"5"});
            var Q517;
            Q517=makeQuery(id+"F3.opPattern","COPY",EDGE,{"derivedFrom":makeQuery(id+"F1.opExtrude","SWEPT_EDGE",EDGE,{"disambiguationData":[OSD([sQuery(id+"F0.wireOp",EDGE,"E18.MirrorCS"),sQuery(id+"F0.wireOp",EDGE,"E19.MirrorCS")])]}),"instanceName":"2"});
            var Q518;
            Q518=makeQuery(id+"F3.opPattern","COPY",EDGE,{"derivedFrom":makeQuery(id+"F1.opExtrude","CAP_EDGE",EDGE,{"disambiguationData":[OSD([sQuery(id+"F0.wireOp",EDGE,"E14")])],"isStart":true}),"instanceName":"2"});
            var Q519;
            Q519=makeQuery(id+"F3.opPattern","COPY",EDGE,{"derivedFrom":makeQuery(id+"F1.opExtrude","SWEPT_EDGE",EDGE,{"disambiguationData":[OSD([sQuery(id+"F0.wireOp",EDGE,"E13"),sQuery(id+"F0.wireOp",EDGE,"E14")])]}),"instanceName":"4"});
            var Q520;
            Q520=makeQuery(id+"F3.opPattern","COPY",EDGE,{"derivedFrom":makeQuery(id+"F1.opExtrude","CAP_EDGE",EDGE,{"disambiguationData":[OSD([sQuery(id+"F0.wireOp",EDGE,"E15.MirrorCS")])],"isStart":true}),"instanceName":"5"});
            var Q521;
            Q521=makeQuery(id+"F3.opPattern","COPY",EDGE,{"derivedFrom":makeQuery(id+"F1.opExtrude","SWEPT_EDGE",EDGE,{"disambiguationData":[OSD([sQuery(id+"F0.wireOp",EDGE,"E16.MirrorCS"),sQuery(id+"F0.wireOp",EDGE,"E17.MirrorCS")])]}),"instanceName":"3"});
            var Q522;
            Q522=makeQuery(id+"F3.opPattern","COPY",EDGE,{"derivedFrom":makeQuery(id+"F1.opExtrude","SWEPT_EDGE",EDGE,{"disambiguationData":[OSD([sQuery(id+"F0.wireOp",EDGE,"E160.MirrorCS"),sQuery(id+"F0.wireOp",EDGE,"E25.MirrorCS")])]}),"instanceName":"5"});
            var Q523;
            Q523=makeQuery(id+"F3.opPattern","COPY",EDGE,{"derivedFrom":makeQuery(id+"F1.opExtrude","CAP_EDGE",EDGE,{"disambiguationData":[OSD([sQuery(id+"F0.wireOp",EDGE,"E20.MirrorCS")])],"isStart":true}),"instanceName":"3"});
            var Q524;
            Q524=makeQuery(id+"F3.opPattern","COPY",EDGE,{"derivedFrom":makeQuery(id+"F1.opExtrude","CAP_EDGE",EDGE,{"disambiguationData":[OSD([sQuery(id+"F0.wireOp",EDGE,"E11")])],"isStart":true}),"instanceName":"4"});
            var Q525;
            Q525=makeQuery(id+"F3.opPattern","COPY",EDGE,{"derivedFrom":makeQuery(id+"F1.opExtrude","CAP_EDGE",EDGE,{"disambiguationData":[OSD([sQuery(id+"F0.wireOp",EDGE,"b2b48e4d-2c92-4a1f-81ad-3469f6dd68cb")])],"isStart":true}),"instanceName":"5"});
            var Q526;
            Q526=makeQuery(id+"F3.opPattern","COPY",EDGE,{"derivedFrom":makeQuery(id+"F1.opExtrude","CAP_EDGE",EDGE,{"disambiguationData":[OSD([sQuery(id+"F0.wireOp",EDGE,"E16.MirrorCS")])],"isStart":true}),"instanceName":"5"});
            var Q527;
            Q527=makeQuery(id+"F3.opPattern","COPY",EDGE,{"derivedFrom":makeQuery(id+"F1.opExtrude","SWEPT_EDGE",EDGE,{"disambiguationData":[OSD([sQuery(id+"F0.wireOp",EDGE,"E4"),sQuery(id+"F0.wireOp",EDGE,"E5")])]}),"instanceName":"3"});
            var Q528;
            Q528=makeQuery(id+"F3.opPattern","COPY",EDGE,{"derivedFrom":makeQuery(id+"F1.opExtrude","CAP_EDGE",EDGE,{"disambiguationData":[OSD([sQuery(id+"F0.wireOp",EDGE,"E8")])],"isStart":true}),"instanceName":"2"});
            var Q529;
            Q529=makeQuery(id+"F3.opPattern","COPY",EDGE,{"derivedFrom":makeQuery(id+"F1.opExtrude","SWEPT_EDGE",EDGE,{"disambiguationData":[OSD([sQuery(id+"F0.wireOp",EDGE,"E23.MirrorCS"),sQuery(id+"F0.wireOp",EDGE,"E24.MirrorCS")])]}),"instanceName":"2"});
            var Q530;
            Q530=makeQuery(id+"F3.opPattern","COPY",EDGE,{"derivedFrom":makeQuery(id+"F1.opExtrude","SWEPT_EDGE",EDGE,{"disambiguationData":[OSD([sQuery(id+"F0.wireOp",EDGE,"E2"),sQuery(id+"F0.wireOp",EDGE,"E22.MirrorCS")])]}),"instanceName":"4"});
            var Q531;
            Q531=makeQuery(id+"F3.opPattern","COPY",EDGE,{"derivedFrom":makeQuery(id+"F1.opExtrude","CAP_EDGE",EDGE,{"disambiguationData":[OSD([sQuery(id+"F0.wireOp",EDGE,"E6")])],"isStart":true}),"instanceName":"3"});
            var Q532;
            Q532=makeQuery(id+"F3.opPattern","COPY",EDGE,{"derivedFrom":makeQuery(id+"F1.opExtrude","SWEPT_EDGE",EDGE,{"disambiguationData":[OSD([sQuery(id+"F0.wireOp",EDGE,"E15.MirrorCS"),sQuery(id+"F0.wireOp",EDGE,"E17.MirrorCS")])]}),"instanceName":"4"});
            var Q533;
            Q533=makeQuery(id+"F3.boolean.opBoolean","INTERSECT",EDGE,{"derivedFrom":[makeQuery(id+"F1.opExtrude","SWEPT_FACE",FACE,{"disambiguationData":[OSD([sQuery(id+"F0.wireOp",EDGE,"b2b48e4d-2c92-4a1f-81ad-3469f6dd68cb")])]}),makeQuery(id+"F3.opPattern","COPY",FACE,{"derivedFrom":makeQuery(id+"F1.opExtrude","SWEPT_FACE",FACE,{"disambiguationData":[OSD([sQuery(id+"F0.wireOp",EDGE,"E160.MirrorCS")])]}),"instanceName":"5"})]});
            var Q534;
            Q534=makeQuery(id+"F3.boolean.opBoolean","INTERSECT",EDGE,{"derivedFrom":[makeQuery(id+"F1.opExtrude","SWEPT_FACE",FACE,{"disambiguationData":[OSD([sQuery(id+"F0.wireOp",EDGE,"E160.MirrorCS")])]}),makeQuery(id+"F3.opPattern","COPY",FACE,{"derivedFrom":makeQuery(id+"F1.opExtrude","SWEPT_FACE",FACE,{"disambiguationData":[OSD([sQuery(id+"F0.wireOp",EDGE,"b2b48e4d-2c92-4a1f-81ad-3469f6dd68cb")])]}),"instanceName":"1"})]});
            var Q535;
            Q535=makeQuery(id+"F1.opExtrude","SWEPT_EDGE",EDGE,{"disambiguationData":[OSD([sQuery(id+"F0.wireOp",EDGE,"E6"),sQuery(id+"F0.wireOp",EDGE,"E7")])]});
            var Q536;
            Q536=makeQuery(id+"F1.opExtrude","SWEPT_EDGE",EDGE,{"disambiguationData":[OSD([sQuery(id+"F0.wireOp",EDGE,"E7"),sQuery(id+"F0.wireOp",EDGE,"E8")])]});
            var Q537;
            Q537=makeQuery(id+"F1.opExtrude","SWEPT_EDGE",EDGE,{"disambiguationData":[OSD([sQuery(id+"F0.wireOp",EDGE,"E8"),sQuery(id+"F0.wireOp",EDGE,"E9")])]});
            var Q538;
            Q538=makeQuery(id+"F1.opExtrude","SWEPT_EDGE",EDGE,{"disambiguationData":[OSD([sQuery(id+"F0.wireOp",EDGE,"E11"),sQuery(id+"F0.wireOp",EDGE,"E12")])]});
            var Q539;
            Q539=makeQuery(id+"F3.opPattern","COPY",EDGE,{"derivedFrom":makeQuery(id+"F1.opExtrude","SWEPT_EDGE",EDGE,{"disambiguationData":[OSD([sQuery(id+"F0.wireOp",EDGE,"E2"),sQuery(id+"F0.wireOp",EDGE,"E3")])]}),"instanceName":"1"});
            var Q540;
            Q540=makeQuery(id+"F3.boolean.opBoolean","INTERSECT",EDGE,{"derivedFrom":[makeQuery(id+"F3.opPattern","COPY",FACE,{"derivedFrom":makeQuery(id+"F1.opExtrude","SWEPT_FACE",FACE,{"disambiguationData":[OSD([sQuery(id+"F0.wireOp",EDGE,"E160.MirrorCS")])]}),"instanceName":"1"}),makeQuery(id+"F3.opPattern","COPY",FACE,{"derivedFrom":makeQuery(id+"F1.opExtrude","SWEPT_FACE",FACE,{"disambiguationData":[OSD([sQuery(id+"F0.wireOp",EDGE,"b2b48e4d-2c92-4a1f-81ad-3469f6dd68cb")])]}),"instanceName":"2"})]});
            var Q541;
            Q541=makeQuery(id+"F3.opPattern","COPY",EDGE,{"derivedFrom":makeQuery(id+"F1.opExtrude","SWEPT_EDGE",EDGE,{"disambiguationData":[OSD([sQuery(id+"F0.wireOp",EDGE,"E5"),sQuery(id+"F0.wireOp",EDGE,"E6")])]}),"instanceName":"1"});
            var Q542;
            Q542=makeQuery(id+"F3.opPattern","COPY",EDGE,{"derivedFrom":makeQuery(id+"F1.opExtrude","SWEPT_EDGE",EDGE,{"disambiguationData":[OSD([sQuery(id+"F0.wireOp",EDGE,"E6"),sQuery(id+"F0.wireOp",EDGE,"E7")])]}),"instanceName":"1"});
            var Q543;
            Q543=makeQuery(id+"F3.opPattern","COPY",EDGE,{"derivedFrom":makeQuery(id+"F1.opExtrude","SWEPT_EDGE",EDGE,{"disambiguationData":[OSD([sQuery(id+"F0.wireOp",EDGE,"E7"),sQuery(id+"F0.wireOp",EDGE,"E8")])]}),"instanceName":"1"});
            var Q544;
            Q544=makeQuery(id+"F1.opExtrude","CAP_EDGE",EDGE,{"disambiguationData":[OSD([sQuery(id+"F0.wireOp",EDGE,"b2b48e4d-2c92-4a1f-81ad-3469f6dd68cb")])],"isStart":true});
            var Q545;
            Q545=makeQuery(id+"F3.opPattern","COPY",EDGE,{"derivedFrom":makeQuery(id+"F1.opExtrude","SWEPT_EDGE",EDGE,{"disambiguationData":[OSD([sQuery(id+"F0.wireOp",EDGE,"E10"),sQuery(id+"F0.wireOp",EDGE,"E11")])]}),"instanceName":"1"});
            var Q546;
            Q546=makeQuery(id+"F3.opPattern","COPY",EDGE,{"derivedFrom":makeQuery(id+"F1.opExtrude","SWEPT_EDGE",EDGE,{"disambiguationData":[OSD([sQuery(id+"F0.wireOp",EDGE,"E12"),sQuery(id+"F0.wireOp",EDGE,"E13")])]}),"instanceName":"1"});
            var Q547;
            Q547=makeQuery(id+"F3.opPattern","COPY",EDGE,{"derivedFrom":makeQuery(id+"F1.opExtrude","SWEPT_EDGE",EDGE,{"disambiguationData":[OSD([sQuery(id+"F0.wireOp",EDGE,"E15.MirrorCS"),sQuery(id+"F0.wireOp",EDGE,"E17.MirrorCS")])]}),"instanceName":"5"});
            var Q548;
            Q548=makeQuery(id+"F3.opPattern","COPY",EDGE,{"derivedFrom":makeQuery(id+"F1.opExtrude","SWEPT_EDGE",EDGE,{"disambiguationData":[OSD([sQuery(id+"F0.wireOp",EDGE,"E16.MirrorCS"),sQuery(id+"F0.wireOp",EDGE,"E23.MirrorCS")])]}),"instanceName":"5"});
            var Q549;
            Q549=makeQuery(id+"F3.boolean.opBoolean","INTERSECT",EDGE,{"derivedFrom":[makeQuery(id+"F3.opPattern","COPY",FACE,{"derivedFrom":makeQuery(id+"F1.opExtrude","SWEPT_FACE",FACE,{"disambiguationData":[OSD([sQuery(id+"F0.wireOp",EDGE,"E160.MirrorCS")])]}),"instanceName":"4"}),makeQuery(id+"F3.opPattern","COPY",FACE,{"derivedFrom":makeQuery(id+"F1.opExtrude","SWEPT_FACE",FACE,{"disambiguationData":[OSD([sQuery(id+"F0.wireOp",EDGE,"b2b48e4d-2c92-4a1f-81ad-3469f6dd68cb")])]}),"instanceName":"5"})]});
            var Q550;
            Q550=makeQuery(id+"F3.opPattern","COPY",EDGE,{"derivedFrom":makeQuery(id+"F1.opExtrude","SWEPT_EDGE",EDGE,{"disambiguationData":[OSD([sQuery(id+"F0.wireOp",EDGE,"E8"),sQuery(id+"F0.wireOp",EDGE,"E9")])]}),"instanceName":"2"});
            var Q551;
            Q551=makeQuery(id+"F3.opPattern","COPY",EDGE,{"derivedFrom":makeQuery(id+"F1.opExtrude","SWEPT_EDGE",EDGE,{"disambiguationData":[OSD([sQuery(id+"F0.wireOp",EDGE,"E15.MirrorCS"),sQuery(id+"F0.wireOp",EDGE,"E22.MirrorCS")])]}),"instanceName":"4"});
            var Q552;
            Q552=makeQuery(id+"F1.opExtrude","SWEPT_EDGE",EDGE,{"disambiguationData":[OSD([sQuery(id+"F0.wireOp",EDGE,"E14"),sQuery(id+"F0.wireOp",EDGE,"b2b48e4d-2c92-4a1f-81ad-3469f6dd68cb")])]});
            var Q553;
            Q553=makeQuery(id+"F1.opExtrude","SWEPT_EDGE",EDGE,{"disambiguationData":[OSD([sQuery(id+"F0.wireOp",EDGE,"E5"),sQuery(id+"F0.wireOp",EDGE,"E6")])]});
            var Q554;
            Q554=makeQuery(id+"F3.opPattern","COPY",EDGE,{"derivedFrom":makeQuery(id+"F1.opExtrude","SWEPT_EDGE",EDGE,{"disambiguationData":[OSD([sQuery(id+"F0.wireOp",EDGE,"E2"),sQuery(id+"F0.wireOp",EDGE,"E22.MirrorCS")])]}),"instanceName":"1"});
            fillet(context, id + "F4", {"entities" : qUnion([Q0, Q1, Q2, Q3, Q4, Q5, Q6, Q7, Q8, Q9, Q10, Q11, Q12, Q13, Q14, Q15, Q16, Q17, Q18, Q19, Q20, Q21, Q22, Q23, Q24, Q25, Q26, Q27, Q28, Q29, Q30, Q31, Q32, Q33, Q34, Q35, Q36, Q37, Q38, Q39, Q40, Q41, Q42, Q43, Q44, Q45, Q46, Q47, Q48, Q49, Q50, Q51, Q52, Q53, Q54, Q55, Q56, Q57, Q58, Q59, Q60, Q61, Q62, Q63, Q64, Q65, Q66, Q67, Q68, Q69, Q70, Q71, Q72, Q73, Q74, Q75, Q76, Q77, Q78, Q79, Q80, Q81, Q82, Q83, Q84, Q85, Q86, Q87, Q88, Q89, Q90, Q91, Q92, Q93, Q94, Q95, Q96, Q97, Q98, Q99, Q100, Q101, Q102, Q103, Q104, Q105, Q106, Q107, Q108, Q109, Q110, Q111, Q112, Q113, Q114, Q115, Q116, Q117, Q118, Q119, Q120, Q121, Q122, Q123, Q124, Q125, Q126, Q127, Q128, Q129, Q130, Q131, Q132, Q133, Q134, Q135, Q136, Q137, Q138, Q139, Q140, Q141, Q142, Q143, Q144, Q145, Q146, Q147, Q148, Q149, Q150, Q151, Q152, Q153, Q154, Q155, Q156, Q157, Q158, Q159, Q160, Q161, Q162, Q163, Q164, Q165, Q166, Q167, Q168, Q169, Q170, Q171, Q172, Q173, Q174, Q175, Q176, Q177, Q178, Q179, Q180, Q181, Q182, Q183, Q184, Q185, Q186, Q187, Q188, Q189, Q190, Q191, Q192, Q193, Q194, Q195, Q196, Q197, Q198, Q199, Q200, Q201, Q202, Q203, Q204, Q205, Q206, Q207, Q208, Q209, Q210, Q211, Q212, Q213, Q214, Q215, Q216, Q217, Q218, Q219, Q220, Q221, Q222, Q223, Q224, Q225, Q226, Q227, Q228, Q229, Q230, Q231, Q232, Q233, Q234, Q235, Q236, Q237, Q238, Q239, Q240, Q241, Q242, Q243, Q244, Q245, Q246, Q247, Q248, Q249, Q250, Q251, Q252, Q253, Q254, Q255, Q256, Q257, Q258, Q259, Q260, Q261, Q262, Q263, Q264, Q265, Q266, Q267, Q268, Q269, Q270, Q271, Q272, Q273, Q274, Q275, Q276, Q277, Q278, Q279, Q280, Q281, Q282, Q283, Q284, Q285, Q286, Q287, Q288, Q289, Q290, Q291, Q292, Q293, Q294, Q295, Q296, Q297, Q298, Q299, Q300, Q301, Q302, Q303, Q304, Q305, Q306, Q307, Q308, Q309, Q310, Q311, Q312, Q313, Q314, Q315, Q316, Q317, Q318, Q319, Q320, Q321, Q322, Q323, Q324, Q325, Q326, Q327, Q328, Q329, Q330, Q331, Q332, Q333, Q334, Q335, Q336, Q337, Q338, Q339, Q340, Q341, Q342, Q343, Q344, Q345, Q346, Q347, Q348, Q349, Q350, Q351, Q352, Q353, Q354, Q355, Q356, Q357, Q358, Q359, Q360, Q361, Q362, Q363, Q364, Q365, Q366, Q367, Q368, Q369, Q370, Q371, Q372, Q373, Q374, Q375, Q376, Q377, Q378, Q379, Q380, Q381, Q382, Q383, Q384, Q385, Q386, Q387, Q388, Q389, Q390, Q391, Q392, Q393, Q394, Q395, Q396, Q397, Q398, Q399, Q400, Q401, Q402, Q403, Q404, Q405, Q406, Q407, Q408, Q409, Q410, Q411, Q412, Q413, Q414, Q415, Q416, Q417, Q418, Q419, Q420, Q421, Q422, Q423, Q424, Q425, Q426, Q427, Q428, Q429, Q430, Q431, Q432, Q433, Q434, Q435, Q436, Q437, Q438, Q439, Q440, Q441, Q442, Q443, Q444, Q445, Q446, Q447, Q448, Q449, Q450, Q451, Q452, Q453, Q454, Q455, Q456, Q457, Q458, Q459, Q460, Q461, Q462, Q463, Q464, Q465, Q466, Q467, Q468, Q469, Q470, Q471, Q472, Q473, Q474, Q475, Q476, Q477, Q478, Q479, Q480, Q481, Q482, Q483, Q484, Q485, Q486, Q487, Q488, Q489, Q490, Q491, Q492, Q493, Q494, Q495, Q496, Q497, Q498, Q499, Q500, Q501, Q502, Q503, Q504, Q505, Q506, Q507, Q508, Q509, Q510, Q511, Q512, Q513, Q514, Q515, Q516, Q517, Q518, Q519, Q520, Q521, Q522, Q523, Q524, Q525, Q526, Q527, Q528, Q529, Q530, Q531, Q532, Q533, Q534, Q535, Q536, Q537, Q538, Q539, Q540, Q541, Q542, Q543, Q544, Q545, Q546, Q547, Q548, Q549, Q550, Q551, Q552, Q553, Q554]), "radius" : 0.5 * mm, "tangentPropagation" : true, "allowEdgeOverflow" : false});
        }
        {
            var Q0;
            Q0=qCreatedBy(makeId("Front.planeOp"),FACE);
            cPlane(context, id + "F5", {"entities" : qUnion([Q0]), "cplaneType" : CPlaneType.OFFSET, "offset" : 25 * mm, "oppositeDirection" : true, "width" : 150 * mm, "height" : 150 * mm});
        }
        {
            var Q0;
            Q0=qCreatedBy(id+"F5.planeOp",FACE);
            var sketch = newSketch(context, id + "F6", { "sketchPlane" : qUnion([Q0])});
            skCircle(sketch, "E36", {"center": v(0, 0) * mm, "radius": 0.5 * mm});
            skSolve(sketch);
        }
        {
            var Q0;
            Q0=makeQuery(id+"F6.imprint","IMPRINT",FACE,{"disambiguationData":[TD([[makeQuery(id+"F6.imprint","IMPRINT",EDGE,{"derivedFrom":sQuery(id+"F6.wireOp",EDGE,"E36")}),1.0]])]});
            extrude(context, id + "F7", {"entities" : qUnion([Q0]), "operationType" : NewBodyOperationType.REMOVE, "depth" : 2 * mm});
        }
    });
